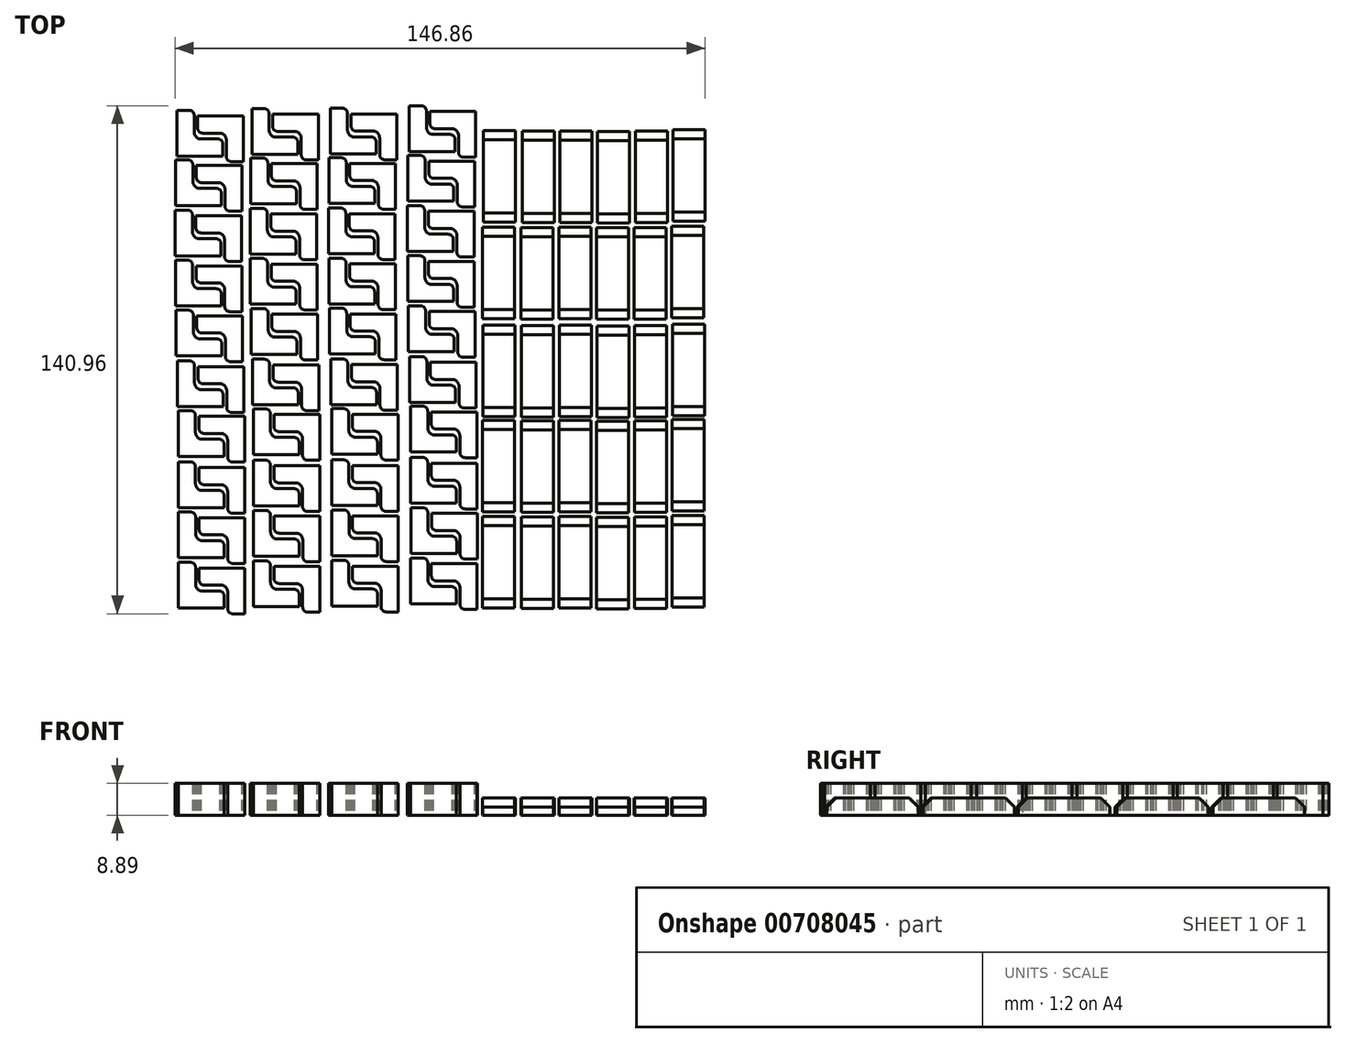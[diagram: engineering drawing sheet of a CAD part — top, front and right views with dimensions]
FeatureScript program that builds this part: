
annotation { "Feature Type Name" : "Feature", "Feature Type Description" : "" }
export const myFeature = defineFeature(function(context is Context, id is Id, definition is map)
    precondition{}
    {
        {
            var Q0;
            Q0=qCreatedBy(makeId("Top.planeOp"),FACE);
            var sketch = newSketch(context, id + "F0", { "sketchPlane" : qUnion([Q0])});
            skLineSegment(sketch, "E0.bottom", {"start": v(0, 0) * mm, "end": v(152.4, 0) * mm});
            skLineSegment(sketch, "E0.top", {"start": v(0, 152.4) * mm, "end": v(152.4, 152.4) * mm});
            skLineSegment(sketch, "E0.left", {"start": v(0, 0) * mm, "end": v(0, 152.4) * mm});
            skLineSegment(sketch, "E0.right", {"start": v(152.4, 0) * mm, "end": v(152.4, 152.4) * mm});
            skLineSegment(sketch, "E1.bottom", {"start": v(2.52, 2.34) * mm, "end": v(15.22, 2.34) * mm});
            skLineSegment(sketch, "E1.top", {"start": v(2.52, 15.04) * mm, "end": v(5.86, 15.04) * mm});
            skLineSegment(sketch, "E1.left", {"start": v(2.52, 2.34) * mm, "end": v(2.52, 15.04) * mm});
            skLineSegment(sketch, "E1.right", {"start": v(15.22, 2.34) * mm, "end": v(15.22, 5.68) * mm});
            skLineSegment(sketch, "E2.0", {"start": v(7.28, 9.05) * mm, "end": v(7.28, 13.62) * mm});
            skLineSegment(sketch, "E2.1", {"start": v(8.72, 7.1) * mm, "end": v(13.8, 7.1) * mm});
            skPoint(sketch, "E3.visualSharp", {"position": v(7.28, 15.04) * mm});
            skArc(sketch, "E3.filletArc", {"start": v(7.28, 13.62) * mm, "mid": v(6.87, 14.62) * mm, "end": v(5.86, 15.04) * mm});
            skPoint(sketch, "E4.visualSharp", {"position": v(15.22, 7.1) * mm});
            skArc(sketch, "E4.filletArc", {"start": v(15.22, 5.68) * mm, "mid": v(14.8, 6.69) * mm, "end": v(13.8, 7.1) * mm});
            skArc(sketch, "E5", {"start": v(7.28, 9.05) * mm, "mid": v(7.68, 7.84) * mm, "end": v(8.72, 7.1) * mm});
            skLineSegment(sketch, "E6.bottom", {"start": v(20.95, 13.45) * mm, "end": v(8.25, 13.45) * mm});
            skLineSegment(sketch, "E6.top", {"start": v(20.95, 0.75) * mm, "end": v(17.6, 0.75) * mm});
            skLineSegment(sketch, "E6.left", {"start": v(20.95, 13.45) * mm, "end": v(20.95, 0.75) * mm});
            skLineSegment(sketch, "E6.right", {"start": v(8.25, 13.45) * mm, "end": v(8.25, 10.1) * mm});
            skLineSegment(sketch, "E7.0", {"start": v(16.18, 6.74) * mm, "end": v(16.18, 2.17) * mm});
            skLineSegment(sketch, "E7.1", {"start": v(14.75, 8.68) * mm, "end": v(9.67, 8.68) * mm});
            skArc(sketch, "E8.filletArc", {"start": v(16.18, 2.17) * mm, "mid": v(16.6, 1.16) * mm, "end": v(17.6, 0.75) * mm});
            skArc(sketch, "E9.filletArc", {"start": v(8.25, 10.1) * mm, "mid": v(8.66, 9.1) * mm, "end": v(9.67, 8.68) * mm});
            skArc(sketch, "E10", {"start": v(16.18, 6.74) * mm, "mid": v(15.79, 7.95) * mm, "end": v(14.75, 8.68) * mm});
            skLineSegment(sketch, "E11.bottom", {"start": v(2.54, 16.3) * mm, "end": v(15.24, 16.3) * mm});
            skLineSegment(sketch, "E11.top", {"start": v(2.54, 29) * mm, "end": v(5.88, 29) * mm});
            skLineSegment(sketch, "E11.left", {"start": v(2.54, 16.3) * mm, "end": v(2.54, 29) * mm});
            skLineSegment(sketch, "E11.right", {"start": v(15.24, 16.3) * mm, "end": v(15.24, 19.65) * mm});
            skLineSegment(sketch, "E12.0", {"start": v(7.3, 23.02) * mm, "end": v(7.3, 27.6) * mm});
            skLineSegment(sketch, "E12.1", {"start": v(8.74, 21.07) * mm, "end": v(13.82, 21.07) * mm});
            skArc(sketch, "E13.filletArc", {"start": v(7.3, 27.6) * mm, "mid": v(6.89, 28.6) * mm, "end": v(5.88, 29) * mm});
            skArc(sketch, "E14.filletArc", {"start": v(15.24, 19.65) * mm, "mid": v(14.82, 20.66) * mm, "end": v(13.82, 21.07) * mm});
            skArc(sketch, "E15", {"start": v(7.3, 23.02) * mm, "mid": v(7.7, 21.81) * mm, "end": v(8.74, 21.07) * mm});
            skLineSegment(sketch, "E16.bottom", {"start": v(20.97, 27.42) * mm, "end": v(8.27, 27.42) * mm});
            skLineSegment(sketch, "E16.top", {"start": v(20.97, 14.72) * mm, "end": v(17.62, 14.72) * mm});
            skLineSegment(sketch, "E16.left", {"start": v(20.97, 27.42) * mm, "end": v(20.97, 14.72) * mm});
            skLineSegment(sketch, "E16.right", {"start": v(8.27, 27.42) * mm, "end": v(8.27, 24.07) * mm});
            skLineSegment(sketch, "E17.0", {"start": v(16.2, 20.7) * mm, "end": v(16.2, 16.14) * mm});
            skLineSegment(sketch, "E17.1", {"start": v(14.77, 22.65) * mm, "end": v(9.69, 22.65) * mm});
            skArc(sketch, "E18.filletArc", {"start": v(16.2, 16.14) * mm, "mid": v(16.62, 15.13) * mm, "end": v(17.62, 14.72) * mm});
            skArc(sketch, "E19.filletArc", {"start": v(8.27, 24.07) * mm, "mid": v(8.68, 23.07) * mm, "end": v(9.69, 22.65) * mm});
            skArc(sketch, "E20", {"start": v(16.2, 20.7) * mm, "mid": v(15.8, 21.92) * mm, "end": v(14.77, 22.65) * mm});
            skLineSegment(sketch, "E21.bottom", {"start": v(2.49, 30.24) * mm, "end": v(15.19, 30.24) * mm});
            skLineSegment(sketch, "E21.top", {"start": v(2.49, 42.94) * mm, "end": v(5.83, 42.94) * mm});
            skLineSegment(sketch, "E21.left", {"start": v(2.49, 30.24) * mm, "end": v(2.49, 42.94) * mm});
            skLineSegment(sketch, "E21.right", {"start": v(15.19, 30.24) * mm, "end": v(15.19, 33.58) * mm});
            skLineSegment(sketch, "E22.0", {"start": v(7.25, 36.95) * mm, "end": v(7.25, 41.52) * mm});
            skLineSegment(sketch, "E22.1", {"start": v(8.69, 35) * mm, "end": v(13.77, 35) * mm});
            skArc(sketch, "E23.filletArc", {"start": v(7.25, 41.52) * mm, "mid": v(6.84, 42.52) * mm, "end": v(5.83, 42.94) * mm});
            skArc(sketch, "E24.filletArc", {"start": v(15.19, 33.58) * mm, "mid": v(14.77, 34.59) * mm, "end": v(13.77, 35) * mm});
            skArc(sketch, "E25", {"start": v(7.25, 36.95) * mm, "mid": v(7.65, 35.74) * mm, "end": v(8.69, 35) * mm});
            skLineSegment(sketch, "E26.bottom", {"start": v(20.92, 41.35) * mm, "end": v(8.22, 41.35) * mm});
            skLineSegment(sketch, "E26.top", {"start": v(20.92, 28.65) * mm, "end": v(17.57, 28.65) * mm});
            skLineSegment(sketch, "E26.left", {"start": v(20.92, 41.35) * mm, "end": v(20.92, 28.65) * mm});
            skLineSegment(sketch, "E26.right", {"start": v(8.22, 41.35) * mm, "end": v(8.22, 38) * mm});
            skLineSegment(sketch, "E27.0", {"start": v(16.15, 34.64) * mm, "end": v(16.15, 30.07) * mm});
            skLineSegment(sketch, "E27.1", {"start": v(14.72, 36.58) * mm, "end": v(9.64, 36.58) * mm});
            skArc(sketch, "E28.filletArc", {"start": v(16.15, 30.07) * mm, "mid": v(16.57, 29.06) * mm, "end": v(17.57, 28.65) * mm});
            skArc(sketch, "E29.filletArc", {"start": v(8.22, 38) * mm, "mid": v(8.63, 37) * mm, "end": v(9.64, 36.58) * mm});
            skArc(sketch, "E30", {"start": v(16.15, 34.64) * mm, "mid": v(15.76, 35.84) * mm, "end": v(14.72, 36.58) * mm});
            skLineSegment(sketch, "E31.bottom", {"start": v(2.49, 44.46) * mm, "end": v(15.19, 44.46) * mm});
            skLineSegment(sketch, "E31.top", {"start": v(2.49, 57.16) * mm, "end": v(5.83, 57.16) * mm});
            skLineSegment(sketch, "E31.left", {"start": v(2.49, 44.46) * mm, "end": v(2.49, 57.16) * mm});
            skLineSegment(sketch, "E31.right", {"start": v(15.19, 44.46) * mm, "end": v(15.19, 47.8) * mm});
            skLineSegment(sketch, "E32.0", {"start": v(7.25, 51.17) * mm, "end": v(7.25, 55.74) * mm});
            skLineSegment(sketch, "E32.1", {"start": v(8.69, 49.23) * mm, "end": v(13.77, 49.23) * mm});
            skArc(sketch, "E33.filletArc", {"start": v(7.25, 55.74) * mm, "mid": v(6.84, 56.75) * mm, "end": v(5.83, 57.16) * mm});
            skArc(sketch, "E34.filletArc", {"start": v(15.19, 47.8) * mm, "mid": v(14.77, 48.8) * mm, "end": v(13.77, 49.23) * mm});
            skArc(sketch, "E35", {"start": v(7.25, 51.17) * mm, "mid": v(7.65, 49.96) * mm, "end": v(8.69, 49.23) * mm});
            skLineSegment(sketch, "E36.bottom", {"start": v(20.92, 55.57) * mm, "end": v(8.22, 55.57) * mm});
            skLineSegment(sketch, "E36.top", {"start": v(20.92, 42.87) * mm, "end": v(17.57, 42.87) * mm});
            skLineSegment(sketch, "E36.left", {"start": v(20.92, 55.57) * mm, "end": v(20.92, 42.87) * mm});
            skLineSegment(sketch, "E36.right", {"start": v(8.22, 55.57) * mm, "end": v(8.22, 52.23) * mm});
            skLineSegment(sketch, "E37.0", {"start": v(16.15, 48.86) * mm, "end": v(16.15, 44.29) * mm});
            skLineSegment(sketch, "E37.1", {"start": v(14.72, 50.8) * mm, "end": v(9.64, 50.8) * mm});
            skArc(sketch, "E38.filletArc", {"start": v(16.15, 44.29) * mm, "mid": v(16.57, 43.29) * mm, "end": v(17.57, 42.87) * mm});
            skArc(sketch, "E39.filletArc", {"start": v(8.22, 52.23) * mm, "mid": v(8.63, 51.22) * mm, "end": v(9.64, 50.8) * mm});
            skArc(sketch, "E40", {"start": v(16.15, 48.86) * mm, "mid": v(15.76, 50.07) * mm, "end": v(14.72, 50.8) * mm});
            skLineSegment(sketch, "E41.bottom", {"start": v(2.24, 58.23) * mm, "end": v(14.94, 58.23) * mm});
            skLineSegment(sketch, "E41.top", {"start": v(2.24, 70.93) * mm, "end": v(5.58, 70.93) * mm});
            skLineSegment(sketch, "E41.left", {"start": v(2.24, 58.23) * mm, "end": v(2.24, 70.93) * mm});
            skLineSegment(sketch, "E41.right", {"start": v(14.94, 58.23) * mm, "end": v(14.94, 61.57) * mm});
            skLineSegment(sketch, "E42.0", {"start": v(7, 64.94) * mm, "end": v(7, 69.51) * mm});
            skLineSegment(sketch, "E42.1", {"start": v(8.43, 63) * mm, "end": v(13.52, 63) * mm});
            skArc(sketch, "E43.filletArc", {"start": v(7, 69.51) * mm, "mid": v(6.58, 70.51) * mm, "end": v(5.58, 70.93) * mm});
            skArc(sketch, "E44.filletArc", {"start": v(14.94, 61.57) * mm, "mid": v(14.52, 62.58) * mm, "end": v(13.52, 63) * mm});
            skArc(sketch, "E45", {"start": v(7, 64.94) * mm, "mid": v(7.4, 63.73) * mm, "end": v(8.43, 63) * mm});
            skLineSegment(sketch, "E46.bottom", {"start": v(20.67, 69.34) * mm, "end": v(7.97, 69.34) * mm});
            skLineSegment(sketch, "E46.top", {"start": v(20.67, 56.64) * mm, "end": v(17.32, 56.64) * mm});
            skLineSegment(sketch, "E46.left", {"start": v(20.67, 69.34) * mm, "end": v(20.67, 56.64) * mm});
            skLineSegment(sketch, "E46.right", {"start": v(7.97, 69.34) * mm, "end": v(7.97, 66) * mm});
            skLineSegment(sketch, "E47.0", {"start": v(15.9, 62.63) * mm, "end": v(15.9, 58.06) * mm});
            skLineSegment(sketch, "E47.1", {"start": v(14.47, 64.58) * mm, "end": v(9.39, 64.58) * mm});
            skArc(sketch, "E48.filletArc", {"start": v(15.9, 58.06) * mm, "mid": v(16.32, 57.05) * mm, "end": v(17.32, 56.64) * mm});
            skArc(sketch, "E49.filletArc", {"start": v(7.97, 66) * mm, "mid": v(8.38, 65) * mm, "end": v(9.39, 64.58) * mm});
            skArc(sketch, "E50", {"start": v(15.9, 62.63) * mm, "mid": v(15.5, 63.84) * mm, "end": v(14.47, 64.58) * mm});
            skLineSegment(sketch, "E51.bottom", {"start": v(1.9, 72.32) * mm, "end": v(14.6, 72.32) * mm});
            skLineSegment(sketch, "E51.top", {"start": v(1.9, 85.02) * mm, "end": v(5.24, 85.02) * mm});
            skLineSegment(sketch, "E51.left", {"start": v(1.9, 72.32) * mm, "end": v(1.9, 85.02) * mm});
            skLineSegment(sketch, "E51.right", {"start": v(14.6, 72.32) * mm, "end": v(14.6, 75.66) * mm});
            skLineSegment(sketch, "E52.0", {"start": v(6.66, 79.03) * mm, "end": v(6.66, 83.6) * mm});
            skLineSegment(sketch, "E52.1", {"start": v(8.1, 77.08) * mm, "end": v(13.18, 77.08) * mm});
            skArc(sketch, "E53.filletArc", {"start": v(6.66, 83.6) * mm, "mid": v(6.24, 84.6) * mm, "end": v(5.24, 85.02) * mm});
            skArc(sketch, "E54.filletArc", {"start": v(14.6, 75.66) * mm, "mid": v(14.18, 76.66) * mm, "end": v(13.18, 77.08) * mm});
            skArc(sketch, "E55", {"start": v(6.66, 79.03) * mm, "mid": v(7.06, 77.82) * mm, "end": v(8.1, 77.08) * mm});
            skLineSegment(sketch, "E56.bottom", {"start": v(20.33, 83.42) * mm, "end": v(7.63, 83.42) * mm});
            skLineSegment(sketch, "E56.top", {"start": v(20.33, 70.72) * mm, "end": v(16.98, 70.72) * mm});
            skLineSegment(sketch, "E56.left", {"start": v(20.33, 83.42) * mm, "end": v(20.33, 70.72) * mm});
            skLineSegment(sketch, "E56.right", {"start": v(7.63, 83.42) * mm, "end": v(7.63, 80.08) * mm});
            skLineSegment(sketch, "E57.0", {"start": v(15.56, 76.71) * mm, "end": v(15.56, 72.14) * mm});
            skLineSegment(sketch, "E57.1", {"start": v(14.13, 78.66) * mm, "end": v(9.05, 78.66) * mm});
            skArc(sketch, "E58.filletArc", {"start": v(15.56, 72.14) * mm, "mid": v(15.98, 71.14) * mm, "end": v(16.98, 70.72) * mm});
            skArc(sketch, "E59.filletArc", {"start": v(7.63, 80.08) * mm, "mid": v(8.04, 79.08) * mm, "end": v(9.05, 78.66) * mm});
            skArc(sketch, "E60", {"start": v(15.56, 76.71) * mm, "mid": v(15.17, 77.92) * mm, "end": v(14.13, 78.66) * mm});
            skLineSegment(sketch, "E61.bottom", {"start": v(1.7, 86.2) * mm, "end": v(14.4, 86.2) * mm});
            skLineSegment(sketch, "E61.top", {"start": v(1.7, 98.9) * mm, "end": v(5.05, 98.9) * mm});
            skLineSegment(sketch, "E61.left", {"start": v(1.7, 86.2) * mm, "end": v(1.7, 98.9) * mm});
            skLineSegment(sketch, "E61.right", {"start": v(14.4, 86.2) * mm, "end": v(14.4, 89.55) * mm});
            skLineSegment(sketch, "E62.0", {"start": v(6.47, 92.92) * mm, "end": v(6.47, 97.49) * mm});
            skLineSegment(sketch, "E62.1", {"start": v(7.9, 90.97) * mm, "end": v(12.99, 90.97) * mm});
            skArc(sketch, "E63.filletArc", {"start": v(6.47, 97.49) * mm, "mid": v(6.05, 98.49) * mm, "end": v(5.05, 98.9) * mm});
            skArc(sketch, "E64.filletArc", {"start": v(14.4, 89.55) * mm, "mid": v(14, 90.55) * mm, "end": v(12.99, 90.97) * mm});
            skArc(sketch, "E65", {"start": v(6.47, 92.92) * mm, "mid": v(6.87, 91.7) * mm, "end": v(7.9, 90.97) * mm});
            skLineSegment(sketch, "E66.bottom", {"start": v(20.14, 97.31) * mm, "end": v(7.44, 97.31) * mm});
            skLineSegment(sketch, "E66.top", {"start": v(20.14, 84.61) * mm, "end": v(16.8, 84.61) * mm});
            skLineSegment(sketch, "E66.left", {"start": v(20.14, 97.31) * mm, "end": v(20.14, 84.61) * mm});
            skLineSegment(sketch, "E66.right", {"start": v(7.44, 97.31) * mm, "end": v(7.44, 93.97) * mm});
            skLineSegment(sketch, "E67.0", {"start": v(15.37, 90.6) * mm, "end": v(15.37, 86.03) * mm});
            skLineSegment(sketch, "E67.1", {"start": v(13.94, 92.55) * mm, "end": v(8.86, 92.55) * mm});
            skArc(sketch, "E68.filletArc", {"start": v(15.37, 86.03) * mm, "mid": v(15.79, 85.03) * mm, "end": v(16.8, 84.61) * mm});
            skArc(sketch, "E69.filletArc", {"start": v(7.44, 93.97) * mm, "mid": v(7.85, 92.96) * mm, "end": v(8.86, 92.55) * mm});
            skArc(sketch, "E70", {"start": v(15.37, 90.6) * mm, "mid": v(14.98, 91.81) * mm, "end": v(13.94, 92.55) * mm});
            skLineSegment(sketch, "E71.bottom", {"start": v(1.65, 100.1) * mm, "end": v(14.35, 100.1) * mm});
            skLineSegment(sketch, "E71.top", {"start": v(1.65, 112.8) * mm, "end": v(4.99, 112.8) * mm});
            skLineSegment(sketch, "E71.left", {"start": v(1.65, 100.1) * mm, "end": v(1.65, 112.8) * mm});
            skLineSegment(sketch, "E71.right", {"start": v(14.35, 100.1) * mm, "end": v(14.35, 103.45) * mm});
            skLineSegment(sketch, "E72.0", {"start": v(6.4, 106.81) * mm, "end": v(6.4, 111.38) * mm});
            skLineSegment(sketch, "E72.1", {"start": v(7.84, 104.87) * mm, "end": v(12.93, 104.87) * mm});
            skArc(sketch, "E73.filletArc", {"start": v(6.4, 111.38) * mm, "mid": v(6, 112.39) * mm, "end": v(4.99, 112.8) * mm});
            skArc(sketch, "E74.filletArc", {"start": v(14.35, 103.45) * mm, "mid": v(13.93, 104.45) * mm, "end": v(12.93, 104.87) * mm});
            skArc(sketch, "E75", {"start": v(6.4, 106.81) * mm, "mid": v(6.8, 105.6) * mm, "end": v(7.84, 104.87) * mm});
            skLineSegment(sketch, "E76.bottom", {"start": v(20.07, 111.21) * mm, "end": v(7.37, 111.21) * mm});
            skLineSegment(sketch, "E76.top", {"start": v(20.07, 98.51) * mm, "end": v(16.73, 98.51) * mm});
            skLineSegment(sketch, "E76.left", {"start": v(20.07, 111.21) * mm, "end": v(20.07, 98.51) * mm});
            skLineSegment(sketch, "E76.right", {"start": v(7.37, 111.21) * mm, "end": v(7.37, 107.87) * mm});
            skLineSegment(sketch, "E77.0", {"start": v(15.31, 104.5) * mm, "end": v(15.31, 99.93) * mm});
            skLineSegment(sketch, "E77.1", {"start": v(13.88, 106.45) * mm, "end": v(8.8, 106.45) * mm});
            skArc(sketch, "E78.filletArc", {"start": v(15.31, 99.93) * mm, "mid": v(15.73, 98.93) * mm, "end": v(16.73, 98.51) * mm});
            skArc(sketch, "E79.filletArc", {"start": v(7.37, 107.87) * mm, "mid": v(7.79, 106.86) * mm, "end": v(8.8, 106.45) * mm});
            skArc(sketch, "E80", {"start": v(15.31, 104.5) * mm, "mid": v(14.91, 105.7) * mm, "end": v(13.88, 106.45) * mm});
            skLineSegment(sketch, "E81.bottom", {"start": v(1.78, 114.06) * mm, "end": v(14.48, 114.06) * mm});
            skLineSegment(sketch, "E81.top", {"start": v(1.78, 126.76) * mm, "end": v(5.12, 126.76) * mm});
            skLineSegment(sketch, "E81.left", {"start": v(1.78, 114.06) * mm, "end": v(1.78, 126.76) * mm});
            skLineSegment(sketch, "E81.right", {"start": v(14.48, 114.06) * mm, "end": v(14.48, 117.4) * mm});
            skLineSegment(sketch, "E82.0", {"start": v(6.54, 120.77) * mm, "end": v(6.54, 125.34) * mm});
            skLineSegment(sketch, "E82.1", {"start": v(7.98, 118.82) * mm, "end": v(13.06, 118.82) * mm});
            skArc(sketch, "E83.filletArc", {"start": v(6.54, 125.34) * mm, "mid": v(6.13, 126.34) * mm, "end": v(5.12, 126.76) * mm});
            skArc(sketch, "E84.filletArc", {"start": v(14.48, 117.4) * mm, "mid": v(14.06, 118.4) * mm, "end": v(13.06, 118.82) * mm});
            skArc(sketch, "E85", {"start": v(6.54, 120.77) * mm, "mid": v(6.94, 119.56) * mm, "end": v(7.98, 118.82) * mm});
            skLineSegment(sketch, "E86.bottom", {"start": v(20.2, 125.16) * mm, "end": v(7.5, 125.16) * mm});
            skLineSegment(sketch, "E86.top", {"start": v(20.2, 112.46) * mm, "end": v(16.86, 112.46) * mm});
            skLineSegment(sketch, "E86.left", {"start": v(20.2, 125.16) * mm, "end": v(20.2, 112.46) * mm});
            skLineSegment(sketch, "E86.right", {"start": v(7.5, 125.16) * mm, "end": v(7.5, 121.82) * mm});
            skLineSegment(sketch, "E87.0", {"start": v(15.44, 118.45) * mm, "end": v(15.44, 113.88) * mm});
            skLineSegment(sketch, "E87.1", {"start": v(14.01, 120.4) * mm, "end": v(8.93, 120.4) * mm});
            skArc(sketch, "E88.filletArc", {"start": v(15.44, 113.88) * mm, "mid": v(15.86, 112.88) * mm, "end": v(16.86, 112.46) * mm});
            skArc(sketch, "E89.filletArc", {"start": v(7.5, 121.82) * mm, "mid": v(7.92, 120.82) * mm, "end": v(8.93, 120.4) * mm});
            skArc(sketch, "E90", {"start": v(15.44, 118.45) * mm, "mid": v(15.05, 119.66) * mm, "end": v(14.01, 120.4) * mm});
            skLineSegment(sketch, "E91.bottom", {"start": v(2.13, 127.8) * mm, "end": v(14.83, 127.8) * mm});
            skLineSegment(sketch, "E91.top", {"start": v(2.13, 140.5) * mm, "end": v(5.47, 140.5) * mm});
            skLineSegment(sketch, "E91.left", {"start": v(2.13, 127.8) * mm, "end": v(2.13, 140.5) * mm});
            skLineSegment(sketch, "E91.right", {"start": v(14.83, 127.8) * mm, "end": v(14.83, 131.14) * mm});
            skLineSegment(sketch, "E92.0", {"start": v(6.9, 134.5) * mm, "end": v(6.9, 139.07) * mm});
            skLineSegment(sketch, "E92.1", {"start": v(8.33, 132.56) * mm, "end": v(13.4, 132.56) * mm});
            skArc(sketch, "E93.filletArc", {"start": v(6.9, 139.07) * mm, "mid": v(6.48, 140.08) * mm, "end": v(5.47, 140.5) * mm});
            skArc(sketch, "E94.filletArc", {"start": v(14.83, 131.14) * mm, "mid": v(14.41, 132.14) * mm, "end": v(13.4, 132.56) * mm});
            skArc(sketch, "E95", {"start": v(6.9, 134.5) * mm, "mid": v(7.29, 133.3) * mm, "end": v(8.33, 132.56) * mm});
            skLineSegment(sketch, "E96.bottom", {"start": v(20.56, 138.9) * mm, "end": v(7.86, 138.9) * mm});
            skLineSegment(sketch, "E96.top", {"start": v(20.56, 126.2) * mm, "end": v(17.21, 126.2) * mm});
            skLineSegment(sketch, "E96.left", {"start": v(20.56, 138.9) * mm, "end": v(20.56, 126.2) * mm});
            skLineSegment(sketch, "E96.right", {"start": v(7.86, 138.9) * mm, "end": v(7.86, 135.56) * mm});
            skLineSegment(sketch, "E97.0", {"start": v(15.8, 132.19) * mm, "end": v(15.8, 127.62) * mm});
            skLineSegment(sketch, "E97.1", {"start": v(14.36, 134.14) * mm, "end": v(9.28, 134.14) * mm});
            skArc(sketch, "E98.filletArc", {"start": v(15.8, 127.62) * mm, "mid": v(16.21, 126.62) * mm, "end": v(17.21, 126.2) * mm});
            skArc(sketch, "E99.filletArc", {"start": v(7.86, 135.56) * mm, "mid": v(8.27, 134.55) * mm, "end": v(9.28, 134.14) * mm});
            skArc(sketch, "E100", {"start": v(15.8, 132.19) * mm, "mid": v(15.4, 133.4) * mm, "end": v(14.36, 134.14) * mm});
            skLineSegment(sketch, "E101.bottom", {"start": v(23.3, 2.82) * mm, "end": v(36, 2.82) * mm});
            skLineSegment(sketch, "E101.top", {"start": v(23.3, 15.52) * mm, "end": v(26.65, 15.52) * mm});
            skLineSegment(sketch, "E101.left", {"start": v(23.3, 2.82) * mm, "end": v(23.3, 15.52) * mm});
            skLineSegment(sketch, "E101.right", {"start": v(36, 2.82) * mm, "end": v(36, 6.16) * mm});
            skLineSegment(sketch, "E102.0", {"start": v(28.07, 9.53) * mm, "end": v(28.07, 14.1) * mm});
            skLineSegment(sketch, "E102.1", {"start": v(29.5, 7.58) * mm, "end": v(34.58, 7.58) * mm});
            skArc(sketch, "E103.filletArc", {"start": v(28.07, 14.1) * mm, "mid": v(27.65, 15.1) * mm, "end": v(26.65, 15.52) * mm});
            skArc(sketch, "E104.filletArc", {"start": v(36, 6.16) * mm, "mid": v(35.59, 7.16) * mm, "end": v(34.58, 7.58) * mm});
            skArc(sketch, "E105", {"start": v(28.07, 9.53) * mm, "mid": v(28.46, 8.32) * mm, "end": v(29.5, 7.58) * mm});
            skLineSegment(sketch, "E106.bottom", {"start": v(41.73, 13.92) * mm, "end": v(29.03, 13.92) * mm});
            skLineSegment(sketch, "E106.top", {"start": v(41.73, 1.22) * mm, "end": v(38.39, 1.22) * mm});
            skLineSegment(sketch, "E106.left", {"start": v(41.73, 13.92) * mm, "end": v(41.73, 1.22) * mm});
            skLineSegment(sketch, "E106.right", {"start": v(29.03, 13.92) * mm, "end": v(29.03, 10.58) * mm});
            skLineSegment(sketch, "E107.0", {"start": v(36.97, 7.21) * mm, "end": v(36.97, 2.64) * mm});
            skLineSegment(sketch, "E107.1", {"start": v(35.54, 9.16) * mm, "end": v(30.45, 9.16) * mm});
            skArc(sketch, "E108.filletArc", {"start": v(36.97, 2.64) * mm, "mid": v(37.39, 1.64) * mm, "end": v(38.39, 1.22) * mm});
            skArc(sketch, "E109.filletArc", {"start": v(29.03, 10.58) * mm, "mid": v(29.45, 9.58) * mm, "end": v(30.45, 9.16) * mm});
            skArc(sketch, "E110", {"start": v(36.97, 7.21) * mm, "mid": v(36.57, 8.42) * mm, "end": v(35.54, 9.16) * mm});
            skLineSegment(sketch, "E111.bottom", {"start": v(23.32, 16.79) * mm, "end": v(36.02, 16.79) * mm});
            skLineSegment(sketch, "E111.top", {"start": v(23.32, 29.49) * mm, "end": v(26.67, 29.49) * mm});
            skLineSegment(sketch, "E111.left", {"start": v(23.32, 16.79) * mm, "end": v(23.32, 29.49) * mm});
            skLineSegment(sketch, "E111.right", {"start": v(36.02, 16.79) * mm, "end": v(36.02, 20.13) * mm});
            skLineSegment(sketch, "E112.0", {"start": v(28.09, 23.5) * mm, "end": v(28.09, 28.07) * mm});
            skLineSegment(sketch, "E112.1", {"start": v(29.52, 21.55) * mm, "end": v(34.6, 21.55) * mm});
            skArc(sketch, "E113.filletArc", {"start": v(28.09, 28.07) * mm, "mid": v(27.67, 29.07) * mm, "end": v(26.67, 29.49) * mm});
            skArc(sketch, "E114.filletArc", {"start": v(36.02, 20.13) * mm, "mid": v(35.6, 21.13) * mm, "end": v(34.6, 21.55) * mm});
            skArc(sketch, "E115", {"start": v(28.09, 23.5) * mm, "mid": v(28.48, 22.29) * mm, "end": v(29.52, 21.55) * mm});
            skLineSegment(sketch, "E116.bottom", {"start": v(41.75, 27.9) * mm, "end": v(29.05, 27.9) * mm});
            skLineSegment(sketch, "E116.top", {"start": v(41.75, 15.2) * mm, "end": v(38.4, 15.2) * mm});
            skLineSegment(sketch, "E116.left", {"start": v(41.75, 27.9) * mm, "end": v(41.75, 15.2) * mm});
            skLineSegment(sketch, "E116.right", {"start": v(29.05, 27.9) * mm, "end": v(29.05, 24.55) * mm});
            skLineSegment(sketch, "E117.0", {"start": v(37, 21.18) * mm, "end": v(37, 16.61) * mm});
            skLineSegment(sketch, "E117.1", {"start": v(35.56, 23.13) * mm, "end": v(30.47, 23.13) * mm});
            skArc(sketch, "E118.filletArc", {"start": v(37, 16.61) * mm, "mid": v(37.4, 15.61) * mm, "end": v(38.4, 15.2) * mm});
            skArc(sketch, "E119.filletArc", {"start": v(29.05, 24.55) * mm, "mid": v(29.47, 23.55) * mm, "end": v(30.47, 23.13) * mm});
            skArc(sketch, "E120", {"start": v(37, 21.18) * mm, "mid": v(36.6, 22.4) * mm, "end": v(35.56, 23.13) * mm});
            skLineSegment(sketch, "E121.bottom", {"start": v(23.27, 30.72) * mm, "end": v(35.97, 30.72) * mm});
            skLineSegment(sketch, "E121.top", {"start": v(23.27, 43.42) * mm, "end": v(26.62, 43.42) * mm});
            skLineSegment(sketch, "E121.left", {"start": v(23.27, 30.72) * mm, "end": v(23.27, 43.42) * mm});
            skLineSegment(sketch, "E121.right", {"start": v(35.97, 30.72) * mm, "end": v(35.97, 34.06) * mm});
            skLineSegment(sketch, "E122.0", {"start": v(28.04, 37.43) * mm, "end": v(28.04, 42) * mm});
            skLineSegment(sketch, "E122.1", {"start": v(29.47, 35.48) * mm, "end": v(34.55, 35.48) * mm});
            skArc(sketch, "E123.filletArc", {"start": v(28.04, 42) * mm, "mid": v(27.62, 43) * mm, "end": v(26.62, 43.42) * mm});
            skArc(sketch, "E124.filletArc", {"start": v(35.97, 34.06) * mm, "mid": v(35.56, 35.06) * mm, "end": v(34.55, 35.48) * mm});
            skArc(sketch, "E125", {"start": v(28.04, 37.43) * mm, "mid": v(28.43, 36.22) * mm, "end": v(29.47, 35.48) * mm});
            skLineSegment(sketch, "E126.bottom", {"start": v(41.7, 41.82) * mm, "end": v(29, 41.82) * mm});
            skLineSegment(sketch, "E126.top", {"start": v(41.7, 29.12) * mm, "end": v(38.36, 29.12) * mm});
            skLineSegment(sketch, "E126.left", {"start": v(41.7, 41.82) * mm, "end": v(41.7, 29.12) * mm});
            skLineSegment(sketch, "E126.right", {"start": v(29, 41.82) * mm, "end": v(29, 38.48) * mm});
            skLineSegment(sketch, "E127.0", {"start": v(36.94, 35.11) * mm, "end": v(36.94, 30.54) * mm});
            skLineSegment(sketch, "E127.1", {"start": v(35.5, 37.06) * mm, "end": v(30.42, 37.06) * mm});
            skArc(sketch, "E128.filletArc", {"start": v(36.94, 30.54) * mm, "mid": v(37.36, 29.54) * mm, "end": v(38.36, 29.12) * mm});
            skArc(sketch, "E129.filletArc", {"start": v(29, 38.48) * mm, "mid": v(29.42, 37.48) * mm, "end": v(30.42, 37.06) * mm});
            skArc(sketch, "E130", {"start": v(36.94, 35.11) * mm, "mid": v(36.54, 36.32) * mm, "end": v(35.5, 37.06) * mm});
            skLineSegment(sketch, "E131.bottom", {"start": v(23.27, 44.94) * mm, "end": v(35.97, 44.94) * mm});
            skLineSegment(sketch, "E131.top", {"start": v(23.27, 57.64) * mm, "end": v(26.62, 57.64) * mm});
            skLineSegment(sketch, "E131.left", {"start": v(23.27, 44.94) * mm, "end": v(23.27, 57.64) * mm});
            skLineSegment(sketch, "E131.right", {"start": v(35.97, 44.94) * mm, "end": v(35.97, 48.28) * mm});
            skLineSegment(sketch, "E132.0", {"start": v(28.04, 51.65) * mm, "end": v(28.04, 56.22) * mm});
            skLineSegment(sketch, "E132.1", {"start": v(29.47, 49.7) * mm, "end": v(34.55, 49.7) * mm});
            skArc(sketch, "E133.filletArc", {"start": v(28.04, 56.22) * mm, "mid": v(27.62, 57.22) * mm, "end": v(26.62, 57.64) * mm});
            skArc(sketch, "E134.filletArc", {"start": v(35.97, 48.28) * mm, "mid": v(35.56, 49.29) * mm, "end": v(34.55, 49.7) * mm});
            skArc(sketch, "E135", {"start": v(28.04, 51.65) * mm, "mid": v(28.43, 50.44) * mm, "end": v(29.47, 49.7) * mm});
            skLineSegment(sketch, "E136.bottom", {"start": v(41.7, 56.05) * mm, "end": v(29, 56.05) * mm});
            skLineSegment(sketch, "E136.top", {"start": v(41.7, 43.35) * mm, "end": v(38.36, 43.35) * mm});
            skLineSegment(sketch, "E136.left", {"start": v(41.7, 56.05) * mm, "end": v(41.7, 43.35) * mm});
            skLineSegment(sketch, "E136.right", {"start": v(29, 56.05) * mm, "end": v(29, 52.7) * mm});
            skLineSegment(sketch, "E137.0", {"start": v(36.94, 49.34) * mm, "end": v(36.94, 44.77) * mm});
            skLineSegment(sketch, "E137.1", {"start": v(35.5, 51.29) * mm, "end": v(30.42, 51.29) * mm});
            skArc(sketch, "E138.filletArc", {"start": v(36.94, 44.77) * mm, "mid": v(37.36, 43.76) * mm, "end": v(38.36, 43.35) * mm});
            skArc(sketch, "E139.filletArc", {"start": v(29, 52.7) * mm, "mid": v(29.42, 51.7) * mm, "end": v(30.42, 51.29) * mm});
            skArc(sketch, "E140", {"start": v(36.94, 49.34) * mm, "mid": v(36.54, 50.55) * mm, "end": v(35.5, 51.29) * mm});
            skLineSegment(sketch, "E141.bottom", {"start": v(23.02, 58.7) * mm, "end": v(35.72, 58.7) * mm});
            skLineSegment(sketch, "E141.top", {"start": v(23.02, 71.4) * mm, "end": v(26.37, 71.4) * mm});
            skLineSegment(sketch, "E141.left", {"start": v(23.02, 58.7) * mm, "end": v(23.02, 71.4) * mm});
            skLineSegment(sketch, "E141.right", {"start": v(35.72, 58.7) * mm, "end": v(35.72, 62.05) * mm});
            skLineSegment(sketch, "E142.0", {"start": v(27.79, 65.42) * mm, "end": v(27.79, 69.99) * mm});
            skLineSegment(sketch, "E142.1", {"start": v(29.22, 63.47) * mm, "end": v(34.3, 63.47) * mm});
            skArc(sketch, "E143.filletArc", {"start": v(27.79, 69.99) * mm, "mid": v(27.37, 71) * mm, "end": v(26.37, 71.4) * mm});
            skArc(sketch, "E144.filletArc", {"start": v(35.72, 62.05) * mm, "mid": v(35.3, 63.05) * mm, "end": v(34.3, 63.47) * mm});
            skArc(sketch, "E145", {"start": v(27.79, 65.42) * mm, "mid": v(28.18, 64.2) * mm, "end": v(29.22, 63.47) * mm});
            skLineSegment(sketch, "E146.bottom", {"start": v(41.45, 69.82) * mm, "end": v(28.75, 69.82) * mm});
            skLineSegment(sketch, "E146.top", {"start": v(41.45, 57.12) * mm, "end": v(38.1, 57.12) * mm});
            skLineSegment(sketch, "E146.left", {"start": v(41.45, 69.82) * mm, "end": v(41.45, 57.12) * mm});
            skLineSegment(sketch, "E146.right", {"start": v(28.75, 69.82) * mm, "end": v(28.75, 66.47) * mm});
            skLineSegment(sketch, "E147.0", {"start": v(36.69, 63.1) * mm, "end": v(36.69, 58.53) * mm});
            skLineSegment(sketch, "E147.1", {"start": v(35.25, 65.05) * mm, "end": v(30.17, 65.05) * mm});
            skArc(sketch, "E148.filletArc", {"start": v(36.69, 58.53) * mm, "mid": v(37.1, 57.53) * mm, "end": v(38.1, 57.12) * mm});
            skArc(sketch, "E149.filletArc", {"start": v(28.75, 66.47) * mm, "mid": v(29.17, 65.47) * mm, "end": v(30.17, 65.05) * mm});
            skArc(sketch, "E150", {"start": v(36.69, 63.1) * mm, "mid": v(36.3, 64.31) * mm, "end": v(35.25, 65.05) * mm});
            skLineSegment(sketch, "E151.bottom", {"start": v(22.68, 72.8) * mm, "end": v(35.38, 72.8) * mm});
            skLineSegment(sketch, "E151.top", {"start": v(22.68, 85.5) * mm, "end": v(26.03, 85.5) * mm});
            skLineSegment(sketch, "E151.left", {"start": v(22.68, 72.8) * mm, "end": v(22.68, 85.5) * mm});
            skLineSegment(sketch, "E151.right", {"start": v(35.38, 72.8) * mm, "end": v(35.38, 76.14) * mm});
            skLineSegment(sketch, "E152.0", {"start": v(27.45, 79.5) * mm, "end": v(27.45, 84.07) * mm});
            skLineSegment(sketch, "E152.1", {"start": v(28.88, 77.56) * mm, "end": v(33.96, 77.56) * mm});
            skArc(sketch, "E153.filletArc", {"start": v(27.45, 84.07) * mm, "mid": v(27.03, 85.08) * mm, "end": v(26.03, 85.5) * mm});
            skArc(sketch, "E154.filletArc", {"start": v(35.38, 76.14) * mm, "mid": v(34.97, 77.14) * mm, "end": v(33.96, 77.56) * mm});
            skArc(sketch, "E155", {"start": v(27.45, 79.5) * mm, "mid": v(27.84, 78.3) * mm, "end": v(28.88, 77.56) * mm});
            skLineSegment(sketch, "E156.bottom", {"start": v(41.11, 83.9) * mm, "end": v(28.41, 83.9) * mm});
            skLineSegment(sketch, "E156.top", {"start": v(41.11, 71.2) * mm, "end": v(37.77, 71.2) * mm});
            skLineSegment(sketch, "E156.left", {"start": v(41.11, 83.9) * mm, "end": v(41.11, 71.2) * mm});
            skLineSegment(sketch, "E156.right", {"start": v(28.41, 83.9) * mm, "end": v(28.41, 80.56) * mm});
            skLineSegment(sketch, "E157.0", {"start": v(36.35, 77.19) * mm, "end": v(36.35, 72.62) * mm});
            skLineSegment(sketch, "E157.1", {"start": v(34.91, 79.14) * mm, "end": v(29.83, 79.14) * mm});
            skArc(sketch, "E158.filletArc", {"start": v(36.35, 72.62) * mm, "mid": v(36.76, 71.62) * mm, "end": v(37.77, 71.2) * mm});
            skArc(sketch, "E159.filletArc", {"start": v(28.41, 80.56) * mm, "mid": v(28.83, 79.55) * mm, "end": v(29.83, 79.14) * mm});
            skArc(sketch, "E160", {"start": v(36.35, 77.19) * mm, "mid": v(35.95, 78.4) * mm, "end": v(34.91, 79.14) * mm});
            skLineSegment(sketch, "E161.bottom", {"start": v(22.5, 86.68) * mm, "end": v(35.2, 86.68) * mm});
            skLineSegment(sketch, "E161.top", {"start": v(22.5, 99.38) * mm, "end": v(25.84, 99.38) * mm});
            skLineSegment(sketch, "E161.left", {"start": v(22.5, 86.68) * mm, "end": v(22.5, 99.38) * mm});
            skLineSegment(sketch, "E161.right", {"start": v(35.2, 86.68) * mm, "end": v(35.2, 90.03) * mm});
            skLineSegment(sketch, "E162.0", {"start": v(27.26, 93.4) * mm, "end": v(27.26, 97.96) * mm});
            skLineSegment(sketch, "E162.1", {"start": v(28.69, 91.44) * mm, "end": v(33.77, 91.44) * mm});
            skArc(sketch, "E163.filletArc", {"start": v(27.26, 97.96) * mm, "mid": v(26.84, 98.97) * mm, "end": v(25.84, 99.38) * mm});
            skArc(sketch, "E164.filletArc", {"start": v(35.2, 90.03) * mm, "mid": v(34.78, 91.03) * mm, "end": v(33.77, 91.44) * mm});
            skArc(sketch, "E165", {"start": v(27.26, 93.4) * mm, "mid": v(27.65, 92.18) * mm, "end": v(28.69, 91.44) * mm});
            skLineSegment(sketch, "E166.bottom", {"start": v(40.92, 97.79) * mm, "end": v(28.22, 97.79) * mm});
            skLineSegment(sketch, "E166.top", {"start": v(40.92, 85.09) * mm, "end": v(37.58, 85.09) * mm});
            skLineSegment(sketch, "E166.left", {"start": v(40.92, 97.79) * mm, "end": v(40.92, 85.09) * mm});
            skLineSegment(sketch, "E166.right", {"start": v(28.22, 97.79) * mm, "end": v(28.22, 94.45) * mm});
            skLineSegment(sketch, "E167.0", {"start": v(36.16, 91.08) * mm, "end": v(36.16, 86.5) * mm});
            skLineSegment(sketch, "E167.1", {"start": v(34.72, 93.03) * mm, "end": v(29.64, 93.03) * mm});
            skArc(sketch, "E168.filletArc", {"start": v(36.16, 86.5) * mm, "mid": v(36.57, 85.5) * mm, "end": v(37.58, 85.09) * mm});
            skArc(sketch, "E169.filletArc", {"start": v(28.22, 94.45) * mm, "mid": v(28.64, 93.44) * mm, "end": v(29.64, 93.03) * mm});
            skArc(sketch, "E170", {"start": v(36.16, 91.08) * mm, "mid": v(35.76, 92.29) * mm, "end": v(34.72, 93.03) * mm});
            skLineSegment(sketch, "E171.bottom", {"start": v(22.43, 100.58) * mm, "end": v(35.13, 100.58) * mm});
            skLineSegment(sketch, "E171.top", {"start": v(22.43, 113.28) * mm, "end": v(25.77, 113.28) * mm});
            skLineSegment(sketch, "E171.left", {"start": v(22.43, 100.58) * mm, "end": v(22.43, 113.28) * mm});
            skLineSegment(sketch, "E171.right", {"start": v(35.13, 100.58) * mm, "end": v(35.13, 103.92) * mm});
            skLineSegment(sketch, "E172.0", {"start": v(27.2, 107.3) * mm, "end": v(27.2, 111.86) * mm});
            skLineSegment(sketch, "E172.1", {"start": v(28.63, 105.34) * mm, "end": v(33.71, 105.34) * mm});
            skArc(sketch, "E173.filletArc", {"start": v(27.2, 111.86) * mm, "mid": v(26.78, 112.87) * mm, "end": v(25.77, 113.28) * mm});
            skArc(sketch, "E174.filletArc", {"start": v(35.13, 103.92) * mm, "mid": v(34.71, 104.93) * mm, "end": v(33.71, 105.34) * mm});
            skArc(sketch, "E175", {"start": v(27.2, 107.3) * mm, "mid": v(27.59, 106.08) * mm, "end": v(28.63, 105.34) * mm});
            skLineSegment(sketch, "E176.bottom", {"start": v(40.86, 111.69) * mm, "end": v(28.16, 111.69) * mm});
            skLineSegment(sketch, "E176.top", {"start": v(40.86, 98.99) * mm, "end": v(37.51, 98.99) * mm});
            skLineSegment(sketch, "E176.left", {"start": v(40.86, 111.69) * mm, "end": v(40.86, 98.99) * mm});
            skLineSegment(sketch, "E176.right", {"start": v(28.16, 111.69) * mm, "end": v(28.16, 108.34) * mm});
            skLineSegment(sketch, "E177.0", {"start": v(36.1, 104.98) * mm, "end": v(36.1, 100.4) * mm});
            skLineSegment(sketch, "E177.1", {"start": v(34.66, 106.93) * mm, "end": v(29.58, 106.93) * mm});
            skArc(sketch, "E178.filletArc", {"start": v(36.1, 100.4) * mm, "mid": v(36.51, 99.4) * mm, "end": v(37.51, 98.99) * mm});
            skArc(sketch, "E179.filletArc", {"start": v(28.16, 108.34) * mm, "mid": v(28.57, 107.34) * mm, "end": v(29.58, 106.93) * mm});
            skArc(sketch, "E180", {"start": v(36.1, 104.98) * mm, "mid": v(35.7, 106.19) * mm, "end": v(34.66, 106.93) * mm});
            skLineSegment(sketch, "E181.bottom", {"start": v(22.56, 114.53) * mm, "end": v(35.26, 114.53) * mm});
            skLineSegment(sketch, "E181.top", {"start": v(22.56, 127.23) * mm, "end": v(25.9, 127.23) * mm});
            skLineSegment(sketch, "E181.left", {"start": v(22.56, 114.53) * mm, "end": v(22.56, 127.23) * mm});
            skLineSegment(sketch, "E181.right", {"start": v(35.26, 114.53) * mm, "end": v(35.26, 117.88) * mm});
            skLineSegment(sketch, "E182.0", {"start": v(27.33, 121.24) * mm, "end": v(27.33, 125.81) * mm});
            skLineSegment(sketch, "E182.1", {"start": v(28.76, 119.3) * mm, "end": v(33.84, 119.3) * mm});
            skArc(sketch, "E183.filletArc", {"start": v(27.33, 125.81) * mm, "mid": v(26.91, 126.82) * mm, "end": v(25.9, 127.23) * mm});
            skArc(sketch, "E184.filletArc", {"start": v(35.26, 117.88) * mm, "mid": v(34.85, 118.88) * mm, "end": v(33.84, 119.3) * mm});
            skArc(sketch, "E185", {"start": v(27.33, 121.24) * mm, "mid": v(27.72, 120.03) * mm, "end": v(28.76, 119.3) * mm});
            skLineSegment(sketch, "E186.bottom", {"start": v(41, 125.64) * mm, "end": v(28.3, 125.64) * mm});
            skLineSegment(sketch, "E186.top", {"start": v(41, 112.94) * mm, "end": v(37.65, 112.94) * mm});
            skLineSegment(sketch, "E186.left", {"start": v(41, 125.64) * mm, "end": v(41, 112.94) * mm});
            skLineSegment(sketch, "E186.right", {"start": v(28.3, 125.64) * mm, "end": v(28.3, 122.3) * mm});
            skLineSegment(sketch, "E187.0", {"start": v(36.23, 118.93) * mm, "end": v(36.23, 114.36) * mm});
            skLineSegment(sketch, "E187.1", {"start": v(34.8, 120.88) * mm, "end": v(29.71, 120.88) * mm});
            skArc(sketch, "E188.filletArc", {"start": v(36.23, 114.36) * mm, "mid": v(36.65, 113.36) * mm, "end": v(37.65, 112.94) * mm});
            skArc(sketch, "E189.filletArc", {"start": v(28.3, 122.3) * mm, "mid": v(28.7, 121.3) * mm, "end": v(29.71, 120.88) * mm});
            skArc(sketch, "E190", {"start": v(36.23, 118.93) * mm, "mid": v(35.83, 120.14) * mm, "end": v(34.8, 120.88) * mm});
            skLineSegment(sketch, "E191.bottom", {"start": v(22.91, 128.27) * mm, "end": v(35.61, 128.27) * mm});
            skLineSegment(sketch, "E191.top", {"start": v(22.91, 140.97) * mm, "end": v(26.26, 140.97) * mm});
            skLineSegment(sketch, "E191.left", {"start": v(22.91, 128.27) * mm, "end": v(22.91, 140.97) * mm});
            skLineSegment(sketch, "E191.right", {"start": v(35.61, 128.27) * mm, "end": v(35.61, 131.61) * mm});
            skLineSegment(sketch, "E192.0", {"start": v(27.68, 134.98) * mm, "end": v(27.68, 139.55) * mm});
            skLineSegment(sketch, "E192.1", {"start": v(29.11, 133.03) * mm, "end": v(34.2, 133.03) * mm});
            skArc(sketch, "E193.filletArc", {"start": v(27.68, 139.55) * mm, "mid": v(27.26, 140.55) * mm, "end": v(26.26, 140.97) * mm});
            skArc(sketch, "E194.filletArc", {"start": v(35.61, 131.61) * mm, "mid": v(35.2, 132.62) * mm, "end": v(34.2, 133.03) * mm});
            skArc(sketch, "E195", {"start": v(27.68, 134.98) * mm, "mid": v(28.07, 133.77) * mm, "end": v(29.11, 133.03) * mm});
            skLineSegment(sketch, "E196.bottom", {"start": v(41.34, 139.38) * mm, "end": v(28.64, 139.38) * mm});
            skLineSegment(sketch, "E196.top", {"start": v(41.34, 126.68) * mm, "end": v(38, 126.68) * mm});
            skLineSegment(sketch, "E196.left", {"start": v(41.34, 139.38) * mm, "end": v(41.34, 126.68) * mm});
            skLineSegment(sketch, "E196.right", {"start": v(28.64, 139.38) * mm, "end": v(28.64, 136.03) * mm});
            skLineSegment(sketch, "E197.0", {"start": v(36.58, 132.67) * mm, "end": v(36.58, 128.1) * mm});
            skLineSegment(sketch, "E197.1", {"start": v(35.15, 134.61) * mm, "end": v(30.06, 134.61) * mm});
            skArc(sketch, "E198.filletArc", {"start": v(36.58, 128.1) * mm, "mid": v(37, 127.1) * mm, "end": v(38, 126.68) * mm});
            skArc(sketch, "E199.filletArc", {"start": v(28.64, 136.03) * mm, "mid": v(29.06, 135.03) * mm, "end": v(30.06, 134.61) * mm});
            skArc(sketch, "E200", {"start": v(36.58, 132.67) * mm, "mid": v(36.18, 133.88) * mm, "end": v(35.15, 134.61) * mm});
            skLineSegment(sketch, "E201.bottom", {"start": v(45.04, 2.9) * mm, "end": v(57.74, 2.9) * mm});
            skLineSegment(sketch, "E201.top", {"start": v(45.04, 15.6) * mm, "end": v(48.38, 15.6) * mm});
            skLineSegment(sketch, "E201.left", {"start": v(45.04, 2.9) * mm, "end": v(45.04, 15.6) * mm});
            skLineSegment(sketch, "E201.right", {"start": v(57.74, 2.9) * mm, "end": v(57.74, 6.24) * mm});
            skLineSegment(sketch, "E202.0", {"start": v(49.8, 9.6) * mm, "end": v(49.8, 14.17) * mm});
            skLineSegment(sketch, "E202.1", {"start": v(51.23, 7.66) * mm, "end": v(56.32, 7.66) * mm});
            skArc(sketch, "E203.filletArc", {"start": v(49.8, 14.17) * mm, "mid": v(49.38, 15.18) * mm, "end": v(48.38, 15.6) * mm});
            skArc(sketch, "E204.filletArc", {"start": v(57.74, 6.24) * mm, "mid": v(57.32, 7.24) * mm, "end": v(56.32, 7.66) * mm});
            skArc(sketch, "E205", {"start": v(49.8, 9.6) * mm, "mid": v(50.2, 8.4) * mm, "end": v(51.23, 7.66) * mm});
            skLineSegment(sketch, "E206.bottom", {"start": v(63.46, 14) * mm, "end": v(50.76, 14) * mm});
            skLineSegment(sketch, "E206.top", {"start": v(63.46, 1.3) * mm, "end": v(60.12, 1.3) * mm});
            skLineSegment(sketch, "E206.left", {"start": v(63.46, 14) * mm, "end": v(63.46, 1.3) * mm});
            skLineSegment(sketch, "E206.right", {"start": v(50.76, 14) * mm, "end": v(50.76, 10.66) * mm});
            skLineSegment(sketch, "E207.0", {"start": v(58.7, 7.3) * mm, "end": v(58.7, 2.72) * mm});
            skLineSegment(sketch, "E207.1", {"start": v(57.27, 9.24) * mm, "end": v(52.18, 9.24) * mm});
            skArc(sketch, "E208.filletArc", {"start": v(58.7, 2.72) * mm, "mid": v(59.12, 1.72) * mm, "end": v(60.12, 1.3) * mm});
            skArc(sketch, "E209.filletArc", {"start": v(50.76, 10.66) * mm, "mid": v(51.18, 9.65) * mm, "end": v(52.18, 9.24) * mm});
            skArc(sketch, "E210", {"start": v(58.7, 7.3) * mm, "mid": v(58.3, 8.5) * mm, "end": v(57.27, 9.24) * mm});
            skLineSegment(sketch, "E211.bottom", {"start": v(45.06, 16.86) * mm, "end": v(57.76, 16.86) * mm});
            skLineSegment(sketch, "E211.top", {"start": v(45.06, 29.56) * mm, "end": v(48.4, 29.56) * mm});
            skLineSegment(sketch, "E211.left", {"start": v(45.06, 16.86) * mm, "end": v(45.06, 29.56) * mm});
            skLineSegment(sketch, "E211.right", {"start": v(57.76, 16.86) * mm, "end": v(57.76, 20.2) * mm});
            skLineSegment(sketch, "E212.0", {"start": v(49.82, 23.57) * mm, "end": v(49.82, 28.14) * mm});
            skLineSegment(sketch, "E212.1", {"start": v(51.25, 21.63) * mm, "end": v(56.34, 21.63) * mm});
            skArc(sketch, "E213.filletArc", {"start": v(49.82, 28.14) * mm, "mid": v(49.4, 29.15) * mm, "end": v(48.4, 29.56) * mm});
            skArc(sketch, "E214.filletArc", {"start": v(57.76, 20.2) * mm, "mid": v(57.34, 21.21) * mm, "end": v(56.34, 21.63) * mm});
            skArc(sketch, "E215", {"start": v(49.82, 23.57) * mm, "mid": v(50.22, 22.37) * mm, "end": v(51.25, 21.63) * mm});
            skLineSegment(sketch, "E216.bottom", {"start": v(63.49, 27.97) * mm, "end": v(50.79, 27.97) * mm});
            skLineSegment(sketch, "E216.top", {"start": v(63.49, 15.27) * mm, "end": v(60.14, 15.27) * mm});
            skLineSegment(sketch, "E216.left", {"start": v(63.49, 27.97) * mm, "end": v(63.49, 15.27) * mm});
            skLineSegment(sketch, "E216.right", {"start": v(50.79, 27.97) * mm, "end": v(50.79, 24.63) * mm});
            skLineSegment(sketch, "E217.0", {"start": v(58.72, 21.26) * mm, "end": v(58.72, 16.7) * mm});
            skLineSegment(sketch, "E217.1", {"start": v(57.29, 23.2) * mm, "end": v(52.2, 23.2) * mm});
            skArc(sketch, "E218.filletArc", {"start": v(58.72, 16.7) * mm, "mid": v(59.14, 15.69) * mm, "end": v(60.14, 15.27) * mm});
            skArc(sketch, "E219.filletArc", {"start": v(50.79, 24.63) * mm, "mid": v(51.2, 23.62) * mm, "end": v(52.2, 23.2) * mm});
            skArc(sketch, "E220", {"start": v(58.72, 21.26) * mm, "mid": v(58.33, 22.47) * mm, "end": v(57.29, 23.2) * mm});
            skLineSegment(sketch, "E221.bottom", {"start": v(45, 30.8) * mm, "end": v(57.7, 30.8) * mm});
            skLineSegment(sketch, "E221.top", {"start": v(45, 43.5) * mm, "end": v(48.35, 43.5) * mm});
            skLineSegment(sketch, "E221.left", {"start": v(45, 30.8) * mm, "end": v(45, 43.5) * mm});
            skLineSegment(sketch, "E221.right", {"start": v(57.7, 30.8) * mm, "end": v(57.7, 34.14) * mm});
            skLineSegment(sketch, "E222.0", {"start": v(49.77, 37.5) * mm, "end": v(49.77, 42.07) * mm});
            skLineSegment(sketch, "E222.1", {"start": v(51.2, 35.56) * mm, "end": v(56.29, 35.56) * mm});
            skArc(sketch, "E223.filletArc", {"start": v(49.77, 42.07) * mm, "mid": v(49.35, 43.08) * mm, "end": v(48.35, 43.5) * mm});
            skArc(sketch, "E224.filletArc", {"start": v(57.7, 34.14) * mm, "mid": v(57.3, 35.14) * mm, "end": v(56.29, 35.56) * mm});
            skArc(sketch, "E225", {"start": v(49.77, 37.5) * mm, "mid": v(50.17, 36.3) * mm, "end": v(51.2, 35.56) * mm});
            skLineSegment(sketch, "E226.bottom", {"start": v(63.43, 41.9) * mm, "end": v(50.73, 41.9) * mm});
            skLineSegment(sketch, "E226.top", {"start": v(63.43, 29.2) * mm, "end": v(60.1, 29.2) * mm});
            skLineSegment(sketch, "E226.left", {"start": v(63.43, 41.9) * mm, "end": v(63.43, 29.2) * mm});
            skLineSegment(sketch, "E226.right", {"start": v(50.73, 41.9) * mm, "end": v(50.73, 38.56) * mm});
            skLineSegment(sketch, "E227.0", {"start": v(58.67, 35.19) * mm, "end": v(58.67, 30.62) * mm});
            skLineSegment(sketch, "E227.1", {"start": v(57.24, 37.14) * mm, "end": v(52.15, 37.14) * mm});
            skArc(sketch, "E228.filletArc", {"start": v(58.67, 30.62) * mm, "mid": v(59.09, 29.62) * mm, "end": v(60.1, 29.2) * mm});
            skArc(sketch, "E229.filletArc", {"start": v(50.73, 38.56) * mm, "mid": v(51.15, 37.55) * mm, "end": v(52.15, 37.14) * mm});
            skArc(sketch, "E230", {"start": v(58.67, 35.19) * mm, "mid": v(58.28, 36.4) * mm, "end": v(57.24, 37.14) * mm});
            skLineSegment(sketch, "E231.bottom", {"start": v(45, 45.02) * mm, "end": v(57.7, 45.02) * mm});
            skLineSegment(sketch, "E231.top", {"start": v(45, 57.72) * mm, "end": v(48.35, 57.72) * mm});
            skLineSegment(sketch, "E231.left", {"start": v(45, 45.02) * mm, "end": v(45, 57.72) * mm});
            skLineSegment(sketch, "E231.right", {"start": v(57.7, 45.02) * mm, "end": v(57.7, 48.36) * mm});
            skLineSegment(sketch, "E232.0", {"start": v(49.77, 51.73) * mm, "end": v(49.77, 56.3) * mm});
            skLineSegment(sketch, "E232.1", {"start": v(51.2, 49.78) * mm, "end": v(56.29, 49.78) * mm});
            skArc(sketch, "E233.filletArc", {"start": v(49.77, 56.3) * mm, "mid": v(49.35, 57.3) * mm, "end": v(48.35, 57.72) * mm});
            skArc(sketch, "E234.filletArc", {"start": v(57.7, 48.36) * mm, "mid": v(57.3, 49.36) * mm, "end": v(56.29, 49.78) * mm});
            skArc(sketch, "E235", {"start": v(49.77, 51.73) * mm, "mid": v(50.17, 50.52) * mm, "end": v(51.2, 49.78) * mm});
            skLineSegment(sketch, "E236.bottom", {"start": v(63.43, 56.12) * mm, "end": v(50.73, 56.12) * mm});
            skLineSegment(sketch, "E236.top", {"start": v(63.43, 43.42) * mm, "end": v(60.1, 43.42) * mm});
            skLineSegment(sketch, "E236.left", {"start": v(63.43, 56.12) * mm, "end": v(63.43, 43.42) * mm});
            skLineSegment(sketch, "E236.right", {"start": v(50.73, 56.12) * mm, "end": v(50.73, 52.78) * mm});
            skLineSegment(sketch, "E237.0", {"start": v(58.67, 49.41) * mm, "end": v(58.67, 44.84) * mm});
            skLineSegment(sketch, "E237.1", {"start": v(57.24, 51.36) * mm, "end": v(52.15, 51.36) * mm});
            skArc(sketch, "E238.filletArc", {"start": v(58.67, 44.84) * mm, "mid": v(59.09, 43.84) * mm, "end": v(60.1, 43.42) * mm});
            skArc(sketch, "E239.filletArc", {"start": v(50.73, 52.78) * mm, "mid": v(51.15, 51.78) * mm, "end": v(52.15, 51.36) * mm});
            skArc(sketch, "E240", {"start": v(58.67, 49.41) * mm, "mid": v(58.28, 50.62) * mm, "end": v(57.24, 51.36) * mm});
            skLineSegment(sketch, "E241.bottom", {"start": v(44.76, 58.78) * mm, "end": v(57.46, 58.78) * mm});
            skLineSegment(sketch, "E241.top", {"start": v(44.76, 71.48) * mm, "end": v(48.1, 71.48) * mm});
            skLineSegment(sketch, "E241.left", {"start": v(44.76, 58.78) * mm, "end": v(44.76, 71.48) * mm});
            skLineSegment(sketch, "E241.right", {"start": v(57.46, 58.78) * mm, "end": v(57.46, 62.13) * mm});
            skLineSegment(sketch, "E242.0", {"start": v(49.52, 65.5) * mm, "end": v(49.52, 70.07) * mm});
            skLineSegment(sketch, "E242.1", {"start": v(50.95, 63.55) * mm, "end": v(56.04, 63.55) * mm});
            skArc(sketch, "E243.filletArc", {"start": v(49.52, 70.07) * mm, "mid": v(49.1, 71.07) * mm, "end": v(48.1, 71.48) * mm});
            skArc(sketch, "E244.filletArc", {"start": v(57.46, 62.13) * mm, "mid": v(57.04, 63.13) * mm, "end": v(56.04, 63.55) * mm});
            skArc(sketch, "E245", {"start": v(49.52, 65.5) * mm, "mid": v(49.92, 64.29) * mm, "end": v(50.95, 63.55) * mm});
            skLineSegment(sketch, "E246.bottom", {"start": v(63.18, 69.9) * mm, "end": v(50.48, 69.9) * mm});
            skLineSegment(sketch, "E246.top", {"start": v(63.18, 57.2) * mm, "end": v(59.84, 57.2) * mm});
            skLineSegment(sketch, "E246.left", {"start": v(63.18, 69.9) * mm, "end": v(63.18, 57.2) * mm});
            skLineSegment(sketch, "E246.right", {"start": v(50.48, 69.9) * mm, "end": v(50.48, 66.55) * mm});
            skLineSegment(sketch, "E247.0", {"start": v(58.42, 63.18) * mm, "end": v(58.42, 58.61) * mm});
            skLineSegment(sketch, "E247.1", {"start": v(56.99, 65.13) * mm, "end": v(51.9, 65.13) * mm});
            skArc(sketch, "E248.filletArc", {"start": v(58.42, 58.61) * mm, "mid": v(58.84, 57.6) * mm, "end": v(59.84, 57.2) * mm});
            skArc(sketch, "E249.filletArc", {"start": v(50.48, 66.55) * mm, "mid": v(50.9, 65.55) * mm, "end": v(51.9, 65.13) * mm});
            skArc(sketch, "E250", {"start": v(58.42, 63.18) * mm, "mid": v(58.02, 64.4) * mm, "end": v(56.99, 65.13) * mm});
            skLineSegment(sketch, "E251.bottom", {"start": v(44.42, 72.87) * mm, "end": v(57.12, 72.87) * mm});
            skLineSegment(sketch, "E251.top", {"start": v(44.42, 85.57) * mm, "end": v(47.76, 85.57) * mm});
            skLineSegment(sketch, "E251.left", {"start": v(44.42, 72.87) * mm, "end": v(44.42, 85.57) * mm});
            skLineSegment(sketch, "E251.right", {"start": v(57.12, 72.87) * mm, "end": v(57.12, 76.21) * mm});
            skLineSegment(sketch, "E252.0", {"start": v(49.18, 79.58) * mm, "end": v(49.18, 84.15) * mm});
            skLineSegment(sketch, "E252.1", {"start": v(50.61, 77.63) * mm, "end": v(55.7, 77.63) * mm});
            skArc(sketch, "E253.filletArc", {"start": v(49.18, 84.15) * mm, "mid": v(48.76, 85.15) * mm, "end": v(47.76, 85.57) * mm});
            skArc(sketch, "E254.filletArc", {"start": v(57.12, 76.21) * mm, "mid": v(56.7, 77.22) * mm, "end": v(55.7, 77.63) * mm});
            skArc(sketch, "E255", {"start": v(49.18, 79.58) * mm, "mid": v(49.58, 78.37) * mm, "end": v(50.61, 77.63) * mm});
            skLineSegment(sketch, "E256.bottom", {"start": v(62.84, 83.98) * mm, "end": v(50.14, 83.98) * mm});
            skLineSegment(sketch, "E256.top", {"start": v(62.84, 71.28) * mm, "end": v(59.5, 71.28) * mm});
            skLineSegment(sketch, "E256.left", {"start": v(62.84, 83.98) * mm, "end": v(62.84, 71.28) * mm});
            skLineSegment(sketch, "E256.right", {"start": v(50.14, 83.98) * mm, "end": v(50.14, 80.63) * mm});
            skLineSegment(sketch, "E257.0", {"start": v(58.08, 77.27) * mm, "end": v(58.08, 72.7) * mm});
            skLineSegment(sketch, "E257.1", {"start": v(56.65, 79.21) * mm, "end": v(51.56, 79.21) * mm});
            skArc(sketch, "E258.filletArc", {"start": v(58.08, 72.7) * mm, "mid": v(58.5, 71.7) * mm, "end": v(59.5, 71.28) * mm});
            skArc(sketch, "E259.filletArc", {"start": v(50.14, 80.63) * mm, "mid": v(50.56, 79.63) * mm, "end": v(51.56, 79.21) * mm});
            skArc(sketch, "E260", {"start": v(58.08, 77.27) * mm, "mid": v(57.68, 78.48) * mm, "end": v(56.65, 79.21) * mm});
            skLineSegment(sketch, "E261.bottom", {"start": v(44.23, 86.76) * mm, "end": v(56.93, 86.76) * mm});
            skLineSegment(sketch, "E261.top", {"start": v(44.23, 99.46) * mm, "end": v(47.57, 99.46) * mm});
            skLineSegment(sketch, "E261.left", {"start": v(44.23, 86.76) * mm, "end": v(44.23, 99.46) * mm});
            skLineSegment(sketch, "E261.right", {"start": v(56.93, 86.76) * mm, "end": v(56.93, 90.1) * mm});
            skLineSegment(sketch, "E262.0", {"start": v(48.99, 93.47) * mm, "end": v(48.99, 98.04) * mm});
            skLineSegment(sketch, "E262.1", {"start": v(50.42, 91.52) * mm, "end": v(55.5, 91.52) * mm});
            skArc(sketch, "E263.filletArc", {"start": v(48.99, 98.04) * mm, "mid": v(48.57, 99.04) * mm, "end": v(47.57, 99.46) * mm});
            skArc(sketch, "E264.filletArc", {"start": v(56.93, 90.1) * mm, "mid": v(56.5, 91.1) * mm, "end": v(55.5, 91.52) * mm});
            skArc(sketch, "E265", {"start": v(48.99, 93.47) * mm, "mid": v(49.39, 92.26) * mm, "end": v(50.42, 91.52) * mm});
            skLineSegment(sketch, "E266.bottom", {"start": v(62.65, 97.87) * mm, "end": v(49.95, 97.87) * mm});
            skLineSegment(sketch, "E266.top", {"start": v(62.65, 85.17) * mm, "end": v(59.31, 85.17) * mm});
            skLineSegment(sketch, "E266.left", {"start": v(62.65, 97.87) * mm, "end": v(62.65, 85.17) * mm});
            skLineSegment(sketch, "E266.right", {"start": v(49.95, 97.87) * mm, "end": v(49.95, 94.52) * mm});
            skLineSegment(sketch, "E267.0", {"start": v(57.9, 91.15) * mm, "end": v(57.9, 86.58) * mm});
            skLineSegment(sketch, "E267.1", {"start": v(56.46, 93.1) * mm, "end": v(51.37, 93.1) * mm});
            skArc(sketch, "E268.filletArc", {"start": v(57.9, 86.58) * mm, "mid": v(58.3, 85.58) * mm, "end": v(59.31, 85.17) * mm});
            skArc(sketch, "E269.filletArc", {"start": v(49.95, 94.52) * mm, "mid": v(50.37, 93.52) * mm, "end": v(51.37, 93.1) * mm});
            skArc(sketch, "E270", {"start": v(57.9, 91.15) * mm, "mid": v(57.5, 92.36) * mm, "end": v(56.46, 93.1) * mm});
            skLineSegment(sketch, "E271.bottom", {"start": v(44.16, 100.66) * mm, "end": v(56.86, 100.66) * mm});
            skLineSegment(sketch, "E271.top", {"start": v(44.16, 113.36) * mm, "end": v(47.5, 113.36) * mm});
            skLineSegment(sketch, "E271.left", {"start": v(44.16, 100.66) * mm, "end": v(44.16, 113.36) * mm});
            skLineSegment(sketch, "E271.right", {"start": v(56.86, 100.66) * mm, "end": v(56.86, 104) * mm});
            skLineSegment(sketch, "E272.0", {"start": v(48.93, 107.37) * mm, "end": v(48.93, 111.94) * mm});
            skLineSegment(sketch, "E272.1", {"start": v(50.36, 105.42) * mm, "end": v(55.44, 105.42) * mm});
            skArc(sketch, "E273.filletArc", {"start": v(48.93, 111.94) * mm, "mid": v(48.5, 112.94) * mm, "end": v(47.5, 113.36) * mm});
            skArc(sketch, "E274.filletArc", {"start": v(56.86, 104) * mm, "mid": v(56.45, 105) * mm, "end": v(55.44, 105.42) * mm});
            skArc(sketch, "E275", {"start": v(48.93, 107.37) * mm, "mid": v(49.32, 106.16) * mm, "end": v(50.36, 105.42) * mm});
            skLineSegment(sketch, "E276.bottom", {"start": v(62.6, 111.76) * mm, "end": v(49.9, 111.76) * mm});
            skLineSegment(sketch, "E276.top", {"start": v(62.6, 99.06) * mm, "end": v(59.25, 99.06) * mm});
            skLineSegment(sketch, "E276.left", {"start": v(62.6, 111.76) * mm, "end": v(62.6, 99.06) * mm});
            skLineSegment(sketch, "E276.right", {"start": v(49.9, 111.76) * mm, "end": v(49.9, 108.42) * mm});
            skLineSegment(sketch, "E277.0", {"start": v(57.83, 105.05) * mm, "end": v(57.83, 100.48) * mm});
            skLineSegment(sketch, "E277.1", {"start": v(56.4, 107) * mm, "end": v(51.3, 107) * mm});
            skArc(sketch, "E278.filletArc", {"start": v(57.83, 100.48) * mm, "mid": v(58.24, 99.48) * mm, "end": v(59.25, 99.06) * mm});
            skArc(sketch, "E279.filletArc", {"start": v(49.9, 108.42) * mm, "mid": v(50.3, 107.42) * mm, "end": v(51.3, 107) * mm});
            skArc(sketch, "E280", {"start": v(57.83, 105.05) * mm, "mid": v(57.43, 106.26) * mm, "end": v(56.4, 107) * mm});
            skLineSegment(sketch, "E281.bottom", {"start": v(44.3, 114.6) * mm, "end": v(57, 114.6) * mm});
            skLineSegment(sketch, "E281.top", {"start": v(44.3, 127.3) * mm, "end": v(47.64, 127.3) * mm});
            skLineSegment(sketch, "E281.left", {"start": v(44.3, 114.6) * mm, "end": v(44.3, 127.3) * mm});
            skLineSegment(sketch, "E281.right", {"start": v(57, 114.6) * mm, "end": v(57, 117.95) * mm});
            skLineSegment(sketch, "E282.0", {"start": v(49.06, 121.32) * mm, "end": v(49.06, 125.9) * mm});
            skLineSegment(sketch, "E282.1", {"start": v(50.5, 119.37) * mm, "end": v(55.58, 119.37) * mm});
            skArc(sketch, "E283.filletArc", {"start": v(49.06, 125.9) * mm, "mid": v(48.64, 126.9) * mm, "end": v(47.64, 127.3) * mm});
            skArc(sketch, "E284.filletArc", {"start": v(57, 117.95) * mm, "mid": v(56.58, 118.96) * mm, "end": v(55.58, 119.37) * mm});
            skArc(sketch, "E285", {"start": v(49.06, 121.32) * mm, "mid": v(49.46, 120.11) * mm, "end": v(50.5, 119.37) * mm});
            skLineSegment(sketch, "E286.bottom", {"start": v(62.72, 125.72) * mm, "end": v(50.02, 125.72) * mm});
            skLineSegment(sketch, "E286.top", {"start": v(62.72, 113.02) * mm, "end": v(59.38, 113.02) * mm});
            skLineSegment(sketch, "E286.left", {"start": v(62.72, 125.72) * mm, "end": v(62.72, 113.02) * mm});
            skLineSegment(sketch, "E286.right", {"start": v(50.02, 125.72) * mm, "end": v(50.02, 122.37) * mm});
            skLineSegment(sketch, "E287.0", {"start": v(57.96, 119) * mm, "end": v(57.96, 114.44) * mm});
            skLineSegment(sketch, "E287.1", {"start": v(56.53, 120.95) * mm, "end": v(51.44, 120.95) * mm});
            skArc(sketch, "E288.filletArc", {"start": v(57.96, 114.44) * mm, "mid": v(58.38, 113.43) * mm, "end": v(59.38, 113.02) * mm});
            skArc(sketch, "E289.filletArc", {"start": v(50.02, 122.37) * mm, "mid": v(50.44, 121.37) * mm, "end": v(51.44, 120.95) * mm});
            skArc(sketch, "E290", {"start": v(57.96, 119) * mm, "mid": v(57.56, 120.22) * mm, "end": v(56.53, 120.95) * mm});
            skLineSegment(sketch, "E291.bottom", {"start": v(44.65, 128.35) * mm, "end": v(57.35, 128.35) * mm});
            skLineSegment(sketch, "E291.top", {"start": v(44.65, 141.05) * mm, "end": v(48, 141.05) * mm});
            skLineSegment(sketch, "E291.left", {"start": v(44.65, 128.35) * mm, "end": v(44.65, 141.05) * mm});
            skLineSegment(sketch, "E291.right", {"start": v(57.35, 128.35) * mm, "end": v(57.35, 131.7) * mm});
            skLineSegment(sketch, "E292.0", {"start": v(49.4, 135.06) * mm, "end": v(49.4, 139.63) * mm});
            skLineSegment(sketch, "E292.1", {"start": v(50.84, 133.1) * mm, "end": v(55.93, 133.1) * mm});
            skArc(sketch, "E293.filletArc", {"start": v(49.4, 139.63) * mm, "mid": v(49, 140.63) * mm, "end": v(48, 141.05) * mm});
            skArc(sketch, "E294.filletArc", {"start": v(57.35, 131.7) * mm, "mid": v(56.93, 132.7) * mm, "end": v(55.93, 133.1) * mm});
            skArc(sketch, "E295", {"start": v(49.4, 135.06) * mm, "mid": v(49.8, 133.85) * mm, "end": v(50.84, 133.1) * mm});
            skLineSegment(sketch, "E296.bottom", {"start": v(63.07, 139.45) * mm, "end": v(50.37, 139.45) * mm});
            skLineSegment(sketch, "E296.top", {"start": v(63.07, 126.75) * mm, "end": v(59.73, 126.75) * mm});
            skLineSegment(sketch, "E296.left", {"start": v(63.07, 139.45) * mm, "end": v(63.07, 126.75) * mm});
            skLineSegment(sketch, "E296.right", {"start": v(50.37, 139.45) * mm, "end": v(50.37, 136.11) * mm});
            skLineSegment(sketch, "E297.0", {"start": v(58.31, 132.74) * mm, "end": v(58.31, 128.17) * mm});
            skLineSegment(sketch, "E297.1", {"start": v(56.88, 134.7) * mm, "end": v(51.8, 134.7) * mm});
            skArc(sketch, "E298.filletArc", {"start": v(58.31, 128.17) * mm, "mid": v(58.73, 127.17) * mm, "end": v(59.73, 126.75) * mm});
            skArc(sketch, "E299.filletArc", {"start": v(50.37, 136.11) * mm, "mid": v(50.8, 135.1) * mm, "end": v(51.8, 134.7) * mm});
            skArc(sketch, "E300", {"start": v(58.31, 132.74) * mm, "mid": v(57.92, 133.95) * mm, "end": v(56.88, 134.7) * mm});
            skLineSegment(sketch, "E301.bottom", {"start": v(66.93, 3.56) * mm, "end": v(79.63, 3.56) * mm});
            skLineSegment(sketch, "E301.top", {"start": v(66.93, 16.26) * mm, "end": v(70.27, 16.26) * mm});
            skLineSegment(sketch, "E301.left", {"start": v(66.93, 3.56) * mm, "end": v(66.93, 16.26) * mm});
            skLineSegment(sketch, "E301.right", {"start": v(79.63, 3.56) * mm, "end": v(79.63, 6.9) * mm});
            skLineSegment(sketch, "E302.0", {"start": v(71.7, 10.27) * mm, "end": v(71.7, 14.84) * mm});
            skLineSegment(sketch, "E302.1", {"start": v(73.12, 8.32) * mm, "end": v(78.2, 8.32) * mm});
            skArc(sketch, "E303.filletArc", {"start": v(71.7, 14.84) * mm, "mid": v(71.27, 15.84) * mm, "end": v(70.27, 16.26) * mm});
            skArc(sketch, "E304.filletArc", {"start": v(79.63, 6.9) * mm, "mid": v(79.21, 7.9) * mm, "end": v(78.2, 8.32) * mm});
            skArc(sketch, "E305", {"start": v(71.7, 10.27) * mm, "mid": v(72.09, 9.06) * mm, "end": v(73.12, 8.32) * mm});
            skLineSegment(sketch, "E306.bottom", {"start": v(85.36, 14.66) * mm, "end": v(72.66, 14.66) * mm});
            skLineSegment(sketch, "E306.top", {"start": v(85.36, 1.96) * mm, "end": v(82.01, 1.96) * mm});
            skLineSegment(sketch, "E306.left", {"start": v(85.36, 14.66) * mm, "end": v(85.36, 1.96) * mm});
            skLineSegment(sketch, "E306.right", {"start": v(72.66, 14.66) * mm, "end": v(72.66, 11.32) * mm});
            skLineSegment(sketch, "E307.0", {"start": v(80.6, 7.95) * mm, "end": v(80.6, 3.38) * mm});
            skLineSegment(sketch, "E307.1", {"start": v(79.16, 9.9) * mm, "end": v(74.07, 9.9) * mm});
            skArc(sketch, "E308.filletArc", {"start": v(80.6, 3.38) * mm, "mid": v(81, 2.38) * mm, "end": v(82.01, 1.96) * mm});
            skArc(sketch, "E309.filletArc", {"start": v(72.66, 11.32) * mm, "mid": v(73.07, 10.32) * mm, "end": v(74.07, 9.9) * mm});
            skArc(sketch, "E310", {"start": v(80.6, 7.95) * mm, "mid": v(80.2, 9.16) * mm, "end": v(79.16, 9.9) * mm});
            skLineSegment(sketch, "E311.bottom", {"start": v(66.95, 17.53) * mm, "end": v(79.65, 17.53) * mm});
            skLineSegment(sketch, "E311.top", {"start": v(66.95, 30.23) * mm, "end": v(70.3, 30.23) * mm});
            skLineSegment(sketch, "E311.left", {"start": v(66.95, 17.53) * mm, "end": v(66.95, 30.23) * mm});
            skLineSegment(sketch, "E311.right", {"start": v(79.65, 17.53) * mm, "end": v(79.65, 20.87) * mm});
            skLineSegment(sketch, "E312.0", {"start": v(71.71, 24.24) * mm, "end": v(71.71, 28.8) * mm});
            skLineSegment(sketch, "E312.1", {"start": v(73.15, 22.29) * mm, "end": v(78.23, 22.29) * mm});
            skArc(sketch, "E313.filletArc", {"start": v(71.71, 28.8) * mm, "mid": v(71.3, 29.81) * mm, "end": v(70.3, 30.23) * mm});
            skArc(sketch, "E314.filletArc", {"start": v(79.65, 20.87) * mm, "mid": v(79.23, 21.87) * mm, "end": v(78.23, 22.29) * mm});
            skArc(sketch, "E315", {"start": v(71.71, 24.24) * mm, "mid": v(72.1, 23.03) * mm, "end": v(73.15, 22.29) * mm});
            skLineSegment(sketch, "E316.bottom", {"start": v(85.38, 28.63) * mm, "end": v(72.68, 28.63) * mm});
            skLineSegment(sketch, "E316.top", {"start": v(85.38, 15.93) * mm, "end": v(82.03, 15.93) * mm});
            skLineSegment(sketch, "E316.left", {"start": v(85.38, 28.63) * mm, "end": v(85.38, 15.93) * mm});
            skLineSegment(sketch, "E316.right", {"start": v(72.68, 28.63) * mm, "end": v(72.68, 25.29) * mm});
            skLineSegment(sketch, "E317.0", {"start": v(80.61, 21.92) * mm, "end": v(80.61, 17.35) * mm});
            skLineSegment(sketch, "E317.1", {"start": v(79.18, 23.87) * mm, "end": v(74.1, 23.87) * mm});
            skArc(sketch, "E318.filletArc", {"start": v(80.61, 17.35) * mm, "mid": v(81.03, 16.35) * mm, "end": v(82.03, 15.93) * mm});
            skArc(sketch, "E319.filletArc", {"start": v(72.68, 25.29) * mm, "mid": v(73.1, 24.29) * mm, "end": v(74.1, 23.87) * mm});
            skArc(sketch, "E320", {"start": v(80.61, 21.92) * mm, "mid": v(80.22, 23.13) * mm, "end": v(79.18, 23.87) * mm});
            skLineSegment(sketch, "E321.bottom", {"start": v(66.9, 31.46) * mm, "end": v(79.6, 31.46) * mm});
            skLineSegment(sketch, "E321.top", {"start": v(66.9, 44.16) * mm, "end": v(70.24, 44.16) * mm});
            skLineSegment(sketch, "E321.left", {"start": v(66.9, 31.46) * mm, "end": v(66.9, 44.16) * mm});
            skLineSegment(sketch, "E321.right", {"start": v(79.6, 31.46) * mm, "end": v(79.6, 34.8) * mm});
            skLineSegment(sketch, "E322.0", {"start": v(71.66, 38.17) * mm, "end": v(71.66, 42.74) * mm});
            skLineSegment(sketch, "E322.1", {"start": v(73.1, 36.22) * mm, "end": v(78.18, 36.22) * mm});
            skArc(sketch, "E323.filletArc", {"start": v(71.66, 42.74) * mm, "mid": v(71.24, 43.74) * mm, "end": v(70.24, 44.16) * mm});
            skArc(sketch, "E324.filletArc", {"start": v(79.6, 34.8) * mm, "mid": v(79.18, 35.8) * mm, "end": v(78.18, 36.22) * mm});
            skArc(sketch, "E325", {"start": v(71.66, 38.17) * mm, "mid": v(72.06, 36.96) * mm, "end": v(73.1, 36.22) * mm});
            skLineSegment(sketch, "E326.bottom", {"start": v(85.33, 42.56) * mm, "end": v(72.63, 42.56) * mm});
            skLineSegment(sketch, "E326.top", {"start": v(85.33, 29.86) * mm, "end": v(81.98, 29.86) * mm});
            skLineSegment(sketch, "E326.left", {"start": v(85.33, 42.56) * mm, "end": v(85.33, 29.86) * mm});
            skLineSegment(sketch, "E326.right", {"start": v(72.63, 42.56) * mm, "end": v(72.63, 39.22) * mm});
            skLineSegment(sketch, "E327.0", {"start": v(80.56, 35.85) * mm, "end": v(80.56, 31.28) * mm});
            skLineSegment(sketch, "E327.1", {"start": v(79.13, 37.8) * mm, "end": v(74.05, 37.8) * mm});
            skArc(sketch, "E328.filletArc", {"start": v(80.56, 31.28) * mm, "mid": v(80.98, 30.28) * mm, "end": v(81.98, 29.86) * mm});
            skArc(sketch, "E329.filletArc", {"start": v(72.63, 39.22) * mm, "mid": v(73.04, 38.22) * mm, "end": v(74.05, 37.8) * mm});
            skArc(sketch, "E330", {"start": v(80.56, 35.85) * mm, "mid": v(80.17, 37.06) * mm, "end": v(79.13, 37.8) * mm});
            skLineSegment(sketch, "E331.bottom", {"start": v(66.9, 45.68) * mm, "end": v(79.6, 45.68) * mm});
            skLineSegment(sketch, "E331.top", {"start": v(66.9, 58.38) * mm, "end": v(70.24, 58.38) * mm});
            skLineSegment(sketch, "E331.left", {"start": v(66.9, 45.68) * mm, "end": v(66.9, 58.38) * mm});
            skLineSegment(sketch, "E331.right", {"start": v(79.6, 45.68) * mm, "end": v(79.6, 49.02) * mm});
            skLineSegment(sketch, "E332.0", {"start": v(71.66, 52.4) * mm, "end": v(71.66, 56.96) * mm});
            skLineSegment(sketch, "E332.1", {"start": v(73.1, 50.44) * mm, "end": v(78.18, 50.44) * mm});
            skArc(sketch, "E333.filletArc", {"start": v(71.66, 56.96) * mm, "mid": v(71.24, 57.96) * mm, "end": v(70.24, 58.38) * mm});
            skArc(sketch, "E334.filletArc", {"start": v(79.6, 49.02) * mm, "mid": v(79.18, 50.03) * mm, "end": v(78.18, 50.44) * mm});
            skArc(sketch, "E335", {"start": v(71.66, 52.4) * mm, "mid": v(72.06, 51.18) * mm, "end": v(73.1, 50.44) * mm});
            skLineSegment(sketch, "E336.bottom", {"start": v(85.33, 56.79) * mm, "end": v(72.63, 56.79) * mm});
            skLineSegment(sketch, "E336.top", {"start": v(85.33, 44.09) * mm, "end": v(81.98, 44.09) * mm});
            skLineSegment(sketch, "E336.left", {"start": v(85.33, 56.79) * mm, "end": v(85.33, 44.09) * mm});
            skLineSegment(sketch, "E336.right", {"start": v(72.63, 56.79) * mm, "end": v(72.63, 53.44) * mm});
            skLineSegment(sketch, "E337.0", {"start": v(80.56, 50.08) * mm, "end": v(80.56, 45.5) * mm});
            skLineSegment(sketch, "E337.1", {"start": v(79.13, 52.02) * mm, "end": v(74.05, 52.02) * mm});
            skArc(sketch, "E338.filletArc", {"start": v(80.56, 45.5) * mm, "mid": v(80.98, 44.5) * mm, "end": v(81.98, 44.09) * mm});
            skArc(sketch, "E339.filletArc", {"start": v(72.63, 53.44) * mm, "mid": v(73.04, 52.44) * mm, "end": v(74.05, 52.02) * mm});
            skArc(sketch, "E340", {"start": v(80.56, 50.08) * mm, "mid": v(80.17, 51.29) * mm, "end": v(79.13, 52.02) * mm});
            skLineSegment(sketch, "E341.bottom", {"start": v(66.65, 59.45) * mm, "end": v(79.35, 59.45) * mm});
            skLineSegment(sketch, "E341.top", {"start": v(66.65, 72.15) * mm, "end": v(69.99, 72.15) * mm});
            skLineSegment(sketch, "E341.left", {"start": v(66.65, 59.45) * mm, "end": v(66.65, 72.15) * mm});
            skLineSegment(sketch, "E341.right", {"start": v(79.35, 59.45) * mm, "end": v(79.35, 62.8) * mm});
            skLineSegment(sketch, "E342.0", {"start": v(71.4, 66.16) * mm, "end": v(71.4, 70.73) * mm});
            skLineSegment(sketch, "E342.1", {"start": v(72.84, 64.2) * mm, "end": v(77.93, 64.2) * mm});
            skArc(sketch, "E343.filletArc", {"start": v(71.4, 70.73) * mm, "mid": v(71, 71.73) * mm, "end": v(69.99, 72.15) * mm});
            skArc(sketch, "E344.filletArc", {"start": v(79.35, 62.8) * mm, "mid": v(78.93, 63.8) * mm, "end": v(77.93, 64.2) * mm});
            skArc(sketch, "E345", {"start": v(71.4, 66.16) * mm, "mid": v(71.8, 64.95) * mm, "end": v(72.84, 64.2) * mm});
            skLineSegment(sketch, "E346.bottom", {"start": v(85.07, 70.55) * mm, "end": v(72.37, 70.55) * mm});
            skLineSegment(sketch, "E346.top", {"start": v(85.07, 57.85) * mm, "end": v(81.73, 57.85) * mm});
            skLineSegment(sketch, "E346.left", {"start": v(85.07, 70.55) * mm, "end": v(85.07, 57.85) * mm});
            skLineSegment(sketch, "E346.right", {"start": v(72.37, 70.55) * mm, "end": v(72.37, 67.21) * mm});
            skLineSegment(sketch, "E347.0", {"start": v(80.31, 63.84) * mm, "end": v(80.31, 59.27) * mm});
            skLineSegment(sketch, "E347.1", {"start": v(78.88, 65.8) * mm, "end": v(73.8, 65.8) * mm});
            skArc(sketch, "E348.filletArc", {"start": v(80.31, 59.27) * mm, "mid": v(80.73, 58.27) * mm, "end": v(81.73, 57.85) * mm});
            skArc(sketch, "E349.filletArc", {"start": v(72.37, 67.21) * mm, "mid": v(72.8, 66.2) * mm, "end": v(73.8, 65.8) * mm});
            skArc(sketch, "E350", {"start": v(80.31, 63.84) * mm, "mid": v(79.91, 65.05) * mm, "end": v(78.88, 65.8) * mm});
            skLineSegment(sketch, "E351.bottom", {"start": v(66.3, 73.53) * mm, "end": v(79, 73.53) * mm});
            skLineSegment(sketch, "E351.top", {"start": v(66.3, 86.23) * mm, "end": v(69.65, 86.23) * mm});
            skLineSegment(sketch, "E351.left", {"start": v(66.3, 73.53) * mm, "end": v(66.3, 86.23) * mm});
            skLineSegment(sketch, "E351.right", {"start": v(79, 73.53) * mm, "end": v(79, 76.88) * mm});
            skLineSegment(sketch, "E352.0", {"start": v(71.07, 80.24) * mm, "end": v(71.07, 84.81) * mm});
            skLineSegment(sketch, "E352.1", {"start": v(72.5, 78.3) * mm, "end": v(77.59, 78.3) * mm});
            skArc(sketch, "E353.filletArc", {"start": v(71.07, 84.81) * mm, "mid": v(70.65, 85.82) * mm, "end": v(69.65, 86.23) * mm});
            skArc(sketch, "E354.filletArc", {"start": v(79, 76.88) * mm, "mid": v(78.6, 77.88) * mm, "end": v(77.59, 78.3) * mm});
            skArc(sketch, "E355", {"start": v(71.07, 80.24) * mm, "mid": v(71.47, 79.03) * mm, "end": v(72.5, 78.3) * mm});
            skLineSegment(sketch, "E356.bottom", {"start": v(84.73, 84.64) * mm, "end": v(72.03, 84.64) * mm});
            skLineSegment(sketch, "E356.top", {"start": v(84.73, 71.94) * mm, "end": v(81.4, 71.94) * mm});
            skLineSegment(sketch, "E356.left", {"start": v(84.73, 84.64) * mm, "end": v(84.73, 71.94) * mm});
            skLineSegment(sketch, "E356.right", {"start": v(72.03, 84.64) * mm, "end": v(72.03, 81.3) * mm});
            skLineSegment(sketch, "E357.0", {"start": v(79.97, 77.93) * mm, "end": v(79.97, 73.36) * mm});
            skLineSegment(sketch, "E357.1", {"start": v(78.54, 79.88) * mm, "end": v(73.45, 79.88) * mm});
            skArc(sketch, "E358.filletArc", {"start": v(79.97, 73.36) * mm, "mid": v(80.39, 72.35) * mm, "end": v(81.4, 71.94) * mm});
            skArc(sketch, "E359.filletArc", {"start": v(72.03, 81.3) * mm, "mid": v(72.45, 80.3) * mm, "end": v(73.45, 79.88) * mm});
            skArc(sketch, "E360", {"start": v(79.97, 77.93) * mm, "mid": v(79.58, 79.14) * mm, "end": v(78.54, 79.88) * mm});
            skLineSegment(sketch, "E361.bottom", {"start": v(66.12, 87.42) * mm, "end": v(78.82, 87.42) * mm});
            skLineSegment(sketch, "E361.top", {"start": v(66.12, 100.12) * mm, "end": v(69.46, 100.12) * mm});
            skLineSegment(sketch, "E361.left", {"start": v(66.12, 87.42) * mm, "end": v(66.12, 100.12) * mm});
            skLineSegment(sketch, "E361.right", {"start": v(78.82, 87.42) * mm, "end": v(78.82, 90.76) * mm});
            skLineSegment(sketch, "E362.0", {"start": v(70.88, 94.13) * mm, "end": v(70.88, 98.7) * mm});
            skLineSegment(sketch, "E362.1", {"start": v(72.31, 92.18) * mm, "end": v(77.4, 92.18) * mm});
            skArc(sketch, "E363.filletArc", {"start": v(70.88, 98.7) * mm, "mid": v(70.46, 99.7) * mm, "end": v(69.46, 100.12) * mm});
            skArc(sketch, "E364.filletArc", {"start": v(78.82, 90.76) * mm, "mid": v(78.4, 91.77) * mm, "end": v(77.4, 92.18) * mm});
            skArc(sketch, "E365", {"start": v(70.88, 94.13) * mm, "mid": v(71.28, 92.92) * mm, "end": v(72.31, 92.18) * mm});
            skLineSegment(sketch, "E366.bottom", {"start": v(84.54, 98.53) * mm, "end": v(71.84, 98.53) * mm});
            skLineSegment(sketch, "E366.top", {"start": v(84.54, 85.83) * mm, "end": v(81.2, 85.83) * mm});
            skLineSegment(sketch, "E366.left", {"start": v(84.54, 98.53) * mm, "end": v(84.54, 85.83) * mm});
            skLineSegment(sketch, "E366.right", {"start": v(71.84, 98.53) * mm, "end": v(71.84, 95.18) * mm});
            skLineSegment(sketch, "E367.0", {"start": v(79.78, 91.82) * mm, "end": v(79.78, 87.25) * mm});
            skLineSegment(sketch, "E367.1", {"start": v(78.35, 93.77) * mm, "end": v(73.26, 93.77) * mm});
            skArc(sketch, "E368.filletArc", {"start": v(79.78, 87.25) * mm, "mid": v(80.2, 86.24) * mm, "end": v(81.2, 85.83) * mm});
            skArc(sketch, "E369.filletArc", {"start": v(71.84, 95.18) * mm, "mid": v(72.26, 94.18) * mm, "end": v(73.26, 93.77) * mm});
            skArc(sketch, "E370", {"start": v(79.78, 91.82) * mm, "mid": v(79.39, 93.03) * mm, "end": v(78.35, 93.77) * mm});
            skLineSegment(sketch, "E371.bottom", {"start": v(66.05, 101.32) * mm, "end": v(78.75, 101.32) * mm});
            skLineSegment(sketch, "E371.top", {"start": v(66.05, 114.02) * mm, "end": v(69.4, 114.02) * mm});
            skLineSegment(sketch, "E371.left", {"start": v(66.05, 101.32) * mm, "end": v(66.05, 114.02) * mm});
            skLineSegment(sketch, "E371.right", {"start": v(78.75, 101.32) * mm, "end": v(78.75, 104.66) * mm});
            skLineSegment(sketch, "E372.0", {"start": v(70.82, 108.03) * mm, "end": v(70.82, 112.6) * mm});
            skLineSegment(sketch, "E372.1", {"start": v(72.25, 106.08) * mm, "end": v(77.33, 106.08) * mm});
            skArc(sketch, "E373.filletArc", {"start": v(70.82, 112.6) * mm, "mid": v(70.4, 113.6) * mm, "end": v(69.4, 114.02) * mm});
            skArc(sketch, "E374.filletArc", {"start": v(78.75, 104.66) * mm, "mid": v(78.34, 105.67) * mm, "end": v(77.33, 106.08) * mm});
            skArc(sketch, "E375", {"start": v(70.82, 108.03) * mm, "mid": v(71.21, 106.82) * mm, "end": v(72.25, 106.08) * mm});
            skLineSegment(sketch, "E376.bottom", {"start": v(84.48, 112.43) * mm, "end": v(71.78, 112.43) * mm});
            skLineSegment(sketch, "E376.top", {"start": v(84.48, 99.73) * mm, "end": v(81.14, 99.73) * mm});
            skLineSegment(sketch, "E376.left", {"start": v(84.48, 112.43) * mm, "end": v(84.48, 99.73) * mm});
            skLineSegment(sketch, "E376.right", {"start": v(71.78, 112.43) * mm, "end": v(71.78, 109.08) * mm});
            skLineSegment(sketch, "E377.0", {"start": v(79.72, 105.72) * mm, "end": v(79.72, 101.15) * mm});
            skLineSegment(sketch, "E377.1", {"start": v(78.29, 107.66) * mm, "end": v(73.2, 107.66) * mm});
            skArc(sketch, "E378.filletArc", {"start": v(79.72, 101.15) * mm, "mid": v(80.13, 100.14) * mm, "end": v(81.14, 99.73) * mm});
            skArc(sketch, "E379.filletArc", {"start": v(71.78, 109.08) * mm, "mid": v(72.2, 108.08) * mm, "end": v(73.2, 107.66) * mm});
            skArc(sketch, "E380", {"start": v(79.72, 105.72) * mm, "mid": v(79.32, 106.93) * mm, "end": v(78.29, 107.66) * mm});
            skLineSegment(sketch, "E381.bottom", {"start": v(66.19, 115.27) * mm, "end": v(78.89, 115.27) * mm});
            skLineSegment(sketch, "E381.top", {"start": v(66.19, 127.97) * mm, "end": v(69.53, 127.97) * mm});
            skLineSegment(sketch, "E381.left", {"start": v(66.19, 115.27) * mm, "end": v(66.19, 127.97) * mm});
            skLineSegment(sketch, "E381.right", {"start": v(78.89, 115.27) * mm, "end": v(78.89, 118.62) * mm});
            skLineSegment(sketch, "E382.0", {"start": v(70.95, 121.98) * mm, "end": v(70.95, 126.55) * mm});
            skLineSegment(sketch, "E382.1", {"start": v(72.38, 120.03) * mm, "end": v(77.47, 120.03) * mm});
            skArc(sketch, "E383.filletArc", {"start": v(70.95, 126.55) * mm, "mid": v(70.53, 127.56) * mm, "end": v(69.53, 127.97) * mm});
            skArc(sketch, "E384.filletArc", {"start": v(78.89, 118.62) * mm, "mid": v(78.47, 119.62) * mm, "end": v(77.47, 120.03) * mm});
            skArc(sketch, "E385", {"start": v(70.95, 121.98) * mm, "mid": v(71.35, 120.77) * mm, "end": v(72.38, 120.03) * mm});
            skLineSegment(sketch, "E386.bottom", {"start": v(84.62, 126.38) * mm, "end": v(71.92, 126.38) * mm});
            skLineSegment(sketch, "E386.top", {"start": v(84.62, 113.68) * mm, "end": v(81.27, 113.68) * mm});
            skLineSegment(sketch, "E386.left", {"start": v(84.62, 126.38) * mm, "end": v(84.62, 113.68) * mm});
            skLineSegment(sketch, "E386.right", {"start": v(71.92, 126.38) * mm, "end": v(71.92, 123.04) * mm});
            skLineSegment(sketch, "E387.0", {"start": v(79.85, 119.67) * mm, "end": v(79.85, 115.1) * mm});
            skLineSegment(sketch, "E387.1", {"start": v(78.42, 121.62) * mm, "end": v(73.33, 121.62) * mm});
            skArc(sketch, "E388.filletArc", {"start": v(79.85, 115.1) * mm, "mid": v(80.27, 114.1) * mm, "end": v(81.27, 113.68) * mm});
            skArc(sketch, "E389.filletArc", {"start": v(71.92, 123.04) * mm, "mid": v(72.33, 122.03) * mm, "end": v(73.33, 121.62) * mm});
            skArc(sketch, "E390", {"start": v(79.85, 119.67) * mm, "mid": v(79.46, 120.88) * mm, "end": v(78.42, 121.62) * mm});
            skLineSegment(sketch, "E391.bottom", {"start": v(66.54, 129) * mm, "end": v(79.24, 129) * mm});
            skLineSegment(sketch, "E391.top", {"start": v(66.54, 141.7) * mm, "end": v(69.88, 141.7) * mm});
            skLineSegment(sketch, "E391.left", {"start": v(66.54, 129) * mm, "end": v(66.54, 141.7) * mm});
            skLineSegment(sketch, "E391.right", {"start": v(79.24, 129) * mm, "end": v(79.24, 132.35) * mm});
            skLineSegment(sketch, "E392.0", {"start": v(71.3, 135.72) * mm, "end": v(71.3, 140.29) * mm});
            skLineSegment(sketch, "E392.1", {"start": v(72.73, 133.77) * mm, "end": v(77.82, 133.77) * mm});
            skArc(sketch, "E393.filletArc", {"start": v(71.3, 140.29) * mm, "mid": v(70.88, 141.3) * mm, "end": v(69.88, 141.7) * mm});
            skArc(sketch, "E394.filletArc", {"start": v(79.24, 132.35) * mm, "mid": v(78.82, 133.36) * mm, "end": v(77.82, 133.77) * mm});
            skArc(sketch, "E395", {"start": v(71.3, 135.72) * mm, "mid": v(71.7, 134.51) * mm, "end": v(72.73, 133.77) * mm});
            skLineSegment(sketch, "E396.bottom", {"start": v(84.97, 140.12) * mm, "end": v(72.27, 140.12) * mm});
            skLineSegment(sketch, "E396.top", {"start": v(84.97, 127.42) * mm, "end": v(81.62, 127.42) * mm});
            skLineSegment(sketch, "E396.left", {"start": v(84.97, 140.12) * mm, "end": v(84.97, 127.42) * mm});
            skLineSegment(sketch, "E396.right", {"start": v(72.27, 140.12) * mm, "end": v(72.27, 136.77) * mm});
            skLineSegment(sketch, "E397.0", {"start": v(80.2, 133.4) * mm, "end": v(80.2, 128.84) * mm});
            skLineSegment(sketch, "E397.1", {"start": v(78.77, 135.35) * mm, "end": v(73.69, 135.35) * mm});
            skArc(sketch, "E398.filletArc", {"start": v(80.2, 128.84) * mm, "mid": v(80.62, 127.83) * mm, "end": v(81.62, 127.42) * mm});
            skArc(sketch, "E399.filletArc", {"start": v(72.27, 136.77) * mm, "mid": v(72.68, 135.77) * mm, "end": v(73.69, 135.35) * mm});
            skArc(sketch, "E400", {"start": v(80.2, 133.4) * mm, "mid": v(79.8, 134.61) * mm, "end": v(78.77, 135.35) * mm});
            skLineSegment(sketch, "E401.bottom", {"start": v(87.6, 4.97) * mm, "end": v(100.3, 4.97) * mm});
            skLineSegment(sketch, "E401.top", {"start": v(87.6, 17.67) * mm, "end": v(90.93, 17.67) * mm});
            skLineSegment(sketch, "E401.left", {"start": v(87.6, 4.97) * mm, "end": v(87.6, 17.67) * mm});
            skLineSegment(sketch, "E401.right", {"start": v(100.3, 4.97) * mm, "end": v(100.3, 8.31) * mm});
            skLineSegment(sketch, "E402.0", {"start": v(92.35, 11.68) * mm, "end": v(92.35, 16.25) * mm});
            skLineSegment(sketch, "E402.1", {"start": v(93.79, 9.73) * mm, "end": v(98.87, 9.73) * mm});
            skArc(sketch, "E403.filletArc", {"start": v(92.35, 16.25) * mm, "mid": v(91.94, 17.25) * mm, "end": v(90.93, 17.67) * mm});
            skArc(sketch, "E404.filletArc", {"start": v(100.3, 8.31) * mm, "mid": v(99.88, 9.32) * mm, "end": v(98.87, 9.73) * mm});
            skArc(sketch, "E405", {"start": v(92.35, 11.68) * mm, "mid": v(92.75, 10.47) * mm, "end": v(93.79, 9.73) * mm});
            skLineSegment(sketch, "E406.bottom", {"start": v(106.02, 16.08) * mm, "end": v(93.32, 16.08) * mm});
            skLineSegment(sketch, "E406.top", {"start": v(106.02, 3.38) * mm, "end": v(102.68, 3.38) * mm});
            skLineSegment(sketch, "E406.left", {"start": v(106.02, 16.08) * mm, "end": v(106.02, 3.38) * mm});
            skLineSegment(sketch, "E406.right", {"start": v(93.32, 16.08) * mm, "end": v(93.32, 12.73) * mm});
            skLineSegment(sketch, "E407.0", {"start": v(101.26, 9.37) * mm, "end": v(101.26, 4.8) * mm});
            skLineSegment(sketch, "E407.1", {"start": v(99.82, 11.32) * mm, "end": v(94.74, 11.32) * mm});
            skArc(sketch, "E408.filletArc", {"start": v(101.26, 4.8) * mm, "mid": v(101.67, 3.8) * mm, "end": v(102.68, 3.38) * mm});
            skArc(sketch, "E409.filletArc", {"start": v(93.32, 12.73) * mm, "mid": v(93.73, 11.73) * mm, "end": v(94.74, 11.32) * mm});
            skArc(sketch, "E410", {"start": v(101.26, 9.37) * mm, "mid": v(100.86, 10.58) * mm, "end": v(99.82, 11.32) * mm});
            skLineSegment(sketch, "E411.bottom", {"start": v(87.61, 18.94) * mm, "end": v(100.31, 18.94) * mm});
            skLineSegment(sketch, "E411.top", {"start": v(87.61, 31.64) * mm, "end": v(90.96, 31.64) * mm});
            skLineSegment(sketch, "E411.left", {"start": v(87.61, 18.94) * mm, "end": v(87.61, 31.64) * mm});
            skLineSegment(sketch, "E411.right", {"start": v(100.31, 18.94) * mm, "end": v(100.31, 22.28) * mm});
            skLineSegment(sketch, "E412.0", {"start": v(92.37, 25.65) * mm, "end": v(92.37, 30.22) * mm});
            skLineSegment(sketch, "E412.1", {"start": v(93.8, 23.7) * mm, "end": v(98.9, 23.7) * mm});
            skArc(sketch, "E413.filletArc", {"start": v(92.37, 30.22) * mm, "mid": v(91.96, 31.22) * mm, "end": v(90.96, 31.64) * mm});
            skArc(sketch, "E414.filletArc", {"start": v(100.31, 22.28) * mm, "mid": v(99.9, 23.29) * mm, "end": v(98.9, 23.7) * mm});
            skArc(sketch, "E415", {"start": v(92.37, 25.65) * mm, "mid": v(92.77, 24.44) * mm, "end": v(93.8, 23.7) * mm});
            skLineSegment(sketch, "E416.bottom", {"start": v(106.04, 30.05) * mm, "end": v(93.34, 30.05) * mm});
            skLineSegment(sketch, "E416.top", {"start": v(106.04, 17.35) * mm, "end": v(102.7, 17.35) * mm});
            skLineSegment(sketch, "E416.left", {"start": v(106.04, 30.05) * mm, "end": v(106.04, 17.35) * mm});
            skLineSegment(sketch, "E416.right", {"start": v(93.34, 30.05) * mm, "end": v(93.34, 26.7) * mm});
            skLineSegment(sketch, "E417.0", {"start": v(101.28, 23.34) * mm, "end": v(101.28, 18.77) * mm});
            skLineSegment(sketch, "E417.1", {"start": v(99.84, 25.29) * mm, "end": v(94.76, 25.29) * mm});
            skArc(sketch, "E418.filletArc", {"start": v(101.28, 18.77) * mm, "mid": v(101.7, 17.76) * mm, "end": v(102.7, 17.35) * mm});
            skArc(sketch, "E419.filletArc", {"start": v(93.34, 26.7) * mm, "mid": v(93.76, 25.7) * mm, "end": v(94.76, 25.29) * mm});
            skArc(sketch, "E420", {"start": v(101.28, 23.34) * mm, "mid": v(100.88, 24.55) * mm, "end": v(99.84, 25.29) * mm});
            skLineSegment(sketch, "E421.bottom", {"start": v(87.56, 32.87) * mm, "end": v(100.26, 32.87) * mm});
            skLineSegment(sketch, "E421.top", {"start": v(87.56, 45.57) * mm, "end": v(90.9, 45.57) * mm});
            skLineSegment(sketch, "E421.left", {"start": v(87.56, 32.87) * mm, "end": v(87.56, 45.57) * mm});
            skLineSegment(sketch, "E421.right", {"start": v(100.26, 32.87) * mm, "end": v(100.26, 36.21) * mm});
            skLineSegment(sketch, "E422.0", {"start": v(92.32, 39.58) * mm, "end": v(92.32, 44.15) * mm});
            skLineSegment(sketch, "E422.1", {"start": v(93.76, 37.63) * mm, "end": v(98.84, 37.63) * mm});
            skArc(sketch, "E423.filletArc", {"start": v(92.32, 44.15) * mm, "mid": v(91.9, 45.15) * mm, "end": v(90.9, 45.57) * mm});
            skArc(sketch, "E424.filletArc", {"start": v(100.26, 36.21) * mm, "mid": v(99.85, 37.22) * mm, "end": v(98.84, 37.63) * mm});
            skArc(sketch, "E425", {"start": v(92.32, 39.58) * mm, "mid": v(92.72, 38.37) * mm, "end": v(93.76, 37.63) * mm});
            skLineSegment(sketch, "E426.bottom", {"start": v(105.99, 43.98) * mm, "end": v(93.29, 43.98) * mm});
            skLineSegment(sketch, "E426.top", {"start": v(105.99, 31.28) * mm, "end": v(102.65, 31.28) * mm});
            skLineSegment(sketch, "E426.left", {"start": v(105.99, 43.98) * mm, "end": v(105.99, 31.28) * mm});
            skLineSegment(sketch, "E426.right", {"start": v(93.29, 43.98) * mm, "end": v(93.29, 40.63) * mm});
            skLineSegment(sketch, "E427.0", {"start": v(101.23, 37.27) * mm, "end": v(101.23, 32.7) * mm});
            skLineSegment(sketch, "E427.1", {"start": v(99.8, 39.21) * mm, "end": v(94.7, 39.21) * mm});
            skArc(sketch, "E428.filletArc", {"start": v(101.23, 32.7) * mm, "mid": v(101.64, 31.7) * mm, "end": v(102.65, 31.28) * mm});
            skArc(sketch, "E429.filletArc", {"start": v(93.29, 40.63) * mm, "mid": v(93.7, 39.63) * mm, "end": v(94.7, 39.21) * mm});
            skArc(sketch, "E430", {"start": v(101.23, 37.27) * mm, "mid": v(100.83, 38.48) * mm, "end": v(99.8, 39.21) * mm});
            skLineSegment(sketch, "E431.bottom", {"start": v(87.56, 47.1) * mm, "end": v(100.26, 47.1) * mm});
            skLineSegment(sketch, "E431.top", {"start": v(87.56, 59.8) * mm, "end": v(90.9, 59.8) * mm});
            skLineSegment(sketch, "E431.left", {"start": v(87.56, 47.1) * mm, "end": v(87.56, 59.8) * mm});
            skLineSegment(sketch, "E431.right", {"start": v(100.26, 47.1) * mm, "end": v(100.26, 50.44) * mm});
            skLineSegment(sketch, "E432.0", {"start": v(92.32, 53.8) * mm, "end": v(92.32, 58.37) * mm});
            skLineSegment(sketch, "E432.1", {"start": v(93.76, 51.86) * mm, "end": v(98.84, 51.86) * mm});
            skArc(sketch, "E433.filletArc", {"start": v(92.32, 58.37) * mm, "mid": v(91.9, 59.38) * mm, "end": v(90.9, 59.8) * mm});
            skArc(sketch, "E434.filletArc", {"start": v(100.26, 50.44) * mm, "mid": v(99.85, 51.44) * mm, "end": v(98.84, 51.86) * mm});
            skArc(sketch, "E435", {"start": v(92.32, 53.8) * mm, "mid": v(92.72, 52.6) * mm, "end": v(93.76, 51.86) * mm});
            skLineSegment(sketch, "E436.bottom", {"start": v(105.99, 58.2) * mm, "end": v(93.29, 58.2) * mm});
            skLineSegment(sketch, "E436.top", {"start": v(105.99, 45.5) * mm, "end": v(102.65, 45.5) * mm});
            skLineSegment(sketch, "E436.left", {"start": v(105.99, 58.2) * mm, "end": v(105.99, 45.5) * mm});
            skLineSegment(sketch, "E436.right", {"start": v(93.29, 58.2) * mm, "end": v(93.29, 54.86) * mm});
            skLineSegment(sketch, "E437.0", {"start": v(101.23, 51.5) * mm, "end": v(101.23, 46.92) * mm});
            skLineSegment(sketch, "E437.1", {"start": v(99.8, 53.44) * mm, "end": v(94.7, 53.44) * mm});
            skArc(sketch, "E438.filletArc", {"start": v(101.23, 46.92) * mm, "mid": v(101.64, 45.92) * mm, "end": v(102.65, 45.5) * mm});
            skArc(sketch, "E439.filletArc", {"start": v(93.29, 54.86) * mm, "mid": v(93.7, 53.85) * mm, "end": v(94.7, 53.44) * mm});
            skArc(sketch, "E440", {"start": v(101.23, 51.5) * mm, "mid": v(100.83, 52.7) * mm, "end": v(99.8, 53.44) * mm});
            skLineSegment(sketch, "E441.bottom", {"start": v(87.3, 60.86) * mm, "end": v(100, 60.86) * mm});
            skLineSegment(sketch, "E441.top", {"start": v(87.3, 73.56) * mm, "end": v(90.65, 73.56) * mm});
            skLineSegment(sketch, "E441.left", {"start": v(87.3, 60.86) * mm, "end": v(87.3, 73.56) * mm});
            skLineSegment(sketch, "E441.right", {"start": v(100, 60.86) * mm, "end": v(100, 64.2) * mm});
            skLineSegment(sketch, "E442.0", {"start": v(92.07, 67.57) * mm, "end": v(92.07, 72.14) * mm});
            skLineSegment(sketch, "E442.1", {"start": v(93.5, 65.62) * mm, "end": v(98.6, 65.62) * mm});
            skArc(sketch, "E443.filletArc", {"start": v(92.07, 72.14) * mm, "mid": v(91.66, 73.15) * mm, "end": v(90.65, 73.56) * mm});
            skArc(sketch, "E444.filletArc", {"start": v(100, 64.2) * mm, "mid": v(99.6, 65.2) * mm, "end": v(98.6, 65.62) * mm});
            skArc(sketch, "E445", {"start": v(92.07, 67.57) * mm, "mid": v(92.47, 66.36) * mm, "end": v(93.5, 65.62) * mm});
            skLineSegment(sketch, "E446.bottom", {"start": v(105.74, 71.97) * mm, "end": v(93.04, 71.97) * mm});
            skLineSegment(sketch, "E446.top", {"start": v(105.74, 59.27) * mm, "end": v(102.4, 59.27) * mm});
            skLineSegment(sketch, "E446.left", {"start": v(105.74, 71.97) * mm, "end": v(105.74, 59.27) * mm});
            skLineSegment(sketch, "E446.right", {"start": v(93.04, 71.97) * mm, "end": v(93.04, 68.63) * mm});
            skLineSegment(sketch, "E447.0", {"start": v(100.98, 65.26) * mm, "end": v(100.98, 60.69) * mm});
            skLineSegment(sketch, "E447.1", {"start": v(99.54, 67.2) * mm, "end": v(94.46, 67.2) * mm});
            skArc(sketch, "E448.filletArc", {"start": v(100.98, 60.69) * mm, "mid": v(101.4, 59.68) * mm, "end": v(102.4, 59.27) * mm});
            skArc(sketch, "E449.filletArc", {"start": v(93.04, 68.63) * mm, "mid": v(93.45, 67.62) * mm, "end": v(94.46, 67.2) * mm});
            skArc(sketch, "E450", {"start": v(100.98, 65.26) * mm, "mid": v(100.58, 66.47) * mm, "end": v(99.54, 67.2) * mm});
            skLineSegment(sketch, "E451.bottom", {"start": v(86.97, 74.95) * mm, "end": v(99.67, 74.95) * mm});
            skLineSegment(sketch, "E451.top", {"start": v(86.97, 87.65) * mm, "end": v(90.31, 87.65) * mm});
            skLineSegment(sketch, "E451.left", {"start": v(86.97, 74.95) * mm, "end": v(86.97, 87.65) * mm});
            skLineSegment(sketch, "E451.right", {"start": v(99.67, 74.95) * mm, "end": v(99.67, 78.29) * mm});
            skLineSegment(sketch, "E452.0", {"start": v(91.73, 81.66) * mm, "end": v(91.73, 86.23) * mm});
            skLineSegment(sketch, "E452.1", {"start": v(93.17, 79.7) * mm, "end": v(98.25, 79.7) * mm});
            skArc(sketch, "E453.filletArc", {"start": v(91.73, 86.23) * mm, "mid": v(91.32, 87.23) * mm, "end": v(90.31, 87.65) * mm});
            skArc(sketch, "E454.filletArc", {"start": v(99.67, 78.29) * mm, "mid": v(99.25, 79.3) * mm, "end": v(98.25, 79.7) * mm});
            skArc(sketch, "E455", {"start": v(91.73, 81.66) * mm, "mid": v(92.13, 80.45) * mm, "end": v(93.17, 79.7) * mm});
            skLineSegment(sketch, "E456.bottom", {"start": v(105.4, 86.05) * mm, "end": v(92.7, 86.05) * mm});
            skLineSegment(sketch, "E456.top", {"start": v(105.4, 73.35) * mm, "end": v(102.05, 73.35) * mm});
            skLineSegment(sketch, "E456.left", {"start": v(105.4, 86.05) * mm, "end": v(105.4, 73.35) * mm});
            skLineSegment(sketch, "E456.right", {"start": v(92.7, 86.05) * mm, "end": v(92.7, 82.71) * mm});
            skLineSegment(sketch, "E457.0", {"start": v(100.64, 79.34) * mm, "end": v(100.64, 74.77) * mm});
            skLineSegment(sketch, "E457.1", {"start": v(99.2, 81.3) * mm, "end": v(94.12, 81.3) * mm});
            skArc(sketch, "E458.filletArc", {"start": v(100.64, 74.77) * mm, "mid": v(101.05, 73.77) * mm, "end": v(102.05, 73.35) * mm});
            skArc(sketch, "E459.filletArc", {"start": v(92.7, 82.71) * mm, "mid": v(93.11, 81.7) * mm, "end": v(94.12, 81.3) * mm});
            skArc(sketch, "E460", {"start": v(100.64, 79.34) * mm, "mid": v(100.24, 80.55) * mm, "end": v(99.2, 81.3) * mm});
            skLineSegment(sketch, "E461.bottom", {"start": v(86.78, 88.84) * mm, "end": v(99.48, 88.84) * mm});
            skLineSegment(sketch, "E461.top", {"start": v(86.78, 101.54) * mm, "end": v(90.12, 101.54) * mm});
            skLineSegment(sketch, "E461.left", {"start": v(86.78, 88.84) * mm, "end": v(86.78, 101.54) * mm});
            skLineSegment(sketch, "E461.right", {"start": v(99.48, 88.84) * mm, "end": v(99.48, 92.18) * mm});
            skLineSegment(sketch, "E462.0", {"start": v(91.54, 95.55) * mm, "end": v(91.54, 100.12) * mm});
            skLineSegment(sketch, "E462.1", {"start": v(92.98, 93.6) * mm, "end": v(98.06, 93.6) * mm});
            skArc(sketch, "E463.filletArc", {"start": v(91.54, 100.12) * mm, "mid": v(91.13, 101.12) * mm, "end": v(90.12, 101.54) * mm});
            skArc(sketch, "E464.filletArc", {"start": v(99.48, 92.18) * mm, "mid": v(99.06, 93.18) * mm, "end": v(98.06, 93.6) * mm});
            skArc(sketch, "E465", {"start": v(91.54, 95.55) * mm, "mid": v(91.94, 94.34) * mm, "end": v(92.98, 93.6) * mm});
            skLineSegment(sketch, "E466.bottom", {"start": v(105.2, 99.94) * mm, "end": v(92.5, 99.94) * mm});
            skLineSegment(sketch, "E466.top", {"start": v(105.2, 87.24) * mm, "end": v(101.86, 87.24) * mm});
            skLineSegment(sketch, "E466.left", {"start": v(105.2, 99.94) * mm, "end": v(105.2, 87.24) * mm});
            skLineSegment(sketch, "E466.right", {"start": v(92.5, 99.94) * mm, "end": v(92.5, 96.6) * mm});
            skLineSegment(sketch, "E467.0", {"start": v(100.45, 93.23) * mm, "end": v(100.45, 88.66) * mm});
            skLineSegment(sketch, "E467.1", {"start": v(99.01, 95.18) * mm, "end": v(93.93, 95.18) * mm});
            skArc(sketch, "E468.filletArc", {"start": v(100.45, 88.66) * mm, "mid": v(100.86, 87.66) * mm, "end": v(101.86, 87.24) * mm});
            skArc(sketch, "E469.filletArc", {"start": v(92.5, 96.6) * mm, "mid": v(92.92, 95.6) * mm, "end": v(93.93, 95.18) * mm});
            skArc(sketch, "E470", {"start": v(100.45, 93.23) * mm, "mid": v(100.05, 94.44) * mm, "end": v(99.01, 95.18) * mm});
            skLineSegment(sketch, "E471.bottom", {"start": v(86.72, 102.73) * mm, "end": v(99.42, 102.73) * mm});
            skLineSegment(sketch, "E471.top", {"start": v(86.72, 115.43) * mm, "end": v(90.06, 115.43) * mm});
            skLineSegment(sketch, "E471.left", {"start": v(86.72, 102.73) * mm, "end": v(86.72, 115.43) * mm});
            skLineSegment(sketch, "E471.right", {"start": v(99.42, 102.73) * mm, "end": v(99.42, 106.08) * mm});
            skLineSegment(sketch, "E472.0", {"start": v(91.48, 109.45) * mm, "end": v(91.48, 114.02) * mm});
            skLineSegment(sketch, "E472.1", {"start": v(92.91, 107.5) * mm, "end": v(98, 107.5) * mm});
            skArc(sketch, "E473.filletArc", {"start": v(91.48, 114.02) * mm, "mid": v(91.06, 115.02) * mm, "end": v(90.06, 115.43) * mm});
            skArc(sketch, "E474.filletArc", {"start": v(99.42, 106.08) * mm, "mid": v(99, 107.08) * mm, "end": v(98, 107.5) * mm});
            skArc(sketch, "E475", {"start": v(91.48, 109.45) * mm, "mid": v(91.88, 108.24) * mm, "end": v(92.91, 107.5) * mm});
            skLineSegment(sketch, "E476.bottom", {"start": v(105.14, 113.84) * mm, "end": v(92.44, 113.84) * mm});
            skLineSegment(sketch, "E476.top", {"start": v(105.14, 101.14) * mm, "end": v(101.8, 101.14) * mm});
            skLineSegment(sketch, "E476.left", {"start": v(105.14, 113.84) * mm, "end": v(105.14, 101.14) * mm});
            skLineSegment(sketch, "E476.right", {"start": v(92.44, 113.84) * mm, "end": v(92.44, 110.5) * mm});
            skLineSegment(sketch, "E477.0", {"start": v(100.38, 107.13) * mm, "end": v(100.38, 102.56) * mm});
            skLineSegment(sketch, "E477.1", {"start": v(98.95, 109.08) * mm, "end": v(93.86, 109.08) * mm});
            skArc(sketch, "E478.filletArc", {"start": v(100.38, 102.56) * mm, "mid": v(100.8, 101.56) * mm, "end": v(101.8, 101.14) * mm});
            skArc(sketch, "E479.filletArc", {"start": v(92.44, 110.5) * mm, "mid": v(92.86, 109.5) * mm, "end": v(93.86, 109.08) * mm});
            skArc(sketch, "E480", {"start": v(100.38, 107.13) * mm, "mid": v(99.99, 108.34) * mm, "end": v(98.95, 109.08) * mm});
            skLineSegment(sketch, "E481.bottom", {"start": v(86.85, 116.69) * mm, "end": v(99.55, 116.69) * mm});
            skLineSegment(sketch, "E481.top", {"start": v(86.85, 129.39) * mm, "end": v(90.2, 129.39) * mm});
            skLineSegment(sketch, "E481.left", {"start": v(86.85, 116.69) * mm, "end": v(86.85, 129.39) * mm});
            skLineSegment(sketch, "E481.right", {"start": v(99.55, 116.69) * mm, "end": v(99.55, 120.03) * mm});
            skLineSegment(sketch, "E482.0", {"start": v(91.61, 123.4) * mm, "end": v(91.61, 127.97) * mm});
            skLineSegment(sketch, "E482.1", {"start": v(93.05, 121.45) * mm, "end": v(98.13, 121.45) * mm});
            skArc(sketch, "E483.filletArc", {"start": v(91.61, 127.97) * mm, "mid": v(91.2, 128.97) * mm, "end": v(90.2, 129.39) * mm});
            skArc(sketch, "E484.filletArc", {"start": v(99.55, 120.03) * mm, "mid": v(99.14, 121.03) * mm, "end": v(98.13, 121.45) * mm});
            skArc(sketch, "E485", {"start": v(91.61, 123.4) * mm, "mid": v(92.01, 122.19) * mm, "end": v(93.05, 121.45) * mm});
            skLineSegment(sketch, "E486.bottom", {"start": v(105.28, 127.8) * mm, "end": v(92.58, 127.8) * mm});
            skLineSegment(sketch, "E486.top", {"start": v(105.28, 115.1) * mm, "end": v(101.94, 115.1) * mm});
            skLineSegment(sketch, "E486.left", {"start": v(105.28, 127.8) * mm, "end": v(105.28, 115.1) * mm});
            skLineSegment(sketch, "E486.right", {"start": v(92.58, 127.8) * mm, "end": v(92.58, 124.45) * mm});
            skLineSegment(sketch, "E487.0", {"start": v(100.52, 121.08) * mm, "end": v(100.52, 116.51) * mm});
            skLineSegment(sketch, "E487.1", {"start": v(99.08, 123.03) * mm, "end": v(94, 123.03) * mm});
            skArc(sketch, "E488.filletArc", {"start": v(100.52, 116.51) * mm, "mid": v(100.93, 115.5) * mm, "end": v(101.94, 115.1) * mm});
            skArc(sketch, "E489.filletArc", {"start": v(92.58, 124.45) * mm, "mid": v(93, 123.45) * mm, "end": v(94, 123.03) * mm});
            skArc(sketch, "E490", {"start": v(100.52, 121.08) * mm, "mid": v(100.12, 122.3) * mm, "end": v(99.08, 123.03) * mm});
            skLineSegment(sketch, "E491.bottom", {"start": v(87.2, 130.42) * mm, "end": v(99.9, 130.42) * mm});
            skLineSegment(sketch, "E491.top", {"start": v(87.2, 143.12) * mm, "end": v(90.54, 143.12) * mm});
            skLineSegment(sketch, "E491.left", {"start": v(87.2, 130.42) * mm, "end": v(87.2, 143.12) * mm});
            skLineSegment(sketch, "E491.right", {"start": v(99.9, 130.42) * mm, "end": v(99.9, 133.77) * mm});
            skLineSegment(sketch, "E492.0", {"start": v(91.96, 137.13) * mm, "end": v(91.96, 141.7) * mm});
            skLineSegment(sketch, "E492.1", {"start": v(93.4, 135.19) * mm, "end": v(98.48, 135.19) * mm});
            skArc(sketch, "E493.filletArc", {"start": v(91.96, 141.7) * mm, "mid": v(91.55, 142.7) * mm, "end": v(90.54, 143.12) * mm});
            skArc(sketch, "E494.filletArc", {"start": v(99.9, 133.77) * mm, "mid": v(99.49, 134.77) * mm, "end": v(98.48, 135.19) * mm});
            skArc(sketch, "E495", {"start": v(91.96, 137.13) * mm, "mid": v(92.36, 135.92) * mm, "end": v(93.4, 135.19) * mm});
            skLineSegment(sketch, "E496.bottom", {"start": v(105.63, 141.53) * mm, "end": v(92.93, 141.53) * mm});
            skLineSegment(sketch, "E496.top", {"start": v(105.63, 128.83) * mm, "end": v(102.29, 128.83) * mm});
            skLineSegment(sketch, "E496.left", {"start": v(105.63, 141.53) * mm, "end": v(105.63, 128.83) * mm});
            skLineSegment(sketch, "E496.right", {"start": v(92.93, 141.53) * mm, "end": v(92.93, 138.19) * mm});
            skLineSegment(sketch, "E497.0", {"start": v(100.87, 134.82) * mm, "end": v(100.87, 130.25) * mm});
            skLineSegment(sketch, "E497.1", {"start": v(99.43, 136.77) * mm, "end": v(94.35, 136.77) * mm});
            skArc(sketch, "E498.filletArc", {"start": v(100.87, 130.25) * mm, "mid": v(101.28, 129.25) * mm, "end": v(102.29, 128.83) * mm});
            skArc(sketch, "E499.filletArc", {"start": v(92.93, 138.19) * mm, "mid": v(93.34, 137.18) * mm, "end": v(94.35, 136.77) * mm});
            skArc(sketch, "E500", {"start": v(100.87, 134.82) * mm, "mid": v(100.47, 136.03) * mm, "end": v(99.43, 136.77) * mm});
            skSolve(sketch);
        }
        {
            var Q0;
            Q0=makeQuery(id+"F0.imprint","IMPRINT",FACE,{"disambiguationData":[TD([[makeQuery(id+"F0.imprint","IMPRINT",EDGE,{"derivedFrom":sQuery(id+"F0.wireOp",EDGE,"E1.bottom")}),1.0]])]});
            var Q1;
            Q1=makeQuery(id+"F0.imprint","IMPRINT",FACE,{"disambiguationData":[TD([[makeQuery(id+"F0.imprint","IMPRINT",EDGE,{"derivedFrom":sQuery(id+"F0.wireOp",EDGE,"E6.bottom")}),1.0]])]});
            var Q2;
            Q2=makeQuery(id+"F0.imprint","IMPRINT",FACE,{"disambiguationData":[TD([[makeQuery(id+"F0.imprint","IMPRINT",EDGE,{"derivedFrom":sQuery(id+"F0.wireOp",EDGE,"E11.bottom")}),1.0]])]});
            var Q3;
            Q3=makeQuery(id+"F0.imprint","IMPRINT",FACE,{"disambiguationData":[TD([[makeQuery(id+"F0.imprint","IMPRINT",EDGE,{"derivedFrom":sQuery(id+"F0.wireOp",EDGE,"E16.bottom")}),1.0]])]});
            var Q4;
            Q4=makeQuery(id+"F0.imprint","IMPRINT",FACE,{"disambiguationData":[TD([[makeQuery(id+"F0.imprint","IMPRINT",EDGE,{"derivedFrom":sQuery(id+"F0.wireOp",EDGE,"E21.bottom")}),1.0]])]});
            var Q5;
            Q5=makeQuery(id+"F0.imprint","IMPRINT",FACE,{"disambiguationData":[TD([[makeQuery(id+"F0.imprint","IMPRINT",EDGE,{"derivedFrom":sQuery(id+"F0.wireOp",EDGE,"E26.bottom")}),1.0]])]});
            var Q6;
            Q6=makeQuery(id+"F0.imprint","IMPRINT",FACE,{"disambiguationData":[TD([[makeQuery(id+"F0.imprint","IMPRINT",EDGE,{"derivedFrom":sQuery(id+"F0.wireOp",EDGE,"E31.bottom")}),1.0]])]});
            var Q7;
            Q7=makeQuery(id+"F0.imprint","IMPRINT",FACE,{"disambiguationData":[TD([[makeQuery(id+"F0.imprint","IMPRINT",EDGE,{"derivedFrom":sQuery(id+"F0.wireOp",EDGE,"E36.bottom")}),1.0]])]});
            var Q8;
            Q8=makeQuery(id+"F0.imprint","IMPRINT",FACE,{"disambiguationData":[TD([[makeQuery(id+"F0.imprint","IMPRINT",EDGE,{"derivedFrom":sQuery(id+"F0.wireOp",EDGE,"E41.bottom")}),1.0]])]});
            var Q9;
            Q9=makeQuery(id+"F0.imprint","IMPRINT",FACE,{"disambiguationData":[TD([[makeQuery(id+"F0.imprint","IMPRINT",EDGE,{"derivedFrom":sQuery(id+"F0.wireOp",EDGE,"E46.bottom")}),1.0]])]});
            var Q10;
            Q10=makeQuery(id+"F0.imprint","IMPRINT",FACE,{"disambiguationData":[TD([[makeQuery(id+"F0.imprint","IMPRINT",EDGE,{"derivedFrom":sQuery(id+"F0.wireOp",EDGE,"E51.bottom")}),1.0]])]});
            var Q11;
            Q11=makeQuery(id+"F0.imprint","IMPRINT",FACE,{"disambiguationData":[TD([[makeQuery(id+"F0.imprint","IMPRINT",EDGE,{"derivedFrom":sQuery(id+"F0.wireOp",EDGE,"E56.bottom")}),1.0]])]});
            var Q12;
            Q12=makeQuery(id+"F0.imprint","IMPRINT",FACE,{"disambiguationData":[TD([[makeQuery(id+"F0.imprint","IMPRINT",EDGE,{"derivedFrom":sQuery(id+"F0.wireOp",EDGE,"E61.bottom")}),1.0]])]});
            var Q13;
            Q13=makeQuery(id+"F0.imprint","IMPRINT",FACE,{"disambiguationData":[TD([[makeQuery(id+"F0.imprint","IMPRINT",EDGE,{"derivedFrom":sQuery(id+"F0.wireOp",EDGE,"E66.bottom")}),1.0]])]});
            var Q14;
            Q14=makeQuery(id+"F0.imprint","IMPRINT",FACE,{"disambiguationData":[TD([[makeQuery(id+"F0.imprint","IMPRINT",EDGE,{"derivedFrom":sQuery(id+"F0.wireOp",EDGE,"E71.bottom")}),1.0]])]});
            var Q15;
            Q15=makeQuery(id+"F0.imprint","IMPRINT",FACE,{"disambiguationData":[TD([[makeQuery(id+"F0.imprint","IMPRINT",EDGE,{"derivedFrom":sQuery(id+"F0.wireOp",EDGE,"E76.bottom")}),1.0]])]});
            var Q16;
            Q16=makeQuery(id+"F0.imprint","IMPRINT",FACE,{"disambiguationData":[TD([[makeQuery(id+"F0.imprint","IMPRINT",EDGE,{"derivedFrom":sQuery(id+"F0.wireOp",EDGE,"E81.bottom")}),1.0]])]});
            var Q17;
            Q17=makeQuery(id+"F0.imprint","IMPRINT",FACE,{"disambiguationData":[TD([[makeQuery(id+"F0.imprint","IMPRINT",EDGE,{"derivedFrom":sQuery(id+"F0.wireOp",EDGE,"E86.bottom")}),1.0]])]});
            var Q18;
            Q18=makeQuery(id+"F0.imprint","IMPRINT",FACE,{"disambiguationData":[TD([[makeQuery(id+"F0.imprint","IMPRINT",EDGE,{"derivedFrom":sQuery(id+"F0.wireOp",EDGE,"E91.bottom")}),1.0]])]});
            var Q19;
            Q19=makeQuery(id+"F0.imprint","IMPRINT",FACE,{"disambiguationData":[TD([[makeQuery(id+"F0.imprint","IMPRINT",EDGE,{"derivedFrom":sQuery(id+"F0.wireOp",EDGE,"E96.bottom")}),1.0]])]});
            var Q20;
            Q20=makeQuery(id+"F0.imprint","IMPRINT",FACE,{"disambiguationData":[TD([[makeQuery(id+"F0.imprint","IMPRINT",EDGE,{"derivedFrom":sQuery(id+"F0.wireOp",EDGE,"E191.bottom")}),1.0]])]});
            var Q21;
            Q21=makeQuery(id+"F0.imprint","IMPRINT",FACE,{"disambiguationData":[TD([[makeQuery(id+"F0.imprint","IMPRINT",EDGE,{"derivedFrom":sQuery(id+"F0.wireOp",EDGE,"E196.bottom")}),1.0]])]});
            var Q22;
            Q22=makeQuery(id+"F0.imprint","IMPRINT",FACE,{"disambiguationData":[TD([[makeQuery(id+"F0.imprint","IMPRINT",EDGE,{"derivedFrom":sQuery(id+"F0.wireOp",EDGE,"E181.bottom")}),1.0]])]});
            var Q23;
            Q23=makeQuery(id+"F0.imprint","IMPRINT",FACE,{"disambiguationData":[TD([[makeQuery(id+"F0.imprint","IMPRINT",EDGE,{"derivedFrom":sQuery(id+"F0.wireOp",EDGE,"E186.bottom")}),1.0]])]});
            var Q24;
            Q24=makeQuery(id+"F0.imprint","IMPRINT",FACE,{"disambiguationData":[TD([[makeQuery(id+"F0.imprint","IMPRINT",EDGE,{"derivedFrom":sQuery(id+"F0.wireOp",EDGE,"E171.bottom")}),1.0]])]});
            var Q25;
            Q25=makeQuery(id+"F0.imprint","IMPRINT",FACE,{"disambiguationData":[TD([[makeQuery(id+"F0.imprint","IMPRINT",EDGE,{"derivedFrom":sQuery(id+"F0.wireOp",EDGE,"E176.bottom")}),1.0]])]});
            var Q26;
            Q26=makeQuery(id+"F0.imprint","IMPRINT",FACE,{"disambiguationData":[TD([[makeQuery(id+"F0.imprint","IMPRINT",EDGE,{"derivedFrom":sQuery(id+"F0.wireOp",EDGE,"E161.bottom")}),1.0]])]});
            var Q27;
            Q27=makeQuery(id+"F0.imprint","IMPRINT",FACE,{"disambiguationData":[TD([[makeQuery(id+"F0.imprint","IMPRINT",EDGE,{"derivedFrom":sQuery(id+"F0.wireOp",EDGE,"E166.bottom")}),1.0]])]});
            var Q28;
            Q28=makeQuery(id+"F0.imprint","IMPRINT",FACE,{"disambiguationData":[TD([[makeQuery(id+"F0.imprint","IMPRINT",EDGE,{"derivedFrom":sQuery(id+"F0.wireOp",EDGE,"E151.bottom")}),1.0]])]});
            var Q29;
            Q29=makeQuery(id+"F0.imprint","IMPRINT",FACE,{"disambiguationData":[TD([[makeQuery(id+"F0.imprint","IMPRINT",EDGE,{"derivedFrom":sQuery(id+"F0.wireOp",EDGE,"E156.bottom")}),1.0]])]});
            var Q30;
            Q30=makeQuery(id+"F0.imprint","IMPRINT",FACE,{"disambiguationData":[TD([[makeQuery(id+"F0.imprint","IMPRINT",EDGE,{"derivedFrom":sQuery(id+"F0.wireOp",EDGE,"E141.bottom")}),1.0]])]});
            var Q31;
            Q31=makeQuery(id+"F0.imprint","IMPRINT",FACE,{"disambiguationData":[TD([[makeQuery(id+"F0.imprint","IMPRINT",EDGE,{"derivedFrom":sQuery(id+"F0.wireOp",EDGE,"E146.bottom")}),1.0]])]});
            var Q32;
            Q32=makeQuery(id+"F0.imprint","IMPRINT",FACE,{"disambiguationData":[TD([[makeQuery(id+"F0.imprint","IMPRINT",EDGE,{"derivedFrom":sQuery(id+"F0.wireOp",EDGE,"E131.bottom")}),1.0]])]});
            var Q33;
            Q33=makeQuery(id+"F0.imprint","IMPRINT",FACE,{"disambiguationData":[TD([[makeQuery(id+"F0.imprint","IMPRINT",EDGE,{"derivedFrom":sQuery(id+"F0.wireOp",EDGE,"E136.bottom")}),1.0]])]});
            var Q34;
            Q34=makeQuery(id+"F0.imprint","IMPRINT",FACE,{"disambiguationData":[TD([[makeQuery(id+"F0.imprint","IMPRINT",EDGE,{"derivedFrom":sQuery(id+"F0.wireOp",EDGE,"E121.bottom")}),1.0]])]});
            var Q35;
            Q35=makeQuery(id+"F0.imprint","IMPRINT",FACE,{"disambiguationData":[TD([[makeQuery(id+"F0.imprint","IMPRINT",EDGE,{"derivedFrom":sQuery(id+"F0.wireOp",EDGE,"E126.bottom")}),1.0]])]});
            var Q36;
            Q36=makeQuery(id+"F0.imprint","IMPRINT",FACE,{"disambiguationData":[TD([[makeQuery(id+"F0.imprint","IMPRINT",EDGE,{"derivedFrom":sQuery(id+"F0.wireOp",EDGE,"E111.bottom")}),1.0]])]});
            var Q37;
            Q37=makeQuery(id+"F0.imprint","IMPRINT",FACE,{"disambiguationData":[TD([[makeQuery(id+"F0.imprint","IMPRINT",EDGE,{"derivedFrom":sQuery(id+"F0.wireOp",EDGE,"E116.bottom")}),1.0]])]});
            var Q38;
            Q38=makeQuery(id+"F0.imprint","IMPRINT",FACE,{"disambiguationData":[TD([[makeQuery(id+"F0.imprint","IMPRINT",EDGE,{"derivedFrom":sQuery(id+"F0.wireOp",EDGE,"E101.bottom")}),1.0]])]});
            var Q39;
            Q39=makeQuery(id+"F0.imprint","IMPRINT",FACE,{"disambiguationData":[TD([[makeQuery(id+"F0.imprint","IMPRINT",EDGE,{"derivedFrom":sQuery(id+"F0.wireOp",EDGE,"E106.bottom")}),1.0]])]});
            var Q40;
            Q40=makeQuery(id+"F0.imprint","IMPRINT",FACE,{"disambiguationData":[TD([[makeQuery(id+"F0.imprint","IMPRINT",EDGE,{"derivedFrom":sQuery(id+"F0.wireOp",EDGE,"E291.bottom")}),1.0]])]});
            var Q41;
            Q41=makeQuery(id+"F0.imprint","IMPRINT",FACE,{"disambiguationData":[TD([[makeQuery(id+"F0.imprint","IMPRINT",EDGE,{"derivedFrom":sQuery(id+"F0.wireOp",EDGE,"E296.bottom")}),1.0]])]});
            var Q42;
            Q42=makeQuery(id+"F0.imprint","IMPRINT",FACE,{"disambiguationData":[TD([[makeQuery(id+"F0.imprint","IMPRINT",EDGE,{"derivedFrom":sQuery(id+"F0.wireOp",EDGE,"E281.bottom")}),1.0]])]});
            var Q43;
            Q43=makeQuery(id+"F0.imprint","IMPRINT",FACE,{"disambiguationData":[TD([[makeQuery(id+"F0.imprint","IMPRINT",EDGE,{"derivedFrom":sQuery(id+"F0.wireOp",EDGE,"E286.bottom")}),1.0]])]});
            var Q44;
            Q44=makeQuery(id+"F0.imprint","IMPRINT",FACE,{"disambiguationData":[TD([[makeQuery(id+"F0.imprint","IMPRINT",EDGE,{"derivedFrom":sQuery(id+"F0.wireOp",EDGE,"E271.bottom")}),1.0]])]});
            var Q45;
            Q45=makeQuery(id+"F0.imprint","IMPRINT",FACE,{"disambiguationData":[TD([[makeQuery(id+"F0.imprint","IMPRINT",EDGE,{"derivedFrom":sQuery(id+"F0.wireOp",EDGE,"E276.bottom")}),1.0]])]});
            var Q46;
            Q46=makeQuery(id+"F0.imprint","IMPRINT",FACE,{"disambiguationData":[TD([[makeQuery(id+"F0.imprint","IMPRINT",EDGE,{"derivedFrom":sQuery(id+"F0.wireOp",EDGE,"E261.bottom")}),1.0]])]});
            var Q47;
            Q47=makeQuery(id+"F0.imprint","IMPRINT",FACE,{"disambiguationData":[TD([[makeQuery(id+"F0.imprint","IMPRINT",EDGE,{"derivedFrom":sQuery(id+"F0.wireOp",EDGE,"E266.bottom")}),1.0]])]});
            var Q48;
            Q48=makeQuery(id+"F0.imprint","IMPRINT",FACE,{"disambiguationData":[TD([[makeQuery(id+"F0.imprint","IMPRINT",EDGE,{"derivedFrom":sQuery(id+"F0.wireOp",EDGE,"E251.bottom")}),1.0]])]});
            var Q49;
            Q49=makeQuery(id+"F0.imprint","IMPRINT",FACE,{"disambiguationData":[TD([[makeQuery(id+"F0.imprint","IMPRINT",EDGE,{"derivedFrom":sQuery(id+"F0.wireOp",EDGE,"E256.bottom")}),1.0]])]});
            var Q50;
            Q50=makeQuery(id+"F0.imprint","IMPRINT",FACE,{"disambiguationData":[TD([[makeQuery(id+"F0.imprint","IMPRINT",EDGE,{"derivedFrom":sQuery(id+"F0.wireOp",EDGE,"E241.bottom")}),1.0]])]});
            var Q51;
            Q51=makeQuery(id+"F0.imprint","IMPRINT",FACE,{"disambiguationData":[TD([[makeQuery(id+"F0.imprint","IMPRINT",EDGE,{"derivedFrom":sQuery(id+"F0.wireOp",EDGE,"E246.bottom")}),1.0]])]});
            var Q52;
            Q52=makeQuery(id+"F0.imprint","IMPRINT",FACE,{"disambiguationData":[TD([[makeQuery(id+"F0.imprint","IMPRINT",EDGE,{"derivedFrom":sQuery(id+"F0.wireOp",EDGE,"E231.bottom")}),1.0]])]});
            var Q53;
            Q53=makeQuery(id+"F0.imprint","IMPRINT",FACE,{"disambiguationData":[TD([[makeQuery(id+"F0.imprint","IMPRINT",EDGE,{"derivedFrom":sQuery(id+"F0.wireOp",EDGE,"E236.bottom")}),1.0]])]});
            var Q54;
            Q54=makeQuery(id+"F0.imprint","IMPRINT",FACE,{"disambiguationData":[TD([[makeQuery(id+"F0.imprint","IMPRINT",EDGE,{"derivedFrom":sQuery(id+"F0.wireOp",EDGE,"E221.bottom")}),1.0]])]});
            var Q55;
            Q55=makeQuery(id+"F0.imprint","IMPRINT",FACE,{"disambiguationData":[TD([[makeQuery(id+"F0.imprint","IMPRINT",EDGE,{"derivedFrom":sQuery(id+"F0.wireOp",EDGE,"E226.bottom")}),1.0]])]});
            var Q56;
            Q56=makeQuery(id+"F0.imprint","IMPRINT",FACE,{"disambiguationData":[TD([[makeQuery(id+"F0.imprint","IMPRINT",EDGE,{"derivedFrom":sQuery(id+"F0.wireOp",EDGE,"E211.bottom")}),1.0]])]});
            var Q57;
            Q57=makeQuery(id+"F0.imprint","IMPRINT",FACE,{"disambiguationData":[TD([[makeQuery(id+"F0.imprint","IMPRINT",EDGE,{"derivedFrom":sQuery(id+"F0.wireOp",EDGE,"E216.bottom")}),1.0]])]});
            var Q58;
            Q58=makeQuery(id+"F0.imprint","IMPRINT",FACE,{"disambiguationData":[TD([[makeQuery(id+"F0.imprint","IMPRINT",EDGE,{"derivedFrom":sQuery(id+"F0.wireOp",EDGE,"E201.bottom")}),1.0]])]});
            var Q59;
            Q59=makeQuery(id+"F0.imprint","IMPRINT",FACE,{"disambiguationData":[TD([[makeQuery(id+"F0.imprint","IMPRINT",EDGE,{"derivedFrom":sQuery(id+"F0.wireOp",EDGE,"E206.bottom")}),1.0]])]});
            var Q60;
            Q60=makeQuery(id+"F0.imprint","IMPRINT",FACE,{"disambiguationData":[TD([[makeQuery(id+"F0.imprint","IMPRINT",EDGE,{"derivedFrom":sQuery(id+"F0.wireOp",EDGE,"E396.bottom")}),1.0]])]});
            var Q61;
            Q61=makeQuery(id+"F0.imprint","IMPRINT",FACE,{"disambiguationData":[TD([[makeQuery(id+"F0.imprint","IMPRINT",EDGE,{"derivedFrom":sQuery(id+"F0.wireOp",EDGE,"E391.bottom")}),1.0]])]});
            var Q62;
            Q62=makeQuery(id+"F0.imprint","IMPRINT",FACE,{"disambiguationData":[TD([[makeQuery(id+"F0.imprint","IMPRINT",EDGE,{"derivedFrom":sQuery(id+"F0.wireOp",EDGE,"E381.bottom")}),1.0]])]});
            var Q63;
            Q63=makeQuery(id+"F0.imprint","IMPRINT",FACE,{"disambiguationData":[TD([[makeQuery(id+"F0.imprint","IMPRINT",EDGE,{"derivedFrom":sQuery(id+"F0.wireOp",EDGE,"E386.bottom")}),1.0]])]});
            var Q64;
            Q64=makeQuery(id+"F0.imprint","IMPRINT",FACE,{"disambiguationData":[TD([[makeQuery(id+"F0.imprint","IMPRINT",EDGE,{"derivedFrom":sQuery(id+"F0.wireOp",EDGE,"E371.bottom")}),1.0]])]});
            var Q65;
            Q65=makeQuery(id+"F0.imprint","IMPRINT",FACE,{"disambiguationData":[TD([[makeQuery(id+"F0.imprint","IMPRINT",EDGE,{"derivedFrom":sQuery(id+"F0.wireOp",EDGE,"E376.bottom")}),1.0]])]});
            var Q66;
            Q66=makeQuery(id+"F0.imprint","IMPRINT",FACE,{"disambiguationData":[TD([[makeQuery(id+"F0.imprint","IMPRINT",EDGE,{"derivedFrom":sQuery(id+"F0.wireOp",EDGE,"E366.bottom")}),1.0]])]});
            var Q67;
            Q67=makeQuery(id+"F0.imprint","IMPRINT",FACE,{"disambiguationData":[TD([[makeQuery(id+"F0.imprint","IMPRINT",EDGE,{"derivedFrom":sQuery(id+"F0.wireOp",EDGE,"E361.bottom")}),1.0]])]});
            var Q68;
            Q68=makeQuery(id+"F0.imprint","IMPRINT",FACE,{"disambiguationData":[TD([[makeQuery(id+"F0.imprint","IMPRINT",EDGE,{"derivedFrom":sQuery(id+"F0.wireOp",EDGE,"E356.bottom")}),1.0]])]});
            var Q69;
            Q69=makeQuery(id+"F0.imprint","IMPRINT",FACE,{"disambiguationData":[TD([[makeQuery(id+"F0.imprint","IMPRINT",EDGE,{"derivedFrom":sQuery(id+"F0.wireOp",EDGE,"E351.bottom")}),1.0]])]});
            var Q70;
            Q70=makeQuery(id+"F0.imprint","IMPRINT",FACE,{"disambiguationData":[TD([[makeQuery(id+"F0.imprint","IMPRINT",EDGE,{"derivedFrom":sQuery(id+"F0.wireOp",EDGE,"E346.bottom")}),1.0]])]});
            var Q71;
            Q71=makeQuery(id+"F0.imprint","IMPRINT",FACE,{"disambiguationData":[TD([[makeQuery(id+"F0.imprint","IMPRINT",EDGE,{"derivedFrom":sQuery(id+"F0.wireOp",EDGE,"E341.bottom")}),1.0]])]});
            var Q72;
            Q72=makeQuery(id+"F0.imprint","IMPRINT",FACE,{"disambiguationData":[TD([[makeQuery(id+"F0.imprint","IMPRINT",EDGE,{"derivedFrom":sQuery(id+"F0.wireOp",EDGE,"E336.bottom")}),1.0]])]});
            var Q73;
            Q73=makeQuery(id+"F0.imprint","IMPRINT",FACE,{"disambiguationData":[TD([[makeQuery(id+"F0.imprint","IMPRINT",EDGE,{"derivedFrom":sQuery(id+"F0.wireOp",EDGE,"E331.bottom")}),1.0]])]});
            var Q74;
            Q74=makeQuery(id+"F0.imprint","IMPRINT",FACE,{"disambiguationData":[TD([[makeQuery(id+"F0.imprint","IMPRINT",EDGE,{"derivedFrom":sQuery(id+"F0.wireOp",EDGE,"E326.bottom")}),1.0]])]});
            var Q75;
            Q75=makeQuery(id+"F0.imprint","IMPRINT",FACE,{"disambiguationData":[TD([[makeQuery(id+"F0.imprint","IMPRINT",EDGE,{"derivedFrom":sQuery(id+"F0.wireOp",EDGE,"E321.bottom")}),1.0]])]});
            var Q76;
            Q76=makeQuery(id+"F0.imprint","IMPRINT",FACE,{"disambiguationData":[TD([[makeQuery(id+"F0.imprint","IMPRINT",EDGE,{"derivedFrom":sQuery(id+"F0.wireOp",EDGE,"E311.bottom")}),1.0]])]});
            var Q77;
            Q77=makeQuery(id+"F0.imprint","IMPRINT",FACE,{"disambiguationData":[TD([[makeQuery(id+"F0.imprint","IMPRINT",EDGE,{"derivedFrom":sQuery(id+"F0.wireOp",EDGE,"E306.bottom")}),1.0]])]});
            var Q78;
            Q78=makeQuery(id+"F0.imprint","IMPRINT",FACE,{"disambiguationData":[TD([[makeQuery(id+"F0.imprint","IMPRINT",EDGE,{"derivedFrom":sQuery(id+"F0.wireOp",EDGE,"E301.bottom")}),1.0]])]});
            var Q79;
            Q79=makeQuery(id+"F0.imprint","IMPRINT",FACE,{"disambiguationData":[TD([[makeQuery(id+"F0.imprint","IMPRINT",EDGE,{"derivedFrom":sQuery(id+"F0.wireOp",EDGE,"E316.bottom")}),1.0]])]});
            extrude(context, id + "F1", {"entities" : qUnion([Q0, Q1, Q2, Q3, Q4, Q5, Q6, Q7, Q8, Q9, Q10, Q11, Q12, Q13, Q14, Q15, Q16, Q17, Q18, Q19, Q20, Q21, Q22, Q23, Q24, Q25, Q26, Q27, Q28, Q29, Q30, Q31, Q32, Q33, Q34, Q35, Q36, Q37, Q38, Q39, Q40, Q41, Q42, Q43, Q44, Q45, Q46, Q47, Q48, Q49, Q50, Q51, Q52, Q53, Q54, Q55, Q56, Q57, Q58, Q59, Q60, Q61, Q62, Q63, Q64, Q65, Q66, Q67, Q68, Q69, Q70, Q71, Q72, Q73, Q74, Q75, Q76, Q77, Q78, Q79]), "depth" : 8.9 * mm, "offsetDistance" : 25.4 * mm});
        }
        {
            var Q0;
            Q0=qCreatedBy(makeId("Top.planeOp"),FACE);
            var sketch = newSketch(context, id + "F2", { "sketchPlane" : qUnion([Q0])});
            skLineSegment(sketch, "E501.bottom", {"start": v(0, 0) * mm, "end": v(152.4, 0) * mm});
            skLineSegment(sketch, "E501.top", {"start": v(0, 152.4) * mm, "end": v(152.4, 152.4) * mm});
            skLineSegment(sketch, "E501.left", {"start": v(0, 0) * mm, "end": v(0, 152.4) * mm});
            skLineSegment(sketch, "E501.right", {"start": v(152.4, 0) * mm, "end": v(152.4, 152.4) * mm});
            skLineSegment(sketch, "E502.bottom", {"start": v(86.88, 2.4) * mm, "end": v(95.77, 2.4) * mm});
            skLineSegment(sketch, "E502.top", {"start": v(86.88, 27.8) * mm, "end": v(95.77, 27.8) * mm});
            skLineSegment(sketch, "E502.left", {"start": v(86.88, 2.4) * mm, "end": v(86.88, 27.8) * mm});
            skLineSegment(sketch, "E502.right", {"start": v(95.77, 2.4) * mm, "end": v(95.77, 27.8) * mm});
            skLineSegment(sketch, "E503.bottom", {"start": v(97.6, 2.25) * mm, "end": v(106.48, 2.25) * mm});
            skLineSegment(sketch, "E503.top", {"start": v(97.6, 27.65) * mm, "end": v(106.48, 27.65) * mm});
            skLineSegment(sketch, "E503.left", {"start": v(97.6, 2.25) * mm, "end": v(97.6, 27.65) * mm});
            skLineSegment(sketch, "E503.right", {"start": v(106.48, 2.25) * mm, "end": v(106.48, 27.65) * mm});
            skLineSegment(sketch, "E504.bottom", {"start": v(108.07, 2.32) * mm, "end": v(116.96, 2.32) * mm});
            skLineSegment(sketch, "E504.top", {"start": v(108.07, 27.72) * mm, "end": v(116.96, 27.72) * mm});
            skLineSegment(sketch, "E504.left", {"start": v(108.07, 2.32) * mm, "end": v(108.07, 27.72) * mm});
            skLineSegment(sketch, "E504.right", {"start": v(116.96, 2.32) * mm, "end": v(116.96, 27.72) * mm});
            skLineSegment(sketch, "E505.bottom", {"start": v(118.49, 2.17) * mm, "end": v(127.38, 2.17) * mm});
            skLineSegment(sketch, "E505.top", {"start": v(118.49, 27.57) * mm, "end": v(127.38, 27.57) * mm});
            skLineSegment(sketch, "E505.left", {"start": v(118.49, 2.17) * mm, "end": v(118.49, 27.57) * mm});
            skLineSegment(sketch, "E505.right", {"start": v(127.38, 2.17) * mm, "end": v(127.38, 27.57) * mm});
            skLineSegment(sketch, "E506.bottom", {"start": v(128.96, 2.25) * mm, "end": v(137.85, 2.25) * mm});
            skLineSegment(sketch, "E506.top", {"start": v(128.96, 27.65) * mm, "end": v(137.85, 27.65) * mm});
            skLineSegment(sketch, "E506.left", {"start": v(128.96, 2.25) * mm, "end": v(128.96, 27.65) * mm});
            skLineSegment(sketch, "E506.right", {"start": v(137.85, 2.25) * mm, "end": v(137.85, 27.65) * mm});
            skLineSegment(sketch, "E507.bottom", {"start": v(139.39, 2.6) * mm, "end": v(148.28, 2.6) * mm});
            skLineSegment(sketch, "E507.top", {"start": v(139.39, 28) * mm, "end": v(148.28, 28) * mm});
            skLineSegment(sketch, "E507.left", {"start": v(139.39, 2.6) * mm, "end": v(139.39, 28) * mm});
            skLineSegment(sketch, "E507.right", {"start": v(148.28, 2.6) * mm, "end": v(148.28, 28) * mm});
            skLineSegment(sketch, "E508.bottom", {"start": v(86.88, 29.06) * mm, "end": v(95.77, 29.06) * mm});
            skLineSegment(sketch, "E508.top", {"start": v(86.88, 54.46) * mm, "end": v(95.77, 54.46) * mm});
            skLineSegment(sketch, "E508.left", {"start": v(86.88, 29.06) * mm, "end": v(86.88, 54.46) * mm});
            skLineSegment(sketch, "E508.right", {"start": v(95.77, 29.06) * mm, "end": v(95.77, 54.46) * mm});
            skLineSegment(sketch, "E509.bottom", {"start": v(97.6, 28.92) * mm, "end": v(106.48, 28.92) * mm});
            skLineSegment(sketch, "E509.top", {"start": v(97.6, 54.32) * mm, "end": v(106.48, 54.32) * mm});
            skLineSegment(sketch, "E509.left", {"start": v(97.6, 28.92) * mm, "end": v(97.6, 54.32) * mm});
            skLineSegment(sketch, "E509.right", {"start": v(106.48, 28.92) * mm, "end": v(106.48, 54.32) * mm});
            skLineSegment(sketch, "E510.bottom", {"start": v(108.07, 28.99) * mm, "end": v(116.96, 28.99) * mm});
            skLineSegment(sketch, "E510.top", {"start": v(108.07, 54.39) * mm, "end": v(116.96, 54.39) * mm});
            skLineSegment(sketch, "E510.left", {"start": v(108.07, 28.99) * mm, "end": v(108.07, 54.39) * mm});
            skLineSegment(sketch, "E510.right", {"start": v(116.96, 28.99) * mm, "end": v(116.96, 54.39) * mm});
            skLineSegment(sketch, "E511.bottom", {"start": v(118.49, 28.84) * mm, "end": v(127.38, 28.84) * mm});
            skLineSegment(sketch, "E511.top", {"start": v(118.49, 54.24) * mm, "end": v(127.38, 54.24) * mm});
            skLineSegment(sketch, "E511.left", {"start": v(118.49, 28.84) * mm, "end": v(118.49, 54.24) * mm});
            skLineSegment(sketch, "E511.right", {"start": v(127.38, 28.84) * mm, "end": v(127.38, 54.24) * mm});
            skLineSegment(sketch, "E512.bottom", {"start": v(128.96, 28.92) * mm, "end": v(137.85, 28.92) * mm});
            skLineSegment(sketch, "E512.top", {"start": v(128.96, 54.32) * mm, "end": v(137.85, 54.32) * mm});
            skLineSegment(sketch, "E512.left", {"start": v(128.96, 28.92) * mm, "end": v(128.96, 54.32) * mm});
            skLineSegment(sketch, "E512.right", {"start": v(137.85, 28.92) * mm, "end": v(137.85, 54.32) * mm});
            skLineSegment(sketch, "E513.bottom", {"start": v(139.39, 29.26) * mm, "end": v(148.28, 29.26) * mm});
            skLineSegment(sketch, "E513.top", {"start": v(139.39, 54.66) * mm, "end": v(148.28, 54.66) * mm});
            skLineSegment(sketch, "E513.left", {"start": v(139.39, 29.26) * mm, "end": v(139.39, 54.66) * mm});
            skLineSegment(sketch, "E513.right", {"start": v(148.28, 29.26) * mm, "end": v(148.28, 54.66) * mm});
            skLineSegment(sketch, "E514.bottom", {"start": v(86.96, 55.48) * mm, "end": v(95.85, 55.48) * mm});
            skLineSegment(sketch, "E514.top", {"start": v(86.96, 80.88) * mm, "end": v(95.85, 80.88) * mm});
            skLineSegment(sketch, "E514.left", {"start": v(86.96, 55.48) * mm, "end": v(86.96, 80.88) * mm});
            skLineSegment(sketch, "E514.right", {"start": v(95.85, 55.48) * mm, "end": v(95.85, 80.88) * mm});
            skLineSegment(sketch, "E515.bottom", {"start": v(97.67, 55.34) * mm, "end": v(106.56, 55.34) * mm});
            skLineSegment(sketch, "E515.top", {"start": v(97.67, 80.74) * mm, "end": v(106.56, 80.74) * mm});
            skLineSegment(sketch, "E515.left", {"start": v(97.67, 55.34) * mm, "end": v(97.67, 80.74) * mm});
            skLineSegment(sketch, "E515.right", {"start": v(106.56, 55.34) * mm, "end": v(106.56, 80.74) * mm});
            skLineSegment(sketch, "E516.bottom", {"start": v(108.14, 55.4) * mm, "end": v(117.03, 55.4) * mm});
            skLineSegment(sketch, "E516.top", {"start": v(108.14, 80.8) * mm, "end": v(117.03, 80.8) * mm});
            skLineSegment(sketch, "E516.left", {"start": v(108.14, 55.4) * mm, "end": v(108.14, 80.8) * mm});
            skLineSegment(sketch, "E516.right", {"start": v(117.03, 55.4) * mm, "end": v(117.03, 80.8) * mm});
            skLineSegment(sketch, "E517.bottom", {"start": v(118.57, 55.26) * mm, "end": v(127.46, 55.26) * mm});
            skLineSegment(sketch, "E517.top", {"start": v(118.57, 80.66) * mm, "end": v(127.46, 80.66) * mm});
            skLineSegment(sketch, "E517.left", {"start": v(118.57, 55.26) * mm, "end": v(118.57, 80.66) * mm});
            skLineSegment(sketch, "E517.right", {"start": v(127.46, 55.26) * mm, "end": v(127.46, 80.66) * mm});
            skLineSegment(sketch, "E518.bottom", {"start": v(129.04, 55.34) * mm, "end": v(137.93, 55.34) * mm});
            skLineSegment(sketch, "E518.top", {"start": v(129.04, 80.74) * mm, "end": v(137.93, 80.74) * mm});
            skLineSegment(sketch, "E518.left", {"start": v(129.04, 55.34) * mm, "end": v(129.04, 80.74) * mm});
            skLineSegment(sketch, "E518.right", {"start": v(137.93, 55.34) * mm, "end": v(137.93, 80.74) * mm});
            skLineSegment(sketch, "E519.bottom", {"start": v(139.46, 55.68) * mm, "end": v(148.35, 55.68) * mm});
            skLineSegment(sketch, "E519.top", {"start": v(139.46, 81.08) * mm, "end": v(148.35, 81.08) * mm});
            skLineSegment(sketch, "E519.left", {"start": v(139.46, 55.68) * mm, "end": v(139.46, 81.08) * mm});
            skLineSegment(sketch, "E519.right", {"start": v(148.35, 55.68) * mm, "end": v(148.35, 81.08) * mm});
            skLineSegment(sketch, "E520.bottom", {"start": v(86.82, 82.7) * mm, "end": v(95.71, 82.7) * mm});
            skLineSegment(sketch, "E520.top", {"start": v(86.82, 108.1) * mm, "end": v(95.71, 108.1) * mm});
            skLineSegment(sketch, "E520.left", {"start": v(86.82, 82.7) * mm, "end": v(86.82, 108.1) * mm});
            skLineSegment(sketch, "E520.right", {"start": v(95.71, 82.7) * mm, "end": v(95.71, 108.1) * mm});
            skLineSegment(sketch, "E521.bottom", {"start": v(97.53, 82.56) * mm, "end": v(106.42, 82.56) * mm});
            skLineSegment(sketch, "E521.top", {"start": v(97.53, 107.96) * mm, "end": v(106.42, 107.96) * mm});
            skLineSegment(sketch, "E521.left", {"start": v(97.53, 82.56) * mm, "end": v(97.53, 107.96) * mm});
            skLineSegment(sketch, "E521.right", {"start": v(106.42, 82.56) * mm, "end": v(106.42, 107.96) * mm});
            skLineSegment(sketch, "E522.bottom", {"start": v(108, 82.63) * mm, "end": v(116.9, 82.63) * mm});
            skLineSegment(sketch, "E522.top", {"start": v(108, 108.03) * mm, "end": v(116.9, 108.03) * mm});
            skLineSegment(sketch, "E522.left", {"start": v(108, 82.63) * mm, "end": v(108, 108.03) * mm});
            skLineSegment(sketch, "E522.right", {"start": v(116.9, 82.63) * mm, "end": v(116.9, 108.03) * mm});
            skLineSegment(sketch, "E523.bottom", {"start": v(118.42, 82.49) * mm, "end": v(127.31, 82.49) * mm});
            skLineSegment(sketch, "E523.top", {"start": v(118.42, 107.89) * mm, "end": v(127.31, 107.89) * mm});
            skLineSegment(sketch, "E523.left", {"start": v(118.42, 82.49) * mm, "end": v(118.42, 107.89) * mm});
            skLineSegment(sketch, "E523.right", {"start": v(127.31, 82.49) * mm, "end": v(127.31, 107.89) * mm});
            skLineSegment(sketch, "E524.bottom", {"start": v(128.9, 82.57) * mm, "end": v(137.79, 82.57) * mm});
            skLineSegment(sketch, "E524.top", {"start": v(128.9, 107.97) * mm, "end": v(137.79, 107.97) * mm});
            skLineSegment(sketch, "E524.left", {"start": v(128.9, 82.57) * mm, "end": v(128.9, 107.97) * mm});
            skLineSegment(sketch, "E524.right", {"start": v(137.79, 82.57) * mm, "end": v(137.79, 107.97) * mm});
            skLineSegment(sketch, "E525.bottom", {"start": v(139.32, 82.9) * mm, "end": v(148.21, 82.9) * mm});
            skLineSegment(sketch, "E525.top", {"start": v(139.32, 108.3) * mm, "end": v(148.21, 108.3) * mm});
            skLineSegment(sketch, "E525.left", {"start": v(139.32, 82.9) * mm, "end": v(139.32, 108.3) * mm});
            skLineSegment(sketch, "E525.right", {"start": v(148.21, 82.9) * mm, "end": v(148.21, 108.3) * mm});
            skLineSegment(sketch, "E526.bottom", {"start": v(87.12, 109.44) * mm, "end": v(96, 109.44) * mm});
            skLineSegment(sketch, "E526.top", {"start": v(87.12, 134.84) * mm, "end": v(96, 134.84) * mm});
            skLineSegment(sketch, "E526.left", {"start": v(87.12, 109.44) * mm, "end": v(87.12, 134.84) * mm});
            skLineSegment(sketch, "E526.right", {"start": v(96, 109.44) * mm, "end": v(96, 134.84) * mm});
            skLineSegment(sketch, "E527.bottom", {"start": v(97.83, 109.3) * mm, "end": v(106.72, 109.3) * mm});
            skLineSegment(sketch, "E527.top", {"start": v(97.83, 134.7) * mm, "end": v(106.72, 134.7) * mm});
            skLineSegment(sketch, "E527.left", {"start": v(97.83, 109.3) * mm, "end": v(97.83, 134.7) * mm});
            skLineSegment(sketch, "E527.right", {"start": v(106.72, 109.3) * mm, "end": v(106.72, 134.7) * mm});
            skLineSegment(sketch, "E528.bottom", {"start": v(108.3, 109.36) * mm, "end": v(117.2, 109.36) * mm});
            skLineSegment(sketch, "E528.top", {"start": v(108.3, 134.76) * mm, "end": v(117.2, 134.76) * mm});
            skLineSegment(sketch, "E528.left", {"start": v(108.3, 109.36) * mm, "end": v(108.3, 134.76) * mm});
            skLineSegment(sketch, "E528.right", {"start": v(117.2, 109.36) * mm, "end": v(117.2, 134.76) * mm});
            skLineSegment(sketch, "E529.bottom", {"start": v(118.72, 109.22) * mm, "end": v(127.61, 109.22) * mm});
            skLineSegment(sketch, "E529.top", {"start": v(118.72, 134.62) * mm, "end": v(127.61, 134.62) * mm});
            skLineSegment(sketch, "E529.left", {"start": v(118.72, 109.22) * mm, "end": v(118.72, 134.62) * mm});
            skLineSegment(sketch, "E529.right", {"start": v(127.61, 109.22) * mm, "end": v(127.61, 134.62) * mm});
            skLineSegment(sketch, "E530.bottom", {"start": v(129.2, 109.3) * mm, "end": v(138.09, 109.3) * mm});
            skLineSegment(sketch, "E530.top", {"start": v(129.2, 134.7) * mm, "end": v(138.09, 134.7) * mm});
            skLineSegment(sketch, "E530.left", {"start": v(129.2, 109.3) * mm, "end": v(129.2, 134.7) * mm});
            skLineSegment(sketch, "E530.right", {"start": v(138.09, 109.3) * mm, "end": v(138.09, 134.7) * mm});
            skLineSegment(sketch, "E531.bottom", {"start": v(139.62, 109.64) * mm, "end": v(148.5, 109.64) * mm});
            skLineSegment(sketch, "E531.top", {"start": v(139.62, 135.04) * mm, "end": v(148.5, 135.04) * mm});
            skLineSegment(sketch, "E531.left", {"start": v(139.62, 109.64) * mm, "end": v(139.62, 135.04) * mm});
            skLineSegment(sketch, "E531.right", {"start": v(148.5, 109.64) * mm, "end": v(148.5, 135.04) * mm});
            skSolve(sketch);
        }
        {
            var Q0;
            Q0=makeQuery(id+"F2.imprint","IMPRINT",FACE,{"disambiguationData":[TD([[makeQuery(id+"F2.imprint","IMPRINT",EDGE,{"derivedFrom":sQuery(id+"F2.wireOp",EDGE,"E502.bottom")}),1.0]])]});
            var Q1;
            Q1=makeQuery(id+"F2.imprint","IMPRINT",FACE,{"disambiguationData":[TD([[makeQuery(id+"F2.imprint","IMPRINT",EDGE,{"derivedFrom":sQuery(id+"F2.wireOp",EDGE,"E508.bottom")}),1.0]])]});
            var Q2;
            Q2=makeQuery(id+"F2.imprint","IMPRINT",FACE,{"disambiguationData":[TD([[makeQuery(id+"F2.imprint","IMPRINT",EDGE,{"derivedFrom":sQuery(id+"F2.wireOp",EDGE,"E514.bottom")}),1.0]])]});
            var Q3;
            Q3=makeQuery(id+"F2.imprint","IMPRINT",FACE,{"disambiguationData":[TD([[makeQuery(id+"F2.imprint","IMPRINT",EDGE,{"derivedFrom":sQuery(id+"F2.wireOp",EDGE,"E520.bottom")}),1.0]])]});
            var Q4;
            Q4=makeQuery(id+"F2.imprint","IMPRINT",FACE,{"disambiguationData":[TD([[makeQuery(id+"F2.imprint","IMPRINT",EDGE,{"derivedFrom":sQuery(id+"F2.wireOp",EDGE,"E526.bottom")}),1.0]])]});
            var Q5;
            Q5=makeQuery(id+"F2.imprint","IMPRINT",FACE,{"disambiguationData":[TD([[makeQuery(id+"F2.imprint","IMPRINT",EDGE,{"derivedFrom":sQuery(id+"F2.wireOp",EDGE,"E527.bottom")}),1.0]])]});
            var Q6;
            Q6=makeQuery(id+"F2.imprint","IMPRINT",FACE,{"disambiguationData":[TD([[makeQuery(id+"F2.imprint","IMPRINT",EDGE,{"derivedFrom":sQuery(id+"F2.wireOp",EDGE,"E521.bottom")}),1.0]])]});
            var Q7;
            Q7=makeQuery(id+"F2.imprint","IMPRINT",FACE,{"disambiguationData":[TD([[makeQuery(id+"F2.imprint","IMPRINT",EDGE,{"derivedFrom":sQuery(id+"F2.wireOp",EDGE,"E515.bottom")}),1.0]])]});
            var Q8;
            Q8=makeQuery(id+"F2.imprint","IMPRINT",FACE,{"disambiguationData":[TD([[makeQuery(id+"F2.imprint","IMPRINT",EDGE,{"derivedFrom":sQuery(id+"F2.wireOp",EDGE,"E509.bottom")}),1.0]])]});
            var Q9;
            Q9=makeQuery(id+"F2.imprint","IMPRINT",FACE,{"disambiguationData":[TD([[makeQuery(id+"F2.imprint","IMPRINT",EDGE,{"derivedFrom":sQuery(id+"F2.wireOp",EDGE,"E503.bottom")}),1.0]])]});
            var Q10;
            Q10=makeQuery(id+"F2.imprint","IMPRINT",FACE,{"disambiguationData":[TD([[makeQuery(id+"F2.imprint","IMPRINT",EDGE,{"derivedFrom":sQuery(id+"F2.wireOp",EDGE,"E504.bottom")}),1.0]])]});
            var Q11;
            Q11=makeQuery(id+"F2.imprint","IMPRINT",FACE,{"disambiguationData":[TD([[makeQuery(id+"F2.imprint","IMPRINT",EDGE,{"derivedFrom":sQuery(id+"F2.wireOp",EDGE,"E510.bottom")}),1.0]])]});
            var Q12;
            Q12=makeQuery(id+"F2.imprint","IMPRINT",FACE,{"disambiguationData":[TD([[makeQuery(id+"F2.imprint","IMPRINT",EDGE,{"derivedFrom":sQuery(id+"F2.wireOp",EDGE,"E516.bottom")}),1.0]])]});
            var Q13;
            Q13=makeQuery(id+"F2.imprint","IMPRINT",FACE,{"disambiguationData":[TD([[makeQuery(id+"F2.imprint","IMPRINT",EDGE,{"derivedFrom":sQuery(id+"F2.wireOp",EDGE,"E522.bottom")}),1.0]])]});
            var Q14;
            Q14=makeQuery(id+"F2.imprint","IMPRINT",FACE,{"disambiguationData":[TD([[makeQuery(id+"F2.imprint","IMPRINT",EDGE,{"derivedFrom":sQuery(id+"F2.wireOp",EDGE,"E528.bottom")}),1.0]])]});
            var Q15;
            Q15=makeQuery(id+"F2.imprint","IMPRINT",FACE,{"disambiguationData":[TD([[makeQuery(id+"F2.imprint","IMPRINT",EDGE,{"derivedFrom":sQuery(id+"F2.wireOp",EDGE,"E529.bottom")}),1.0]])]});
            var Q16;
            Q16=makeQuery(id+"F2.imprint","IMPRINT",FACE,{"disambiguationData":[TD([[makeQuery(id+"F2.imprint","IMPRINT",EDGE,{"derivedFrom":sQuery(id+"F2.wireOp",EDGE,"E523.bottom")}),1.0]])]});
            var Q17;
            Q17=makeQuery(id+"F2.imprint","IMPRINT",FACE,{"disambiguationData":[TD([[makeQuery(id+"F2.imprint","IMPRINT",EDGE,{"derivedFrom":sQuery(id+"F2.wireOp",EDGE,"E517.bottom")}),1.0]])]});
            var Q18;
            Q18=makeQuery(id+"F2.imprint","IMPRINT",FACE,{"disambiguationData":[TD([[makeQuery(id+"F2.imprint","IMPRINT",EDGE,{"derivedFrom":sQuery(id+"F2.wireOp",EDGE,"E511.bottom")}),1.0]])]});
            var Q19;
            Q19=makeQuery(id+"F2.imprint","IMPRINT",FACE,{"disambiguationData":[TD([[makeQuery(id+"F2.imprint","IMPRINT",EDGE,{"derivedFrom":sQuery(id+"F2.wireOp",EDGE,"E505.bottom")}),1.0]])]});
            var Q20;
            Q20=makeQuery(id+"F2.imprint","IMPRINT",FACE,{"disambiguationData":[TD([[makeQuery(id+"F2.imprint","IMPRINT",EDGE,{"derivedFrom":sQuery(id+"F2.wireOp",EDGE,"E506.bottom")}),1.0]])]});
            var Q21;
            Q21=makeQuery(id+"F2.imprint","IMPRINT",FACE,{"disambiguationData":[TD([[makeQuery(id+"F2.imprint","IMPRINT",EDGE,{"derivedFrom":sQuery(id+"F2.wireOp",EDGE,"E512.bottom")}),1.0]])]});
            var Q22;
            Q22=makeQuery(id+"F2.imprint","IMPRINT",FACE,{"disambiguationData":[TD([[makeQuery(id+"F2.imprint","IMPRINT",EDGE,{"derivedFrom":sQuery(id+"F2.wireOp",EDGE,"E518.bottom")}),1.0]])]});
            var Q23;
            Q23=makeQuery(id+"F2.imprint","IMPRINT",FACE,{"disambiguationData":[TD([[makeQuery(id+"F2.imprint","IMPRINT",EDGE,{"derivedFrom":sQuery(id+"F2.wireOp",EDGE,"E524.bottom")}),1.0]])]});
            var Q24;
            Q24=makeQuery(id+"F2.imprint","IMPRINT",FACE,{"disambiguationData":[TD([[makeQuery(id+"F2.imprint","IMPRINT",EDGE,{"derivedFrom":sQuery(id+"F2.wireOp",EDGE,"E530.bottom")}),1.0]])]});
            var Q25;
            Q25=makeQuery(id+"F2.imprint","IMPRINT",FACE,{"disambiguationData":[TD([[makeQuery(id+"F2.imprint","IMPRINT",EDGE,{"derivedFrom":sQuery(id+"F2.wireOp",EDGE,"E531.bottom")}),1.0]])]});
            var Q26;
            Q26=makeQuery(id+"F2.imprint","IMPRINT",FACE,{"disambiguationData":[TD([[makeQuery(id+"F2.imprint","IMPRINT",EDGE,{"derivedFrom":sQuery(id+"F2.wireOp",EDGE,"E525.bottom")}),1.0]])]});
            var Q27;
            Q27=makeQuery(id+"F2.imprint","IMPRINT",FACE,{"disambiguationData":[TD([[makeQuery(id+"F2.imprint","IMPRINT",EDGE,{"derivedFrom":sQuery(id+"F2.wireOp",EDGE,"E519.bottom")}),1.0]])]});
            var Q28;
            Q28=makeQuery(id+"F2.imprint","IMPRINT",FACE,{"disambiguationData":[TD([[makeQuery(id+"F2.imprint","IMPRINT",EDGE,{"derivedFrom":sQuery(id+"F2.wireOp",EDGE,"E513.bottom")}),1.0]])]});
            var Q29;
            Q29=makeQuery(id+"F2.imprint","IMPRINT",FACE,{"disambiguationData":[TD([[makeQuery(id+"F2.imprint","IMPRINT",EDGE,{"derivedFrom":sQuery(id+"F2.wireOp",EDGE,"E507.bottom")}),1.0]])]});
            extrude(context, id + "F3", {"entities" : qUnion([Q0, Q1, Q2, Q3, Q4, Q5, Q6, Q7, Q8, Q9, Q10, Q11, Q12, Q13, Q14, Q15, Q16, Q17, Q18, Q19, Q20, Q21, Q22, Q23, Q24, Q25, Q26, Q27, Q28, Q29]), "depth" : 4.76 * mm, "offsetDistance" : 25.4 * mm});
        }
        {
            var Q0;
            Q0=makeQuery(id+"F3.opExtrude","CAP_EDGE",EDGE,{"disambiguationData":[OSD([sQuery(id+"F2.wireOp",EDGE,"E502.bottom")])],"isStart":false});
            var Q1;
            Q1=makeQuery(id+"F3.opExtrude","CAP_EDGE",EDGE,{"disambiguationData":[OSD([sQuery(id+"F2.wireOp",EDGE,"E502.top")])],"isStart":false});
            var Q2;
            Q2=makeQuery(id+"F3.opExtrude","CAP_EDGE",EDGE,{"disambiguationData":[OSD([sQuery(id+"F2.wireOp",EDGE,"E503.top")])],"isStart":false});
            var Q3;
            Q3=makeQuery(id+"F3.opExtrude","CAP_EDGE",EDGE,{"disambiguationData":[OSD([sQuery(id+"F2.wireOp",EDGE,"E503.bottom")])],"isStart":false});
            var Q4;
            Q4=makeQuery(id+"F3.opExtrude","CAP_EDGE",EDGE,{"disambiguationData":[OSD([sQuery(id+"F2.wireOp",EDGE,"E504.bottom")])],"isStart":false});
            var Q5;
            Q5=makeQuery(id+"F3.opExtrude","CAP_EDGE",EDGE,{"disambiguationData":[OSD([sQuery(id+"F2.wireOp",EDGE,"E504.top")])],"isStart":false});
            var Q6;
            Q6=makeQuery(id+"F3.opExtrude","CAP_EDGE",EDGE,{"disambiguationData":[OSD([sQuery(id+"F2.wireOp",EDGE,"E505.top")])],"isStart":false});
            var Q7;
            Q7=makeQuery(id+"F3.opExtrude","CAP_EDGE",EDGE,{"disambiguationData":[OSD([sQuery(id+"F2.wireOp",EDGE,"E505.bottom")])],"isStart":false});
            var Q8;
            Q8=makeQuery(id+"F3.opExtrude","CAP_EDGE",EDGE,{"disambiguationData":[OSD([sQuery(id+"F2.wireOp",EDGE,"E506.bottom")])],"isStart":false});
            var Q9;
            Q9=makeQuery(id+"F3.opExtrude","CAP_EDGE",EDGE,{"disambiguationData":[OSD([sQuery(id+"F2.wireOp",EDGE,"E506.top")])],"isStart":false});
            var Q10;
            Q10=makeQuery(id+"F3.opExtrude","CAP_EDGE",EDGE,{"disambiguationData":[OSD([sQuery(id+"F2.wireOp",EDGE,"E507.top")])],"isStart":false});
            var Q11;
            Q11=makeQuery(id+"F3.opExtrude","CAP_EDGE",EDGE,{"disambiguationData":[OSD([sQuery(id+"F2.wireOp",EDGE,"E507.bottom")])],"isStart":false});
            var Q12;
            Q12=makeQuery(id+"F3.opExtrude","CAP_EDGE",EDGE,{"disambiguationData":[OSD([sQuery(id+"F2.wireOp",EDGE,"E513.bottom")])],"isStart":false});
            var Q13;
            Q13=makeQuery(id+"F3.opExtrude","CAP_EDGE",EDGE,{"disambiguationData":[OSD([sQuery(id+"F2.wireOp",EDGE,"E513.top")])],"isStart":false});
            var Q14;
            Q14=makeQuery(id+"F3.opExtrude","CAP_EDGE",EDGE,{"disambiguationData":[OSD([sQuery(id+"F2.wireOp",EDGE,"E512.top")])],"isStart":false});
            var Q15;
            Q15=makeQuery(id+"F3.opExtrude","CAP_EDGE",EDGE,{"disambiguationData":[OSD([sQuery(id+"F2.wireOp",EDGE,"E512.bottom")])],"isStart":false});
            var Q16;
            Q16=makeQuery(id+"F3.opExtrude","CAP_EDGE",EDGE,{"disambiguationData":[OSD([sQuery(id+"F2.wireOp",EDGE,"E511.bottom")])],"isStart":false});
            var Q17;
            Q17=makeQuery(id+"F3.opExtrude","CAP_EDGE",EDGE,{"disambiguationData":[OSD([sQuery(id+"F2.wireOp",EDGE,"E511.top")])],"isStart":false});
            var Q18;
            Q18=makeQuery(id+"F3.opExtrude","CAP_EDGE",EDGE,{"disambiguationData":[OSD([sQuery(id+"F2.wireOp",EDGE,"E510.top")])],"isStart":false});
            var Q19;
            Q19=makeQuery(id+"F3.opExtrude","CAP_EDGE",EDGE,{"disambiguationData":[OSD([sQuery(id+"F2.wireOp",EDGE,"E510.bottom")])],"isStart":false});
            var Q20;
            Q20=makeQuery(id+"F3.opExtrude","CAP_EDGE",EDGE,{"disambiguationData":[OSD([sQuery(id+"F2.wireOp",EDGE,"E509.bottom")])],"isStart":false});
            var Q21;
            Q21=makeQuery(id+"F3.opExtrude","CAP_EDGE",EDGE,{"disambiguationData":[OSD([sQuery(id+"F2.wireOp",EDGE,"E509.top")])],"isStart":false});
            var Q22;
            Q22=makeQuery(id+"F3.opExtrude","CAP_EDGE",EDGE,{"disambiguationData":[OSD([sQuery(id+"F2.wireOp",EDGE,"E508.top")])],"isStart":false});
            var Q23;
            Q23=makeQuery(id+"F3.opExtrude","CAP_EDGE",EDGE,{"disambiguationData":[OSD([sQuery(id+"F2.wireOp",EDGE,"E508.bottom")])],"isStart":false});
            var Q24;
            Q24=makeQuery(id+"F3.opExtrude","CAP_EDGE",EDGE,{"disambiguationData":[OSD([sQuery(id+"F2.wireOp",EDGE,"E514.bottom")])],"isStart":false});
            var Q25;
            Q25=makeQuery(id+"F3.opExtrude","CAP_EDGE",EDGE,{"disambiguationData":[OSD([sQuery(id+"F2.wireOp",EDGE,"E514.top")])],"isStart":false});
            var Q26;
            Q26=makeQuery(id+"F3.opExtrude","CAP_EDGE",EDGE,{"disambiguationData":[OSD([sQuery(id+"F2.wireOp",EDGE,"E515.top")])],"isStart":false});
            var Q27;
            Q27=makeQuery(id+"F3.opExtrude","CAP_EDGE",EDGE,{"disambiguationData":[OSD([sQuery(id+"F2.wireOp",EDGE,"E515.bottom")])],"isStart":false});
            var Q28;
            Q28=makeQuery(id+"F3.opExtrude","CAP_EDGE",EDGE,{"disambiguationData":[OSD([sQuery(id+"F2.wireOp",EDGE,"E516.bottom")])],"isStart":false});
            var Q29;
            Q29=makeQuery(id+"F3.opExtrude","CAP_EDGE",EDGE,{"disambiguationData":[OSD([sQuery(id+"F2.wireOp",EDGE,"E516.top")])],"isStart":false});
            var Q30;
            Q30=makeQuery(id+"F3.opExtrude","CAP_EDGE",EDGE,{"disambiguationData":[OSD([sQuery(id+"F2.wireOp",EDGE,"E517.top")])],"isStart":false});
            var Q31;
            Q31=makeQuery(id+"F3.opExtrude","CAP_EDGE",EDGE,{"disambiguationData":[OSD([sQuery(id+"F2.wireOp",EDGE,"E517.bottom")])],"isStart":false});
            var Q32;
            Q32=makeQuery(id+"F3.opExtrude","CAP_EDGE",EDGE,{"disambiguationData":[OSD([sQuery(id+"F2.wireOp",EDGE,"E518.bottom")])],"isStart":false});
            var Q33;
            Q33=makeQuery(id+"F3.opExtrude","CAP_EDGE",EDGE,{"disambiguationData":[OSD([sQuery(id+"F2.wireOp",EDGE,"E518.top")])],"isStart":false});
            var Q34;
            Q34=makeQuery(id+"F3.opExtrude","CAP_EDGE",EDGE,{"disambiguationData":[OSD([sQuery(id+"F2.wireOp",EDGE,"E519.top")])],"isStart":false});
            var Q35;
            Q35=makeQuery(id+"F3.opExtrude","CAP_EDGE",EDGE,{"disambiguationData":[OSD([sQuery(id+"F2.wireOp",EDGE,"E519.bottom")])],"isStart":false});
            var Q36;
            Q36=makeQuery(id+"F3.opExtrude","CAP_EDGE",EDGE,{"disambiguationData":[OSD([sQuery(id+"F2.wireOp",EDGE,"E525.bottom")])],"isStart":false});
            var Q37;
            Q37=makeQuery(id+"F3.opExtrude","CAP_EDGE",EDGE,{"disambiguationData":[OSD([sQuery(id+"F2.wireOp",EDGE,"E525.top")])],"isStart":false});
            var Q38;
            Q38=makeQuery(id+"F3.opExtrude","CAP_EDGE",EDGE,{"disambiguationData":[OSD([sQuery(id+"F2.wireOp",EDGE,"E524.top")])],"isStart":false});
            var Q39;
            Q39=makeQuery(id+"F3.opExtrude","CAP_EDGE",EDGE,{"disambiguationData":[OSD([sQuery(id+"F2.wireOp",EDGE,"E524.bottom")])],"isStart":false});
            var Q40;
            Q40=makeQuery(id+"F3.opExtrude","CAP_EDGE",EDGE,{"disambiguationData":[OSD([sQuery(id+"F2.wireOp",EDGE,"E523.bottom")])],"isStart":false});
            var Q41;
            Q41=makeQuery(id+"F3.opExtrude","CAP_EDGE",EDGE,{"disambiguationData":[OSD([sQuery(id+"F2.wireOp",EDGE,"E523.top")])],"isStart":false});
            var Q42;
            Q42=makeQuery(id+"F3.opExtrude","CAP_EDGE",EDGE,{"disambiguationData":[OSD([sQuery(id+"F2.wireOp",EDGE,"E522.top")])],"isStart":false});
            var Q43;
            Q43=makeQuery(id+"F3.opExtrude","CAP_EDGE",EDGE,{"disambiguationData":[OSD([sQuery(id+"F2.wireOp",EDGE,"E522.bottom")])],"isStart":false});
            var Q44;
            Q44=makeQuery(id+"F3.opExtrude","CAP_EDGE",EDGE,{"disambiguationData":[OSD([sQuery(id+"F2.wireOp",EDGE,"E521.bottom")])],"isStart":false});
            var Q45;
            Q45=makeQuery(id+"F3.opExtrude","CAP_EDGE",EDGE,{"disambiguationData":[OSD([sQuery(id+"F2.wireOp",EDGE,"E521.top")])],"isStart":false});
            var Q46;
            Q46=makeQuery(id+"F3.opExtrude","CAP_EDGE",EDGE,{"disambiguationData":[OSD([sQuery(id+"F2.wireOp",EDGE,"E520.top")])],"isStart":false});
            var Q47;
            Q47=makeQuery(id+"F3.opExtrude","CAP_EDGE",EDGE,{"disambiguationData":[OSD([sQuery(id+"F2.wireOp",EDGE,"E520.bottom")])],"isStart":false});
            var Q48;
            Q48=makeQuery(id+"F3.opExtrude","CAP_EDGE",EDGE,{"disambiguationData":[OSD([sQuery(id+"F2.wireOp",EDGE,"E526.bottom")])],"isStart":false});
            var Q49;
            Q49=makeQuery(id+"F3.opExtrude","CAP_EDGE",EDGE,{"disambiguationData":[OSD([sQuery(id+"F2.wireOp",EDGE,"E526.top")])],"isStart":false});
            var Q50;
            Q50=makeQuery(id+"F3.opExtrude","CAP_EDGE",EDGE,{"disambiguationData":[OSD([sQuery(id+"F2.wireOp",EDGE,"E527.top")])],"isStart":false});
            var Q51;
            Q51=makeQuery(id+"F3.opExtrude","CAP_EDGE",EDGE,{"disambiguationData":[OSD([sQuery(id+"F2.wireOp",EDGE,"E527.bottom")])],"isStart":false});
            var Q52;
            Q52=makeQuery(id+"F3.opExtrude","CAP_EDGE",EDGE,{"disambiguationData":[OSD([sQuery(id+"F2.wireOp",EDGE,"E528.bottom")])],"isStart":false});
            var Q53;
            Q53=makeQuery(id+"F3.opExtrude","CAP_EDGE",EDGE,{"disambiguationData":[OSD([sQuery(id+"F2.wireOp",EDGE,"E528.top")])],"isStart":false});
            var Q54;
            Q54=makeQuery(id+"F3.opExtrude","CAP_EDGE",EDGE,{"disambiguationData":[OSD([sQuery(id+"F2.wireOp",EDGE,"E529.top")])],"isStart":false});
            var Q55;
            Q55=makeQuery(id+"F3.opExtrude","CAP_EDGE",EDGE,{"disambiguationData":[OSD([sQuery(id+"F2.wireOp",EDGE,"E529.bottom")])],"isStart":false});
            var Q56;
            Q56=makeQuery(id+"F3.opExtrude","CAP_EDGE",EDGE,{"disambiguationData":[OSD([sQuery(id+"F2.wireOp",EDGE,"E530.bottom")])],"isStart":false});
            var Q57;
            Q57=makeQuery(id+"F3.opExtrude","CAP_EDGE",EDGE,{"disambiguationData":[OSD([sQuery(id+"F2.wireOp",EDGE,"E530.top")])],"isStart":false});
            var Q58;
            Q58=makeQuery(id+"F3.opExtrude","CAP_EDGE",EDGE,{"disambiguationData":[OSD([sQuery(id+"F2.wireOp",EDGE,"E531.top")])],"isStart":false});
            var Q59;
            Q59=makeQuery(id+"F3.opExtrude","CAP_EDGE",EDGE,{"disambiguationData":[OSD([sQuery(id+"F2.wireOp",EDGE,"E531.bottom")])],"isStart":false});
            chamfer(context, id + "F4", {"entities" : qUnion([Q0, Q1, Q2, Q3, Q4, Q5, Q6, Q7, Q8, Q9, Q10, Q11, Q12, Q13, Q14, Q15, Q16, Q17, Q18, Q19, Q20, Q21, Q22, Q23, Q24, Q25, Q26, Q27, Q28, Q29, Q30, Q31, Q32, Q33, Q34, Q35, Q36, Q37, Q38, Q39, Q40, Q41, Q42, Q43, Q44, Q45, Q46, Q47, Q48, Q49, Q50, Q51, Q52, Q53, Q54, Q55, Q56, Q57, Q58, Q59]), "width" : 2.54 * mm, "tangentPropagation" : true});
        }
    });
